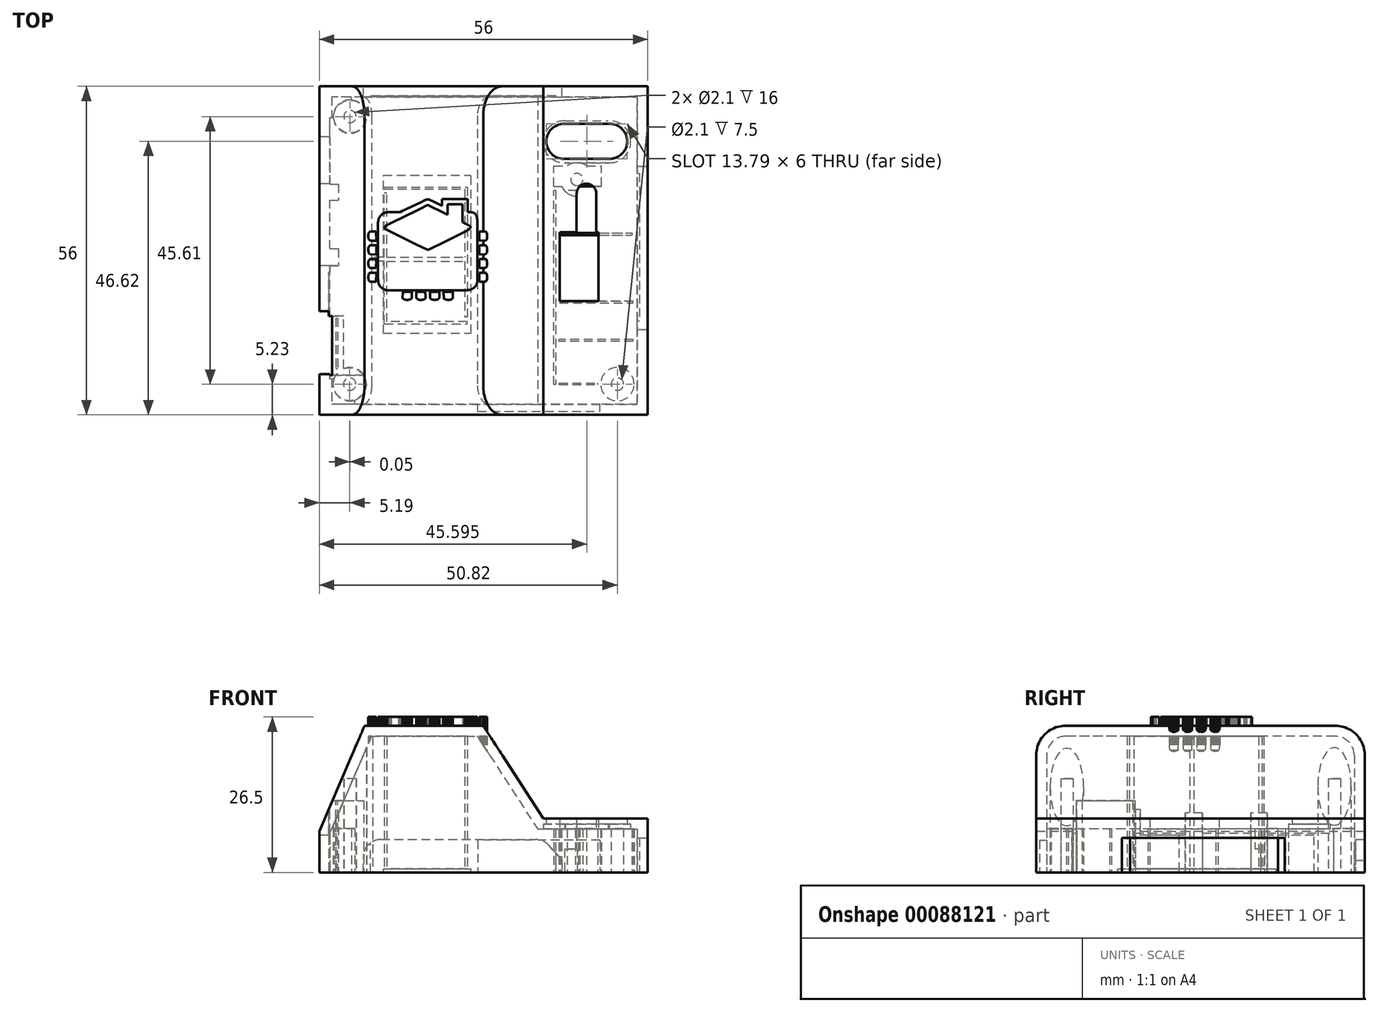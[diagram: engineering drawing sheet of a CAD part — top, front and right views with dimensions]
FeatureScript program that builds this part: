
annotation { "Feature Type Name" : "Feature", "Feature Type Description" : "" }
export const myFeature = defineFeature(function(context is Context, id is Id, definition is map)
    precondition{}
    {
        {
            var Q0;
            Q0=qCreatedBy(makeId("Top.planeOp"),FACE);
            var sketch = newSketch(context, id + "F0", { "sketchPlane" : qUnion([Q0])});
            skLineSegment(sketch, "E0.rect.bottom", {"start": v(22.84, -21.13) * mm, "end": v(-26.83, -21.13) * mm});
            skLineSegment(sketch, "E0.rect.top", {"start": v(22.84, 28.7) * mm, "end": v(-26.83, 28.7) * mm});
            skLineSegment(sketch, "E0.rect.left", {"start": v(22.84, -21.13) * mm, "end": v(22.84, 28.7) * mm});
            skPoint(sketch, "E0.rect.middle", {"position": v(-2, 3.78) * mm});
            skCircle(sketch, "E1", {"center": v(-24.81, -18.99) * mm, "radius": 1.05 * mm});
            skCircle(sketch, "E2", {"center": v(-24.76, 26.62) * mm, "radius": 1.05 * mm});
            skCircle(sketch, "E3", {"center": v(13.92, 15.91) * mm, "radius": 1.05 * mm});
            skLineSegment(sketch, "E4", {"start": v(-2, -21.13) * mm, "end": v(-2, -18.21) * mm});
            skCircle(sketch, "E5.MirrorC", {"center": v(20.82, -18.99) * mm, "radius": 1.05 * mm});
            skLineSegment(sketch, "E6.rect.bottom", {"start": v(24.75, -22.97) * mm, "end": v(-28.75, -22.97) * mm});
            skLineSegment(sketch, "E6.rect.top", {"start": v(24.75, 30.53) * mm, "end": v(-28.75, 30.53) * mm});
            skLineSegment(sketch, "E6.rect.left", {"start": v(24.75, -22.97) * mm, "end": v(24.75, 30.53) * mm});
            skLineSegment(sketch, "E6.rect.right", {"start": v(-28.75, -22.97) * mm, "end": v(-28.75, 30.53) * mm});
            skLineSegment(sketch, "E7.rect.bottom", {"start": v(26, -24.22) * mm, "end": v(-30, -24.22) * mm});
            skLineSegment(sketch, "E7.rect.top", {"start": v(26, 31.78) * mm, "end": v(-30, 31.78) * mm});
            skLineSegment(sketch, "E7.rect.left", {"start": v(26, -24.22) * mm, "end": v(26, 31.78) * mm});
            skLineSegment(sketch, "E7.rect.right", {"start": v(-30, -24.22) * mm, "end": v(-30, 31.78) * mm});
            skPoint(sketch, "E8", {"position": v(8.65, 14) * mm});
            skSolve(sketch);
        }
        {
            var Q0;
            Q0=qSketchRegion(id+"F0",true);
            var Q1;
            Q1=makeQuery(id+"F0.imprint","IMPRINT",FACE,{"disambiguationData":[TD([[makeQuery(id+"F0.imprint","IMPRINT",EDGE,{"derivedFrom":sQuery(id+"F0.wireOp",EDGE,"E1")}),-1.0]])]});
            extrude(context, id + "F1", {"entities" : qUnion([Q0, Q1]), "depth" : 25 * mm});
        }
        {
            var Q0;
            Q0=qCreatedBy(makeId("Front.planeOp"),FACE);
            var sketch = newSketch(context, id + "F2", { "sketchPlane" : qUnion([Q0])});
            skLineSegment(sketch, "E9", {"start": v(0, 0) * mm, "end": v(0, 7) * mm});
            skLineSegment(sketch, "E10", {"start": v(0, 7) * mm, "end": v(26.03, 7) * mm});
            skLineSegment(sketch, "E11", {"start": v(26.03, 9.19) * mm, "end": v(26.03, 25.51) * mm});
            skLineSegment(sketch, "E12", {"start": v(15.3, 7) * mm, "end": v(26.03, 7) * mm});
            skLineSegment(sketch, "E13", {"start": v(0, 7) * mm, "end": v(-30.02, 7) * mm});
            skLineSegment(sketch, "E14", {"start": v(-30.02, 7) * mm, "end": v(-22.06, 25.51) * mm});
            skLineSegment(sketch, "E15", {"start": v(-22.06, 25.51) * mm, "end": v(-2.39, 25.51) * mm});
            skLineSegment(sketch, "E16", {"start": v(26.03, 25.51) * mm, "end": v(-2.39, 25.51) * mm});
            skLineSegment(sketch, "E17", {"start": v(-22.06, 25.51) * mm, "end": v(-30.02, 25.51) * mm});
            skLineSegment(sketch, "E18", {"start": v(-30.02, 25.51) * mm, "end": v(-30.02, 7) * mm});
            skLineSegment(sketch, "E19", {"start": v(18.06, 10.7) * mm, "end": v(18.04, 10.7) * mm});
            skLineSegment(sketch, "E20", {"start": v(19.86, 9.19) * mm, "end": v(8.2, 9.19) * mm});
            skLineSegment(sketch, "E21", {"start": v(8.2, 9.19) * mm, "end": v(-2.39, 25.51) * mm});
            skLineSegment(sketch, "E22", {"start": v(19.86, 9.19) * mm, "end": v(26.03, 9.19) * mm});
            skSolve(sketch);
        }
        {
            var Q0;
            Q0=makeQuery(id+"F2.imprint","IMPRINT",FACE,{"disambiguationData":[TD([[makeQuery(id+"F2.imprint","IMPRINT",EDGE,{"derivedFrom":sQuery(id+"F2.wireOp",EDGE,"E14")}),1.0]])]});
            var Q1;
            {var subQ0=sQuery(id+"F2.wireOp",EDGE,"E11");Q1=makeQuery(id+"F2.imprint","IMPRINT",FACE,{"disambiguationData":[TD([[makeQuery(id+"F2.imprint","IMPRINT",EDGE,{"derivedFrom":subQ0}),1.0]])]});}
            extrude(context, id + "F3", {"entities" : qUnion([Q0, Q1]), "operationType" : NewBodyOperationType.REMOVE, "endBound" : BoundingType.UP_TO_NEXT, "oppositeDirection" : true, "depth" : 25 * mm, "hasSecondDirection" : true, "secondDirectionOppositeDirection" : false, "secondDirectionDepth" : 25 * mm});
        }
        {
            var Q0;
            Q0=makeQuery(id+"F1.opExtrude","CAP_EDGE",EDGE,{"disambiguationData":[OSD([sQuery(id+"F0.wireOp",EDGE,"E7.rect.right")])],"isStart":false});
            var Q1;
            Q1=makeQuery(id+"F3.boolean.opBoolean","COPY",EDGE,{"derivedFrom":makeQuery(id+"F3.opExtrude","TWEAK_EDGE",EDGE,{"derivedFrom":[makeQuery(id+"F1.opExtrude","CAP_FACE",FACE,{"disambiguationData":[OSD([sQuery(id+"F0.wireOp",EDGE,"E1"),sQuery(id+"F0.wireOp",EDGE,"E2"),sQuery(id+"F0.wireOp",EDGE,"E3"),sQuery(id+"F0.wireOp",EDGE,"E5.MirrorC"),sQuery(id+"F0.wireOp",EDGE,"E7.rect.bottom"),sQuery(id+"F0.wireOp",EDGE,"E7.rect.top"),sQuery(id+"F0.wireOp",EDGE,"E7.rect.left"),sQuery(id+"F0.wireOp",EDGE,"E7.rect.right")])],"isStart":false}),makeQuery(id+"F2.imprint","IMPRINT",EDGE,{"derivedFrom":sQuery(id+"F2.wireOp",EDGE,"ff17f17f-c23f-4b7b-92e3-773d52701edb")})]})});
            var Q2;
            Q2=makeQuery(id+"F3.boolean.opBoolean","COPY",EDGE,{"derivedFrom":makeQuery(id+"F3.opExtrude","TWEAK_EDGE",EDGE,{"derivedFrom":[makeQuery(id+"F1.opExtrude","CAP_FACE",FACE,{"disambiguationData":[OSD([sQuery(id+"F0.wireOp",EDGE,"E1"),sQuery(id+"F0.wireOp",EDGE,"E2"),sQuery(id+"F0.wireOp",EDGE,"E3"),sQuery(id+"F0.wireOp",EDGE,"E5.MirrorC"),sQuery(id+"F0.wireOp",EDGE,"E7.rect.bottom"),sQuery(id+"F0.wireOp",EDGE,"E7.rect.top"),sQuery(id+"F0.wireOp",EDGE,"E7.rect.left"),sQuery(id+"F0.wireOp",EDGE,"E7.rect.right")])],"isStart":false}),makeQuery(id+"F2.imprint","IMPRINT",EDGE,{"derivedFrom":sQuery(id+"F2.wireOp",EDGE,"7c30f75c-de24-4105-9ec6-0528e7197d9e")})]})});
            var Q3;
            {var subQ0=sQuery(id+"F2.wireOp",EDGE,"cpQ2IQLn-lepx-jHqE-Occg-QwCyzWVKbBFz");var subQ1=sQuery(id+"F2.wireOp",EDGE,"9136473a-ce9f-4df1-8e41-d79c079f6f02");var subQ2=makeQuery(id+"F2.imprint","INTERSECT",VERTEX,{"disambiguationData":[OD(0.0)],"derivedFrom":[subQ1,subQ0]});var subQ4=makeQuery(id+"F2.imprint","INTERSECT",VERTEX,{"disambiguationData":[OD(1.0)],"derivedFrom":[subQ1,subQ0]});Q3=makeQuery(id+"F3.boolean.opBoolean","COPY",EDGE,{"derivedFrom":makeQuery(id+"F3.opExtrude","TWEAK_EDGE",EDGE,{"derivedFrom":[makeQuery(id+"F1.opExtrude","CAP_FACE",FACE,{"disambiguationData":[OSD([sQuery(id+"F0.wireOp",EDGE,"E1"),sQuery(id+"F0.wireOp",EDGE,"E2"),sQuery(id+"F0.wireOp",EDGE,"E3"),sQuery(id+"F0.wireOp",EDGE,"E5.MirrorC"),sQuery(id+"F0.wireOp",EDGE,"E7.rect.bottom"),sQuery(id+"F0.wireOp",EDGE,"E7.rect.top"),sQuery(id+"F0.wireOp",EDGE,"E7.rect.left"),sQuery(id+"F0.wireOp",EDGE,"E7.rect.right")])],"isStart":false}),makeQuery(id+"F2.imprint","IMPRINT",EDGE,{"disambiguationData":[TD([[subQ4,1.0]])],"derivedFrom":subQ0}),makeQuery(id+"F2.imprint","IMPRINT",EDGE,{"disambiguationData":[TD([[subQ2,1.0]])],"derivedFrom":subQ0}),makeQuery(id+"F2.imprint","IMPRINT",EDGE,{"disambiguationData":[TD([[subQ2,-1.0]])],"derivedFrom":subQ0})]})});}
            var Q4;
            {var subQ0=sQuery(id+"F2.wireOp",EDGE,"cpQ2IQLn-lepx-jHqE-Occg-QwCyzWVKbBFz");var subQ1=sQuery(id+"F2.wireOp",EDGE,"9136473a-ce9f-4df1-8e41-d79c079f6f02");var subQ2=makeQuery(id+"F2.imprint","INTERSECT",VERTEX,{"disambiguationData":[OD(0.0)],"derivedFrom":[subQ1,subQ0]});var subQ3=sQuery(id+"F2.wireOp",EDGE,"7c30f75c-de24-4105-9ec6-0528e7197d9e");var subQ4=makeQuery(id+"F2.imprint","INTERSECT",VERTEX,{"derivedFrom":[subQ3,subQ0]});var subQ5=makeQuery(id+"F2.imprint","INTERSECT",VERTEX,{"disambiguationData":[OD(1.0)],"derivedFrom":[subQ1,subQ0]});Q4=makeQuery(id+"F3.boolean.opBoolean","COPY",EDGE,{"derivedFrom":makeQuery(id+"F3.opExtrude","TWEAK_EDGE",EDGE,{"disambiguationData":[OD(0.0)],"derivedFrom":[makeQuery(id+"F2.imprint","IMPRINT",EDGE,{"disambiguationData":[TD([[subQ4,1.0]])],"derivedFrom":subQ3}),makeQuery(id+"F2.imprint","IMPRINT",EDGE,{"disambiguationData":[TD([[subQ5,1.0]])],"derivedFrom":subQ0}),makeQuery(id+"F2.imprint","IMPRINT",EDGE,{"disambiguationData":[TD([[subQ2,1.0]])],"derivedFrom":subQ0}),makeQuery(id+"F2.imprint","IMPRINT",EDGE,{"disambiguationData":[TD([[subQ2,-1.0]])],"derivedFrom":subQ0})]})});}
            var Q5;
            {var subQ0=sQuery(id+"F2.wireOp",EDGE,"cpQ2IQLn-lepx-jHqE-Occg-QwCyzWVKbBFz");var subQ1=sQuery(id+"F2.wireOp",EDGE,"9136473a-ce9f-4df1-8e41-d79c079f6f02");var subQ2=makeQuery(id+"F2.imprint","INTERSECT",VERTEX,{"disambiguationData":[OD(0.0)],"derivedFrom":[subQ1,subQ0]});var subQ3=sQuery(id+"F2.wireOp",EDGE,"7c30f75c-de24-4105-9ec6-0528e7197d9e");var subQ4=makeQuery(id+"F2.imprint","INTERSECT",VERTEX,{"derivedFrom":[subQ3,subQ0]});var subQ5=makeQuery(id+"F2.imprint","INTERSECT",VERTEX,{"disambiguationData":[OD(1.0)],"derivedFrom":[subQ1,subQ0]});Q5=makeQuery(id+"F3.boolean.opBoolean","COPY",EDGE,{"derivedFrom":makeQuery(id+"F3.opExtrude","TWEAK_EDGE",EDGE,{"disambiguationData":[OD(1.0)],"derivedFrom":[makeQuery(id+"F2.imprint","IMPRINT",EDGE,{"disambiguationData":[TD([[subQ4,1.0]])],"derivedFrom":subQ3}),makeQuery(id+"F2.imprint","IMPRINT",EDGE,{"disambiguationData":[TD([[subQ5,1.0]])],"derivedFrom":subQ0}),makeQuery(id+"F2.imprint","IMPRINT",EDGE,{"disambiguationData":[TD([[subQ2,1.0]])],"derivedFrom":subQ0}),makeQuery(id+"F2.imprint","IMPRINT",EDGE,{"disambiguationData":[TD([[subQ2,-1.0]])],"derivedFrom":subQ0})]})});}
            var Q6;
            Q6=makeQuery(id+"F1.opExtrude","CAP_EDGE",EDGE,{"disambiguationData":[OSD([sQuery(id+"F0.wireOp",EDGE,"E7.rect.bottom")])],"isStart":false});
            var Q7;
            {var subQ0=sQuery(id+"F2.wireOp",EDGE,"cpQ2IQLn-lepx-jHqE-Occg-QwCyzWVKbBFz");var subQ1=sQuery(id+"F2.wireOp",EDGE,"9136473a-ce9f-4df1-8e41-d79c079f6f02");var subQ2=makeQuery(id+"F2.imprint","INTERSECT",VERTEX,{"disambiguationData":[OD(0.0)],"derivedFrom":[subQ1,subQ0]});var subQ4=makeQuery(id+"F2.imprint","INTERSECT",VERTEX,{"disambiguationData":[OD(1.0)],"derivedFrom":[subQ1,subQ0]});Q7=makeQuery(id+"F3.boolean.opBoolean","COPY",EDGE,{"derivedFrom":makeQuery(id+"F3.opExtrude","TWEAK_EDGE",EDGE,{"derivedFrom":[makeQuery(id+"F1.opExtrude","SWEPT_FACE",FACE,{"disambiguationData":[OSD([sQuery(id+"F0.wireOp",EDGE,"E7.rect.bottom")])]}),makeQuery(id+"F2.imprint","IMPRINT",EDGE,{"disambiguationData":[TD([[subQ4,1.0]])],"derivedFrom":subQ0}),makeQuery(id+"F2.imprint","IMPRINT",EDGE,{"disambiguationData":[TD([[subQ2,1.0]])],"derivedFrom":subQ0}),makeQuery(id+"F2.imprint","IMPRINT",EDGE,{"disambiguationData":[TD([[subQ2,-1.0]])],"derivedFrom":subQ0})]})});}
            var Q8;
            Q8=makeQuery(id+"F1.opExtrude","CAP_EDGE",EDGE,{"disambiguationData":[OSD([sQuery(id+"F0.wireOp",EDGE,"E7.rect.top")])],"isStart":false});
            var Q9;
            {var subQ0=sQuery(id+"F2.wireOp",EDGE,"cpQ2IQLn-lepx-jHqE-Occg-QwCyzWVKbBFz");var subQ1=sQuery(id+"F2.wireOp",EDGE,"9136473a-ce9f-4df1-8e41-d79c079f6f02");var subQ2=makeQuery(id+"F2.imprint","INTERSECT",VERTEX,{"disambiguationData":[OD(0.0)],"derivedFrom":[subQ1,subQ0]});var subQ4=makeQuery(id+"F2.imprint","INTERSECT",VERTEX,{"disambiguationData":[OD(1.0)],"derivedFrom":[subQ1,subQ0]});Q9=makeQuery(id+"F3.boolean.opBoolean","COPY",EDGE,{"derivedFrom":makeQuery(id+"F3.opExtrude","TWEAK_EDGE",EDGE,{"derivedFrom":[makeQuery(id+"F1.opExtrude","SWEPT_FACE",FACE,{"disambiguationData":[OSD([sQuery(id+"F0.wireOp",EDGE,"E7.rect.top")])]}),makeQuery(id+"F2.imprint","IMPRINT",EDGE,{"disambiguationData":[TD([[subQ4,1.0]])],"derivedFrom":subQ0}),makeQuery(id+"F2.imprint","IMPRINT",EDGE,{"disambiguationData":[TD([[subQ2,1.0]])],"derivedFrom":subQ0}),makeQuery(id+"F2.imprint","IMPRINT",EDGE,{"disambiguationData":[TD([[subQ2,-1.0]])],"derivedFrom":subQ0})]})});}
            var Q10;
            Q10=makeQuery(id+"F3.boolean.opBoolean","COPY",EDGE,{"derivedFrom":makeQuery(id+"F3.opExtrude","TWEAK_EDGE",EDGE,{"derivedFrom":[makeQuery(id+"F1.opExtrude","CAP_FACE",FACE,{"disambiguationData":[OSD([sQuery(id+"F0.wireOp",EDGE,"E1"),sQuery(id+"F0.wireOp",EDGE,"E2"),sQuery(id+"F0.wireOp",EDGE,"E3"),sQuery(id+"F0.wireOp",EDGE,"E5.MirrorC"),sQuery(id+"F0.wireOp",EDGE,"E7.rect.bottom"),sQuery(id+"F0.wireOp",EDGE,"E7.rect.top"),sQuery(id+"F0.wireOp",EDGE,"E7.rect.left"),sQuery(id+"F0.wireOp",EDGE,"E7.rect.right")])],"isStart":false}),makeQuery(id+"F2.imprint","IMPRINT",EDGE,{"derivedFrom":sQuery(id+"F2.wireOp",EDGE,"99fa5713-44e2-4710-8a3e-a5a5802f03ed")})]})});
            var Q11;
            Q11=makeQuery(id+"F3.boolean.opBoolean","COPY",EDGE,{"derivedFrom":makeQuery(id+"F3.opExtrude","TWEAK_EDGE",EDGE,{"derivedFrom":[makeQuery(id+"F1.opExtrude","CAP_FACE",FACE,{"disambiguationData":[OSD([sQuery(id+"F0.wireOp",EDGE,"E1"),sQuery(id+"F0.wireOp",EDGE,"E2"),sQuery(id+"F0.wireOp",EDGE,"E3"),sQuery(id+"F0.wireOp",EDGE,"E5.MirrorC"),sQuery(id+"F0.wireOp",EDGE,"E7.rect.bottom"),sQuery(id+"F0.wireOp",EDGE,"E7.rect.top"),sQuery(id+"F0.wireOp",EDGE,"E7.rect.left"),sQuery(id+"F0.wireOp",EDGE,"E7.rect.right")])],"isStart":false}),makeQuery(id+"F2.imprint","IMPRINT",EDGE,{"derivedFrom":sQuery(id+"F2.wireOp",EDGE,"E14")})]})});
            var Q12;
            Q12=makeQuery(id+"F3.boolean.opBoolean","COPY",EDGE,{"derivedFrom":makeQuery(id+"F3.opExtrude","TWEAK_EDGE",EDGE,{"derivedFrom":[makeQuery(id+"F1.opExtrude","CAP_FACE",FACE,{"disambiguationData":[OSD([sQuery(id+"F0.wireOp",EDGE,"E1"),sQuery(id+"F0.wireOp",EDGE,"E2"),sQuery(id+"F0.wireOp",EDGE,"E3"),sQuery(id+"F0.wireOp",EDGE,"E5.MirrorC"),sQuery(id+"F0.wireOp",EDGE,"E7.rect.bottom"),sQuery(id+"F0.wireOp",EDGE,"E7.rect.top"),sQuery(id+"F0.wireOp",EDGE,"E7.rect.left"),sQuery(id+"F0.wireOp",EDGE,"E7.rect.right")])],"isStart":false}),makeQuery(id+"F2.imprint","IMPRINT",EDGE,{"derivedFrom":sQuery(id+"F2.wireOp",EDGE,"E21")})]})});
            var Q13;
            Q13=makeQuery(id+"F3.boolean.opBoolean","COPY",EDGE,{"derivedFrom":makeQuery(id+"F3.opExtrude","TWEAK_EDGE",EDGE,{"derivedFrom":[makeQuery(id+"F2.imprint","IMPRINT",EDGE,{"derivedFrom":sQuery(id+"F2.wireOp",EDGE,"E20")}),makeQuery(id+"F2.imprint","IMPRINT",EDGE,{"derivedFrom":sQuery(id+"F2.wireOp",EDGE,"E21")})]})});
            var Q14;
            Q14=makeQuery(id+"F3.boolean.opBoolean","COPY",EDGE,{"derivedFrom":makeQuery(id+"F3.opExtrude","TWEAK_EDGE",EDGE,{"derivedFrom":[makeQuery(id+"F1.opExtrude","SWEPT_FACE",FACE,{"disambiguationData":[OSD([sQuery(id+"F0.wireOp",EDGE,"E7.rect.bottom")])]}),makeQuery(id+"F2.imprint","IMPRINT",EDGE,{"derivedFrom":sQuery(id+"F2.wireOp",EDGE,"E21")})]})});
            var Q15;
            Q15=makeQuery(id+"F3.boolean.opBoolean","COPY",EDGE,{"derivedFrom":makeQuery(id+"F3.opExtrude","TWEAK_EDGE",EDGE,{"derivedFrom":[makeQuery(id+"F1.opExtrude","SWEPT_FACE",FACE,{"disambiguationData":[OSD([sQuery(id+"F0.wireOp",EDGE,"E7.rect.top")])]}),makeQuery(id+"F2.imprint","IMPRINT",EDGE,{"derivedFrom":sQuery(id+"F2.wireOp",EDGE,"E21")})]})});
            var Q16;
            Q16=makeQuery(id+"F3.boolean.opBoolean","COPY",EDGE,{"derivedFrom":makeQuery(id+"F3.opExtrude","TWEAK_EDGE",EDGE,{"derivedFrom":[makeQuery(id+"F1.opExtrude","SWEPT_FACE",FACE,{"disambiguationData":[OSD([sQuery(id+"F0.wireOp",EDGE,"E7.rect.left")])]}),makeQuery(id+"F2.imprint","IMPRINT",EDGE,{"derivedFrom":sQuery(id+"F2.wireOp",EDGE,"E20")}),makeQuery(id+"F2.imprint","IMPRINT",EDGE,{"derivedFrom":sQuery(id+"F2.wireOp",EDGE,"E22")})]})});
            var Q17;
            Q17=makeQuery(id+"F3.boolean.opBoolean","COPY",EDGE,{"derivedFrom":makeQuery(id+"F3.opExtrude","TWEAK_EDGE",EDGE,{"derivedFrom":[makeQuery(id+"F2.imprint","IMPRINT",EDGE,{"derivedFrom":sQuery(id+"F2.wireOp",EDGE,"E20")}),makeQuery(id+"F2.imprint","IMPRINT",EDGE,{"derivedFrom":sQuery(id+"F2.wireOp",EDGE,"E21")}),makeQuery(id+"F2.imprint","IMPRINT",EDGE,{"derivedFrom":sQuery(id+"F2.wireOp",EDGE,"E22")})]})});
            fillet(context, id + "F4", {"entities" : qUnion([Q0, Q1, Q2, Q3, Q4, Q5, Q6, Q7, Q8, Q9, Q10, Q11, Q12, Q13, Q14, Q15, Q16, Q17]), "radius" : 5 * mm, "tangentPropagation" : true, "allowEdgeOverflow" : false});
        }
        {
            var Q0;
            Q0=makeQuery(id+"F1.opExtrude","SWEPT_BODY",BODY,{"disambiguationData":[OSD([sQuery(id+"F0.wireOp",EDGE,"E1"),sQuery(id+"F0.wireOp",EDGE,"E2"),sQuery(id+"F0.wireOp",EDGE,"E3"),sQuery(id+"F0.wireOp",EDGE,"E5.MirrorC"),sQuery(id+"F0.wireOp",EDGE,"E7.rect.bottom"),sQuery(id+"F0.wireOp",EDGE,"E7.rect.top"),sQuery(id+"F0.wireOp",EDGE,"E7.rect.left"),sQuery(id+"F0.wireOp",EDGE,"E7.rect.right")])]});
            transform(context, id + "F5", {"entities" : qUnion([Q0]), "transformType" : TransformType.TRANSLATION_3D, "dx" : -5 * mm, "dy" : -12 * mm, "dz" : 0 * mm, "makeCopy" : false});
        }
        {
            var Q0;
            Q0=makeQuery(id+"F1.opExtrude","CAP_FACE",FACE,{"disambiguationData":[OSD([sQuery(id+"F0.wireOp",EDGE,"E1"),sQuery(id+"F0.wireOp",EDGE,"E2"),sQuery(id+"F0.wireOp",EDGE,"E3"),sQuery(id+"F0.wireOp",EDGE,"E5.MirrorC"),sQuery(id+"F0.wireOp",EDGE,"E7.rect.bottom"),sQuery(id+"F0.wireOp",EDGE,"E7.rect.top"),sQuery(id+"F0.wireOp",EDGE,"E7.rect.left"),sQuery(id+"F0.wireOp",EDGE,"E7.rect.right")])],"isStart":true});
            shell(context, id + "F6", {"entities" : qUnion([Q0]), "thickness" : 1.8 * mm});
        }
        {
            var Q0;
            Q0=makeQuery(id+"F1.opExtrude","SWEPT_FACE",FACE,{"disambiguationData":[OSD([sQuery(id+"F0.wireOp",EDGE,"E7.rect.left")])]});
            cPlane(context, id + "F7", {"entities" : qUnion([Q0]), "cplaneType" : CPlaneType.OFFSET, "offset" : 0 * mm, "width" : 150 * mm, "height" : 150 * mm});
        }
        {
            var Q0;
            Q0=qCreatedBy(id+"F7.planeOp",FACE);
            var sketch = newSketch(context, id + "F8", { "sketchPlane" : qUnion([Q0])});
            skLineSegment(sketch, "E23.bottom", {"start": v(6.92, 0) * mm, "end": v(-20.2, 0) * mm});
            skLineSegment(sketch, "E23.top", {"start": v(6.12, 5.87) * mm, "end": v(-20.2, 5.87) * mm});
            skLineSegment(sketch, "E24", {"start": v(-20.2, 5.87) * mm, "end": v(-21.64, 5.87) * mm});
            skLineSegment(sketch, "E25", {"start": v(-21.64, 5.87) * mm, "end": v(-21.64, 0) * mm});
            skLineSegment(sketch, "E26", {"start": v(-21.64, 0) * mm, "end": v(-20.2, 0) * mm});
            skLineSegment(sketch, "E27", {"start": v(-20.2, 5.87) * mm, "end": v(-20.2, 0) * mm});
            skLineSegment(sketch, "E28", {"start": v(6.12, 5.87) * mm, "end": v(6.12, 0) * mm});
            skPoint(sketch, "E29.orphan", {"position": v(7.84, 0) * mm});
            skLineSegment(sketch, "E30", {"start": v(4.97, 0) * mm, "end": v(4.97, 5.87) * mm});
            skSolve(sketch);
        }
        {
            var Q0;
            Q0=qSketchRegion(id+"F8",true);
            extrude(context, id + "F9", {"entities" : qUnion([Q0]), "operationType" : NewBodyOperationType.REMOVE, "oppositeDirection" : true, "depth" : (1.7 - 0.3) * mm});
        }
        {
            var Q0;
            Q0=makeQuery(id+"F8.imprint","IMPRINT",FACE,{"disambiguationData":[TD([[makeQuery(id+"F8.imprint","IMPRINT",EDGE,{"derivedFrom":sQuery(id+"F8.wireOp",EDGE,"E24")}),1.0]])]});
            var Q1;
            {var subQ0=sQuery(id+"F8.wireOp",EDGE,"E23.left");Q1=makeQuery(id+"F8.imprint","IMPRINT",FACE,{"disambiguationData":[TD([[makeQuery(id+"F8.imprint","IMPRINT",EDGE,{"derivedFrom":subQ0}),1.0]])]});}
            var Q2;
            {var subQ0=sQuery(id+"F8.wireOp",EDGE,"4UiORLbo-slaH-JSft-xh6I-61qYCNnPId7j");Q2=makeQuery(id+"F8.imprint","IMPRINT",FACE,{"disambiguationData":[TD([[makeQuery(id+"F8.imprint","IMPRINT",EDGE,{"derivedFrom":subQ0}),1.0]])]});}
            var Q3;
            {var subQ0=sQuery(id+"F8.wireOp",EDGE,"E28");Q3=makeQuery(id+"F8.imprint","IMPRINT",FACE,{"disambiguationData":[TD([[makeQuery(id+"F8.imprint","IMPRINT",EDGE,{"derivedFrom":subQ0}),-1.0]])]});}
            extrude(context, id + "F10", {"entities" : qUnion([Q0, Q1, Q2, Q3]), "operationType" : NewBodyOperationType.REMOVE, "oppositeDirection" : true, "depth" : 2 * mm});
        }
        {
            var Q0;
            Q0=makeQuery(id+"F1.opExtrude","SWEPT_FACE",FACE,{"disambiguationData":[OSD([sQuery(id+"F0.wireOp",EDGE,"E7.rect.right")])]});
            cPlane(context, id + "F11", {"entities" : qUnion([Q0]), "cplaneType" : CPlaneType.OFFSET, "offset" : 0 * mm, "width" : 150 * mm, "height" : 150 * mm});
        }
        {
            var Q0;
            Q0=qCreatedBy(id+"F11.planeOp",FACE);
            var sketch = newSketch(context, id + "F12", { "sketchPlane" : qUnion([Q0])});
            skLineSegment(sketch, "E31.top", {"start": v(-11.15, 6.31) * mm, "end": v(-3.45, 6.31) * mm});
            skLineSegment(sketch, "E32", {"start": v(27.25, 11.15) * mm, "end": v(27.25, 11.15) * mm});
            skLineSegment(sketch, "E33", {"start": v(-11.15, 0) * mm, "end": v(-11.15, 6.31) * mm});
            skPoint(sketch, "E34.start.orphan", {"position": v(-15.15, 0) * mm});
            skLineSegment(sketch, "E35", {"start": v(29.28, 0) * mm, "end": v(-11.15, 0) * mm});
            skLineSegment(sketch, "E36", {"start": v(-10.29, 6.31) * mm, "end": v(-10.29, 0) * mm});
            skLineSegment(sketch, "E37", {"start": v(19.35, 12.2) * mm, "end": v(29.28, 12.2) * mm});
            skLineSegment(sketch, "E38", {"start": v(-11.15, 3.16) * mm, "end": v(-3.45, 3.16) * mm, "construction": true});
            skLineSegment(sketch, "E39", {"start": v(-3.45, 3.16) * mm, "end": v(-0.05, 3.16) * mm, "construction": true});
            skLineSegment(sketch, "E40", {"start": v(-0.05, 3.16) * mm, "end": v(7.65, 3.16) * mm, "construction": true});
            skLineSegment(sketch, "E41", {"start": v(7.65, 3.16) * mm, "end": v(11.05, 3.16) * mm, "construction": true});
            skLineSegment(sketch, "E42.trimOffspring", {"start": v(11.05, 6.31) * mm, "end": v(18.53, 6.31) * mm});
            skLineSegment(sketch, "E43", {"start": v(11.9, 6.31) * mm, "end": v(11.9, 0) * mm});
            skLineSegment(sketch, "E44", {"start": v(0, 6.31) * mm, "end": v(7.65, 6.31) * mm});
            skLineSegment(sketch, "E45", {"start": v(7.65, 0) * mm, "end": v(0, 0) * mm});
            skLineSegment(sketch, "E46", {"start": v(-3.45, 0) * mm, "end": v(-11.15, 0) * mm});
            skLineSegment(sketch, "E47", {"start": v(30.08, 0) * mm, "end": v(11.05, 0) * mm});
            skLineSegment(sketch, "E48.bottom", {"start": v(-0.32, 0) * mm, "end": v(-3.15, 0) * mm});
            skLineSegment(sketch, "E48.top", {"start": v(-0.32, 6.31) * mm, "end": v(-3.15, 6.31) * mm});
            skLineSegment(sketch, "E48.left", {"start": v(-0.32, 0) * mm, "end": v(-0.32, 6.31) * mm});
            skLineSegment(sketch, "E48.right", {"start": v(-3.15, 0) * mm, "end": v(-3.15, 6.31) * mm});
            skLineSegment(sketch, "E49.bottom", {"start": v(10.8, 0) * mm, "end": v(7.92, 0) * mm});
            skLineSegment(sketch, "E49.top", {"start": v(10.8, 6.31) * mm, "end": v(7.92, 6.31) * mm});
            skLineSegment(sketch, "E49.left", {"start": v(10.8, 0) * mm, "end": v(10.8, 6.31) * mm});
            skLineSegment(sketch, "E49.right", {"start": v(7.92, 0) * mm, "end": v(7.92, 6.31) * mm});
            skLineSegment(sketch, "E50", {"start": v(-3.45, 6.31) * mm, "end": v(11.05, 6.31) * mm});
            skLineSegment(sketch, "E51", {"start": v(29.28, 12.2) * mm, "end": v(29.28, 0) * mm});
            skPoint(sketch, "E52.end.orphan", {"position": v(30.08, 11.15) * mm});
            skPoint(sketch, "E52.start.orphan", {"position": v(30.08, 12.2) * mm});
            skLineSegment(sketch, "E53", {"start": v(18.53, 6.31) * mm, "end": v(18.53, 12.2) * mm});
            skLineSegment(sketch, "E54", {"start": v(18.53, 12.2) * mm, "end": v(19.35, 12.2) * mm});
            skPoint(sketch, "E55.start.orphan", {"position": v(19.35, 11.15) * mm});
            skPoint(sketch, "E56.end.orphan", {"position": v(19.35, 0) * mm});
            skPoint(sketch, "E56.start.orphan", {"position": v(19.35, 6.31) * mm});
            skLineSegment(sketch, "E57", {"start": v(28.38, 0) * mm, "end": v(28.38, 12.2) * mm});
            skLineSegment(sketch, "E58", {"start": v(19.35, 12.2) * mm, "end": v(19.35, 0) * mm});
            skSolve(sketch);
        }
        {
            var Q0;
            {var subQ0=sQuery(id+"F12.wireOp",EDGE,"E33");Q0=makeQuery(id+"F12.imprint","IMPRINT",FACE,{"disambiguationData":[TD([[makeQuery(id+"F12.imprint","IMPRINT",EDGE,{"derivedFrom":subQ0}),-1.0]])]});}
            var Q1;
            {var subQ1=sQuery(id+"F12.wireOp",EDGE,"E36");Q1=makeQuery(id+"F12.imprint","IMPRINT",FACE,{"disambiguationData":[TD([[makeQuery(id+"F12.imprint","IMPRINT",EDGE,{"derivedFrom":subQ1}),1.0]])]});}
            var Q2;
            {var subQ0=sQuery(id+"F12.wireOp",EDGE,"LVVauTd6-uSLQ-SWm0-nvuu-HrEgJgk2loCY");Q2=makeQuery(id+"F12.imprint","IMPRINT",FACE,{"disambiguationData":[TD([[makeQuery(id+"F12.imprint","IMPRINT",EDGE,{"derivedFrom":subQ0}),-1.0]])]});}
            var Q3;
            Q3=makeQuery(id+"F12.imprint","IMPRINT",FACE,{"disambiguationData":[TD([[makeQuery(id+"F12.imprint","IMPRINT",EDGE,{"derivedFrom":sQuery(id+"F12.wireOp",EDGE,"Bzj0w9RH-aYdH-ZF7y-Z4mK-Pif1xP8myCSu")}),1.0]])]});
            var Q4;
            {var subQ2=sQuery(id+"F12.wireOp",EDGE,"E43");Q4=makeQuery(id+"F12.imprint","IMPRINT",FACE,{"disambiguationData":[TD([[makeQuery(id+"F12.imprint","IMPRINT",EDGE,{"derivedFrom":subQ2}),1.0]])]});}
            extrude(context, id + "F13", {"entities" : qUnion([Q0, Q1, Q2, Q3, Q4]), "operationType" : NewBodyOperationType.REMOVE, "oppositeDirection" : true, "depth" : 1.6 * mm});
        }
        {
            var Q0;
            {var subQ2=sQuery(id+"F12.wireOp",EDGE,"E57");Q0=makeQuery(id+"F12.imprint","IMPRINT",FACE,{"disambiguationData":[TD([[makeQuery(id+"F12.imprint","IMPRINT",EDGE,{"derivedFrom":subQ2}),1.0]])]});}
            var Q1;
            {var subQ0=sQuery(id+"F12.wireOp",EDGE,"E33");Q1=makeQuery(id+"F12.imprint","IMPRINT",FACE,{"disambiguationData":[TD([[makeQuery(id+"F12.imprint","IMPRINT",EDGE,{"derivedFrom":subQ0}),-1.0]])]});}
            var Q2;
            {var subQ1=sQuery(id+"F12.wireOp",EDGE,"E45");Q2=makeQuery(id+"F12.imprint","IMPRINT",FACE,{"disambiguationData":[TD([[makeQuery(id+"F12.imprint","IMPRINT",EDGE,{"derivedFrom":subQ1}),-1.0]])]});}
            var Q3;
            {var subQ3=sQuery(id+"F12.wireOp",EDGE,"E36");Q3=makeQuery(id+"F12.imprint","IMPRINT",FACE,{"disambiguationData":[TD([[makeQuery(id+"F12.imprint","IMPRINT",EDGE,{"derivedFrom":subQ3}),1.0]])]});}
            var Q4;
            {var subQ3=sQuery(id+"F12.wireOp",EDGE,"E43");Q4=makeQuery(id+"F12.imprint","IMPRINT",FACE,{"disambiguationData":[TD([[makeQuery(id+"F12.imprint","IMPRINT",EDGE,{"derivedFrom":subQ3}),-1.0]])]});}
            var Q5;
            {var subQ0=sQuery(id+"F12.wireOp",EDGE,"E51");Q5=makeQuery(id+"F12.imprint","IMPRINT",FACE,{"disambiguationData":[TD([[makeQuery(id+"F12.imprint","IMPRINT",EDGE,{"derivedFrom":subQ0}),-1.0]])]});}
            extrude(context, id + "F14", {"entities" : qUnion([Q0, Q1, Q2, Q3, Q4, Q5]), "operationType" : NewBodyOperationType.REMOVE, "oppositeDirection" : true, "depth" : 8 * mm});
        }
        {
            var Q0;
            Q0=qCreatedBy(makeId("Top.planeOp"),FACE);
            var sketch = newSketch(context, id + "F15", { "sketchPlane" : qUnion([Q0])});
            skLineSegment(sketch, "E59.bottom", {"start": v(-27.19, -29.45) * mm, "end": v(-33.17, -29.45) * mm});
            skLineSegment(sketch, "E59.top", {"start": v(-27.19, -20) * mm, "end": v(-33.17, -20) * mm});
            skLineSegment(sketch, "E59.left", {"start": v(-27.19, -29.45) * mm, "end": v(-27.19, -21.32) * mm});
            skLineSegment(sketch, "E59.right", {"start": v(-33.17, -29.45) * mm, "end": v(-33.17, -21.32) * mm});
            skLineSegment(sketch, "E60", {"start": v(-33.17, -20.99) * mm, "end": v(-27.19, -20.99) * mm});
            skLineSegment(sketch, "E61", {"start": v(-33.17, -21.32) * mm, "end": v(-27.19, -21.32) * mm});
            skLineSegment(sketch, "E62.trimOffspring", {"start": v(-27.19, -20.99) * mm, "end": v(-27.19, -20) * mm});
            skLineSegment(sketch, "E63.trimOffspring", {"start": v(-33.17, -20.99) * mm, "end": v(-33.17, -20) * mm});
            skSolve(sketch);
        }
        {
            var Q0;
            Q0=qSketchRegion(id+"F15",true);
            var Q1;
            {var subQ0=sQuery(id+"F12.wireOp",EDGE,"E37");Q1=makeQuery(id+"F14.boolean.opBoolean","COPY",FACE,{"derivedFrom":makeQuery(id+"F14.opExtrude","SWEPT_FACE",FACE,{"disambiguationData":[OSD([subQ0]),TDD([makeQuery(id+"F12.imprint","IMPRINT",EDGE,{"disambiguationData":[TD([[makeQuery(id+"F12.imprint","INTERSECT",VERTEX,{"derivedFrom":[subQ0,sQuery(id+"F12.wireOp",EDGE,"E52")]}),1.0]])],"derivedFrom":subQ0})])]})});}
            extrude(context, id + "F16", {"entities" : qUnion([Q0]), "operationType" : NewBodyOperationType.REMOVE, "endBound" : BoundingType.UP_TO_SURFACE, "endBoundEntityFace" : qUnion([Q1]), "depth" : 11.3 * mm});
        }
        {
            var Q0;
            Q0=makeQuery(id+"F1.opExtrude","SWEPT_FACE",FACE,{"disambiguationData":[OSD([sQuery(id+"F0.wireOp",EDGE,"E7.rect.top")])]});
            cPlane(context, id + "F17", {"entities" : qUnion([Q0]), "cplaneType" : CPlaneType.OFFSET, "offset" : 0 * mm, "width" : 150 * mm, "height" : 150 * mm});
        }
        {
            var Q0;
            Q0=qCreatedBy(id+"F17.planeOp",FACE);
            var sketch = newSketch(context, id + "F18", { "sketchPlane" : qUnion([Q0])});
            skLineSegment(sketch, "E64.bottom", {"start": v(-6.36, 0) * mm, "end": v(27.5, 0) * mm});
            skLineSegment(sketch, "E64.left", {"start": v(-6.36, 0) * mm, "end": v(-6.36, 2.05) * mm});
            skLineSegment(sketch, "E65", {"start": v(-5.32, 3.26) * mm, "end": v(-5.32, 0) * mm});
            skLineSegment(sketch, "E66", {"start": v(27.5, 2.61) * mm, "end": v(27.5, 0) * mm});
            skLineSegment(sketch, "E67", {"start": v(26.27, 5.04) * mm, "end": v(26.27, 0) * mm});
            skPoint(sketch, "E68.visualSharp", {"position": v(-6.36, 7.05) * mm});
            skLineSegment(sketch, "E69", {"start": v(-6.36, 2.05) * mm, "end": v(-4.17, 4.58) * mm});
            skLineSegment(sketch, "E70", {"start": v(24.5, 5.61) * mm, "end": v(-1.9, 5.61) * mm});
            skPoint(sketch, "E71.visualSharp", {"position": v(-3.28, 5.61) * mm});
            skArc(sketch, "E71.filletArc", {"start": v(-1.9, 5.61) * mm, "mid": v(-3.15, 5.34) * mm, "end": v(-4.17, 4.58) * mm});
            skPoint(sketch, "E72.visualSharp", {"position": v(27.5, 5.61) * mm});
            skArc(sketch, "E72.filletArc", {"start": v(27.5, 2.61) * mm, "mid": v(26.63, 4.73) * mm, "end": v(24.5, 5.61) * mm});
            skSolve(sketch);
        }
        {
            var Q0;
            Q0=qSketchRegion(id+"F18",true);
            extrude(context, id + "F19", {"entities" : qUnion([Q0]), "operationType" : NewBodyOperationType.REMOVE, "oppositeDirection" : true, "depth" : 1.6 * mm});
        }
        {
            var Q0;
            Q0=qCreatedBy(makeId("Top.planeOp"),FACE);
            var sketch = newSketch(context, id + "F20", { "sketchPlane" : qUnion([Q0])});
            skArc(sketch, "E73", {"start": v(6.16, 2.02) * mm, "mid": v(8.9, 0.56) * mm, "end": v(11.63, 2.02) * mm});
            skLineSegment(sketch, "E74", {"start": v(11.63, 2.02) * mm, "end": v(6.16, 2.02) * mm});
            skSolve(sketch);
        }
        {
            var Q0;
            Q0=qSketchRegion(id+"F20",true);
            extrude(context, id + "F21", {"entities" : qUnion([Q0]), "operationType" : NewBodyOperationType.REMOVE, "depth" : 4 * mm});
        }
        {
            var Q0;
            {var subQ0=sQuery(id+"F18.wireOp",EDGE,"E64.left");Q0=makeQuery(id+"F18.imprint","IMPRINT",FACE,{"disambiguationData":[TD([[makeQuery(id+"F18.imprint","IMPRINT",EDGE,{"derivedFrom":subQ0}),-1.0]])]});}
            var Q1;
            {var subQ0=sQuery(id+"F18.wireOp",EDGE,"E64.right");Q1=makeQuery(id+"F18.imprint","IMPRINT",FACE,{"disambiguationData":[TD([[makeQuery(id+"F18.imprint","IMPRINT",EDGE,{"derivedFrom":subQ0}),1.0]])]});}
            extrude(context, id + "F22", {"entities" : qUnion([Q0, Q1]), "operationType" : NewBodyOperationType.REMOVE, "oppositeDirection" : true, "depth" : 2 * mm});
        }
        {
            var Q0;
            Q0=qCreatedBy(makeId("Top.planeOp"),FACE);
            var sketch = newSketch(context, id + "F23", { "sketchPlane" : qUnion([Q0])});
            skLineSegment(sketch, "E75", {"start": v(21, 19.9) * mm, "end": v(21, 10.4) * mm, "construction": true});
            skLineSegment(sketch, "E76", {"start": v(12.22, 0) * mm, "end": v(12.22, -5.06) * mm});
            skLineSegment(sketch, "E77", {"start": v(12.22, 0) * mm, "end": v(12.22, 1.5) * mm});
            skArc(sketch, "E78", {"start": v(14.47, 7.42) * mm, "mid": v(17.49, 10.4) * mm, "end": v(14.5, 13.4) * mm});
            skArc(sketch, "E79", {"start": v(6.7, 13.4) * mm, "mid": v(3.7, 10.4) * mm, "end": v(6.7, 7.4) * mm});
            skLineSegment(sketch, "E80", {"start": v(14.5, 13.4) * mm, "end": v(6.7, 13.4) * mm});
            skLineSegment(sketch, "E81", {"start": v(6.7, 7.4) * mm, "end": v(14.54, 7.42) * mm});
            skLineSegment(sketch, "E82", {"start": v(6, -5.57) * mm, "end": v(6, -16.85) * mm});
            skLineSegment(sketch, "E83", {"start": v(12.6, -16.85) * mm, "end": v(6, -16.85) * mm});
            skPoint(sketch, "E84.center.orphan", {"position": v(10.72, -16.85) * mm});
            skLineSegment(sketch, "E85", {"start": v(12.6, -5.57) * mm, "end": v(12.6, -16.85) * mm});
            skLineSegment(sketch, "E86", {"start": v(8.87, -5.06) * mm, "end": v(8.87, 1.5) * mm});
            skArc(sketch, "E87", {"start": v(12.22, 1.5) * mm, "mid": v(10.54, 3.17) * mm, "end": v(8.87, 1.5) * mm});
            skPoint(sketch, "E88.orphan", {"position": v(12.22, -16.85) * mm});
            skLineSegment(sketch, "E89", {"start": v(0, 0) * mm, "end": v(0, 19.9) * mm, "construction": true});
            skLineSegment(sketch, "E90", {"start": v(0, 19.9) * mm, "end": v(21, 19.9) * mm, "construction": true});
            skLineSegment(sketch, "E91", {"start": v(14.5, 10.4) * mm, "end": v(21, 10.4) * mm, "construction": true});
            skLineSegment(sketch, "E92", {"start": v(8.87, -5.06) * mm, "end": v(6, -5.06) * mm});
            skLineSegment(sketch, "E93", {"start": v(6, -5.06) * mm, "end": v(6, -5.57) * mm});
            skLineSegment(sketch, "E94", {"start": v(12.22, -5.06) * mm, "end": v(12.6, -5.06) * mm});
            skLineSegment(sketch, "E95", {"start": v(12.6, -5.06) * mm, "end": v(12.6, -5.57) * mm});
            skSolve(sketch);
        }
        {
            var Q0;
            Q0=qSketchRegion(id+"F23",true);
            extrude(context, id + "F24", {"entities" : qUnion([Q0]), "operationType" : NewBodyOperationType.REMOVE, "depth" : 25 * mm});
        }
        {
            var Q0;
            Q0=qCreatedBy(makeId("Top.planeOp"),FACE);
            var sketch = newSketch(context, id + "F25", { "sketchPlane" : qUnion([Q0])});
            skLineSegment(sketch, "E96", {"start": v(18.49, -17.16) * mm, "end": v(5.97, -17.16) * mm});
            skLineSegment(sketch, "E97", {"start": v(18.49, -16.86) * mm, "end": v(5.97, -16.86) * mm});
            skLineSegment(sketch, "E98", {"start": v(12.44, -31.08) * mm, "end": v(5.87, -31.08) * mm});
            skLineSegment(sketch, "E99", {"start": v(12.44, -30.78) * mm, "end": v(5.87, -30.78) * mm});
            skLineSegment(sketch, "E100.bottom", {"start": v(-33.84, 14.47) * mm, "end": v(-32.16, 14.47) * mm});
            skLineSegment(sketch, "E100.top", {"start": v(-33.84, 18.7) * mm, "end": v(-29.5, 18.7) * mm});
            skLineSegment(sketch, "E100.left", {"start": v(-33.84, 14.47) * mm, "end": v(-33.84, 18.7) * mm});
            skLineSegment(sketch, "E100.right", {"start": v(-29.5, 16.74) * mm, "end": v(-29.5, 18.7) * mm});
            skArc(sketch, "E101", {"start": v(-29.5, 16.74) * mm, "mid": v(-31.35, 16.22) * mm, "end": v(-32.16, 14.47) * mm});
            skLineSegment(sketch, "E102.bottom", {"start": v(-33.6, -31.08) * mm, "end": v(-33.6, -31.08) * mm});
            skLineSegment(sketch, "E102.top", {"start": v(-33.6, -34.81) * mm, "end": v(-31.03, -34.81) * mm});
            skLineSegment(sketch, "E102.left", {"start": v(-33.6, -31.08) * mm, "end": v(-33.6, -34.81) * mm});
            skLineSegment(sketch, "E102.right", {"start": v(-31.03, -31.08) * mm, "end": v(-31.03, -33.21) * mm});
            skLineSegment(sketch, "E103.bottom", {"start": v(-31.03, -34.81) * mm, "end": v(-28.95, -34.81) * mm});
            skLineSegment(sketch, "E103.top", {"start": v(-31.03, -33.21) * mm, "end": v(-28.95, -33.21) * mm});
            skLineSegment(sketch, "E103.right", {"start": v(-28.95, -34.81) * mm, "end": v(-28.95, -33.21) * mm});
            skPoint(sketch, "E104.end.orphan", {"position": v(-34.98, -31.08) * mm});
            skPoint(sketch, "E104.start.orphan", {"position": v(-34.98, -30.78) * mm});
            skLineSegment(sketch, "E105.bottom", {"start": v(16.87, -34.88) * mm, "end": v(19.69, -34.88) * mm});
            skLineSegment(sketch, "E105.top", {"start": v(16.87, -30.79) * mm, "end": v(19.69, -30.79) * mm});
            skLineSegment(sketch, "E105.left", {"start": v(16.87, -33.4) * mm, "end": v(16.87, -30.79) * mm});
            skLineSegment(sketch, "E105.right", {"start": v(19.69, -34.88) * mm, "end": v(19.69, -30.79) * mm});
            skLineSegment(sketch, "E106.bottom", {"start": v(16.87, -34.88) * mm, "end": v(14.73, -34.88) * mm});
            skLineSegment(sketch, "E106.top", {"start": v(16.87, -33.4) * mm, "end": v(14.73, -33.4) * mm});
            skLineSegment(sketch, "E106.right", {"start": v(14.73, -34.88) * mm, "end": v(14.73, -33.4) * mm});
            skLineSegment(sketch, "E107.top", {"start": v(-31.03, -30.09) * mm, "end": v(-33.6, -30.09) * mm});
            skLineSegment(sketch, "E107.left", {"start": v(-31.03, -31.08) * mm, "end": v(-31.03, -30.09) * mm});
            skLineSegment(sketch, "E107.right", {"start": v(-33.6, -31.08) * mm, "end": v(-33.6, -30.09) * mm});
            skLineSegment(sketch, "E108", {"start": v(5.87, -31.08) * mm, "end": v(5.87, -30.78) * mm});
            skPoint(sketch, "E109.end.orphan", {"position": v(-34.98, -17.16) * mm});
            skPoint(sketch, "E109.start.orphan", {"position": v(-34.98, -16.86) * mm});
            skLineSegment(sketch, "E110.trimOffspring", {"start": v(5.97, -17.16) * mm, "end": v(5.97, -16.86) * mm});
            skLineSegment(sketch, "E111.bottom", {"start": v(5.85, -23.4) * mm, "end": v(18.49, -23.4) * mm});
            skLineSegment(sketch, "E111.top", {"start": v(5.85, -23.7) * mm, "end": v(18.49, -23.7) * mm});
            skLineSegment(sketch, "E111.left", {"start": v(5.85, -23.4) * mm, "end": v(5.85, -23.7) * mm});
            skLineSegment(sketch, "E112", {"start": v(5.29, -31.08) * mm, "end": v(5.29, 2.03) * mm});
            skLineSegment(sketch, "E113", {"start": v(4.99, -31.08) * mm, "end": v(5.29, -31.08) * mm});
            skLineSegment(sketch, "E114", {"start": v(12.44, -30.78) * mm, "end": v(12.44, -31.08) * mm});
            skLineSegment(sketch, "E115", {"start": v(18.49, -16.86) * mm, "end": v(18.49, -17.16) * mm});
            skPoint(sketch, "E116.orphan", {"position": v(19.24, -17.16) * mm});
            skLineSegment(sketch, "E117.trimOffspring", {"start": v(18.49, -23.4) * mm, "end": v(18.49, -23.7) * mm});
            skPoint(sketch, "E118.orphan", {"position": v(19.24, -23.7) * mm});
            skLineSegment(sketch, "E119.trimOffspring", {"start": v(4.99, 2.03) * mm, "end": v(4.99, -31.08) * mm});
            skLineSegment(sketch, "E120", {"start": v(4.99, 2.03) * mm, "end": v(5.29, 2.03) * mm});
            skLineSegment(sketch, "E121.bottom", {"start": v(4.99, 2.73) * mm, "end": v(13.12, 2.73) * mm});
            skLineSegment(sketch, "E121.top", {"start": v(4.99, 6.24) * mm, "end": v(13.12, 6.24) * mm});
            skLineSegment(sketch, "E121.left", {"start": v(4.99, 2.73) * mm, "end": v(4.99, 6.24) * mm});
            skLineSegment(sketch, "E121.right", {"start": v(13.12, 2.73) * mm, "end": v(13.12, 6.24) * mm});
            skCircle(sketch, "E122", {"center": v(8.91, 3.9) * mm, "radius": 1.04 * mm});
            skPoint(sketch, "E122.first.point", {"position": v(8.9, 2.86) * mm});
            skPoint(sketch, "E122.second.point", {"position": v(8.95, 4.94) * mm});
            skPoint(sketch, "E122.third.point", {"position": v(9.95, 3.84) * mm});
            skSolve(sketch);
        }
        {
            var Q0;
            Q0=makeQuery(id+"F25.imprint","IMPRINT",FACE,{"disambiguationData":[TD([[makeQuery(id+"F25.imprint","IMPRINT",EDGE,{"derivedFrom":sQuery(id+"F25.wireOp",EDGE,"E96")}),-1.0]])]});
            var Q1;
            Q1=makeQuery(id+"F25.imprint","IMPRINT",FACE,{"disambiguationData":[TD([[makeQuery(id+"F25.imprint","IMPRINT",EDGE,{"derivedFrom":sQuery(id+"F25.wireOp",EDGE,"E98")}),-1.0]])]});
            var Q2;
            Q2=makeQuery(id+"F25.imprint","IMPRINT",FACE,{"disambiguationData":[TD([[makeQuery(id+"F25.imprint","IMPRINT",EDGE,{"derivedFrom":sQuery(id+"F25.wireOp",EDGE,"E100.bottom")}),1.0]])]});
            var Q3;
            Q3=makeQuery(id+"F25.imprint","IMPRINT",FACE,{"disambiguationData":[TD([[makeQuery(id+"F25.imprint","IMPRINT",EDGE,{"derivedFrom":sQuery(id+"F25.wireOp",EDGE,"E102.top")}),1.0]])]});
            var Q4;
            Q4=makeQuery(id+"F25.imprint","IMPRINT",FACE,{"disambiguationData":[TD([[makeQuery(id+"F25.imprint","IMPRINT",EDGE,{"derivedFrom":sQuery(id+"F25.wireOp",EDGE,"E111.bottom")}),-1.0]])]});
            var Q5;
            Q5=makeQuery(id+"F25.imprint","IMPRINT",FACE,{"disambiguationData":[TD([[makeQuery(id+"F25.imprint","IMPRINT",EDGE,{"derivedFrom":sQuery(id+"F25.wireOp",EDGE,"E112")}),1.0]])]});
            var Q6;
            Q6=makeQuery(id+"F25.imprint","IMPRINT",FACE,{"disambiguationData":[TD([[makeQuery(id+"F25.imprint","IMPRINT",EDGE,{"derivedFrom":sQuery(id+"F25.wireOp",EDGE,"E121.bottom")}),1.0]])]});
            extrude(context, id + "F26", {"entities" : qUnion([Q0, Q1, Q2, Q3, Q4, Q5, Q6]), "operationType" : NewBodyOperationType.ADD, "depth" : 7.5 * mm});
        }
        {
            var Q0;
            Q0=qCreatedBy(makeId("Top.planeOp"),FACE);
            var sketch = newSketch(context, id + "F27", { "sketchPlane" : qUnion([Q0])});
            skLineSegment(sketch, "E123", {"start": v(-14.06, 0.58) * mm, "end": v(-9.7, 0.57) * mm});
            skLineSegment(sketch, "E124", {"start": v(-8.04, -3.57) * mm, "end": v(-8.03, -3.84) * mm});
            skLineSegment(sketch, "E125", {"start": v(-8.03, -3.84) * mm, "end": v(-8.04, -13.15) * mm});
            skLineSegment(sketch, "E126", {"start": v(-8.04, -13.15) * mm, "end": v(-8.03, -13.22) * mm});
            skLineSegment(sketch, "E127", {"start": v(-8.03, -13.22) * mm, "end": v(-8.03, -13.28) * mm});
            skLineSegment(sketch, "E128", {"start": v(-8.03, -13.28) * mm, "end": v(-8.04, -13.35) * mm});
            skLineSegment(sketch, "E129", {"start": v(-8.04, -13.35) * mm, "end": v(-8.04, -13.42) * mm});
            skLineSegment(sketch, "E130", {"start": v(-8.04, -13.42) * mm, "end": v(-8.05, -13.48) * mm});
            skLineSegment(sketch, "E131", {"start": v(-8.05, -13.48) * mm, "end": v(-8.06, -13.55) * mm});
            skLineSegment(sketch, "E132", {"start": v(-8.06, -13.55) * mm, "end": v(-8.07, -13.61) * mm});
            skLineSegment(sketch, "E133", {"start": v(-8.07, -13.61) * mm, "end": v(-8.1, -13.68) * mm});
            skLineSegment(sketch, "E134", {"start": v(-8.1, -13.68) * mm, "end": v(-8.1, -13.74) * mm});
            skLineSegment(sketch, "E135", {"start": v(-8.1, -13.74) * mm, "end": v(-8.13, -13.8) * mm});
            skLineSegment(sketch, "E136", {"start": v(-8.13, -13.8) * mm, "end": v(-8.15, -13.86) * mm});
            skLineSegment(sketch, "E137", {"start": v(-8.15, -13.86) * mm, "end": v(-8.18, -13.93) * mm});
            skLineSegment(sketch, "E138", {"start": v(-8.18, -13.93) * mm, "end": v(-8.2, -13.99) * mm});
            skLineSegment(sketch, "E139", {"start": v(-8.2, -13.99) * mm, "end": v(-8.23, -14.05) * mm});
            skLineSegment(sketch, "E140", {"start": v(-8.23, -14.05) * mm, "end": v(-8.26, -14.1) * mm});
            skLineSegment(sketch, "E141", {"start": v(-8.26, -14.1) * mm, "end": v(-8.3, -14.16) * mm});
            skLineSegment(sketch, "E142", {"start": v(-8.3, -14.16) * mm, "end": v(-8.33, -14.22) * mm});
            skLineSegment(sketch, "E143", {"start": v(-8.33, -14.22) * mm, "end": v(-8.37, -14.27) * mm});
            skLineSegment(sketch, "E144", {"start": v(-8.37, -14.27) * mm, "end": v(-8.4, -14.32) * mm});
            skLineSegment(sketch, "E145", {"start": v(-8.4, -14.32) * mm, "end": v(-8.45, -14.37) * mm});
            skLineSegment(sketch, "E146", {"start": v(-8.45, -14.37) * mm, "end": v(-8.5, -14.42) * mm});
            skLineSegment(sketch, "E147", {"start": v(-8.5, -14.42) * mm, "end": v(-8.54, -14.47) * mm});
            skLineSegment(sketch, "E148", {"start": v(-8.54, -14.47) * mm, "end": v(-8.59, -14.52) * mm});
            skLineSegment(sketch, "E149", {"start": v(-8.59, -14.52) * mm, "end": v(-8.63, -14.56) * mm});
            skLineSegment(sketch, "E150", {"start": v(-8.63, -14.56) * mm, "end": v(-8.69, -14.6) * mm});
            skLineSegment(sketch, "E151", {"start": v(-8.69, -14.6) * mm, "end": v(-8.74, -14.64) * mm});
            skLineSegment(sketch, "E152", {"start": v(-8.74, -14.64) * mm, "end": v(-8.8, -14.68) * mm});
            skLineSegment(sketch, "E153", {"start": v(-8.8, -14.68) * mm, "end": v(-8.85, -14.72) * mm});
            skLineSegment(sketch, "E154", {"start": v(-8.85, -14.72) * mm, "end": v(-8.9, -14.75) * mm});
            skLineSegment(sketch, "E155", {"start": v(-8.9, -14.75) * mm, "end": v(-8.95, -14.77) * mm});
            skLineSegment(sketch, "E156", {"start": v(-8.95, -14.77) * mm, "end": v(-8.99, -14.8) * mm});
            skLineSegment(sketch, "E157", {"start": v(-8.99, -14.8) * mm, "end": v(-9.03, -14.81) * mm});
            skLineSegment(sketch, "E158", {"start": v(-9.03, -14.81) * mm, "end": v(-9.07, -14.83) * mm});
            skLineSegment(sketch, "E159", {"start": v(-9.07, -14.83) * mm, "end": v(-9.11, -14.85) * mm});
            skLineSegment(sketch, "E160", {"start": v(-9.11, -14.85) * mm, "end": v(-9.16, -14.86) * mm});
            skLineSegment(sketch, "E161", {"start": v(-9.16, -14.86) * mm, "end": v(-9.2, -14.88) * mm});
            skLineSegment(sketch, "E162", {"start": v(-9.2, -14.88) * mm, "end": v(-9.24, -14.9) * mm});
            skLineSegment(sketch, "E163", {"start": v(-9.24, -14.9) * mm, "end": v(-9.29, -14.9) * mm});
            skLineSegment(sketch, "E164", {"start": v(-9.29, -14.9) * mm, "end": v(-9.33, -14.91) * mm});
            skLineSegment(sketch, "E165", {"start": v(-9.33, -14.91) * mm, "end": v(-9.38, -14.92) * mm});
            skLineSegment(sketch, "E166", {"start": v(-9.38, -14.92) * mm, "end": v(-9.42, -14.93) * mm});
            skLineSegment(sketch, "E167", {"start": v(-9.42, -14.93) * mm, "end": v(-9.51, -14.94) * mm});
            skLineSegment(sketch, "E168", {"start": v(-9.51, -14.94) * mm, "end": v(-9.6, -14.96) * mm});
            skLineSegment(sketch, "E169", {"start": v(-9.6, -14.96) * mm, "end": v(-9.74, -14.97) * mm});
            skLineSegment(sketch, "E170", {"start": v(-9.74, -14.97) * mm, "end": v(-10.2, -14.98) * mm});
            skLineSegment(sketch, "E171", {"start": v(-10.2, -14.98) * mm, "end": v(-23.2, -14.97) * mm});
            skLineSegment(sketch, "E172", {"start": v(-23.2, -14.97) * mm, "end": v(-23.28, -14.97) * mm});
            skLineSegment(sketch, "E173", {"start": v(-23.28, -14.97) * mm, "end": v(-23.35, -14.97) * mm});
            skLineSegment(sketch, "E174", {"start": v(-23.35, -14.97) * mm, "end": v(-23.43, -14.97) * mm});
            skLineSegment(sketch, "E175", {"start": v(-23.43, -14.97) * mm, "end": v(-23.5, -14.96) * mm});
            skLineSegment(sketch, "E176", {"start": v(-23.5, -14.96) * mm, "end": v(-23.58, -14.94) * mm});
            skLineSegment(sketch, "E177", {"start": v(-23.58, -14.94) * mm, "end": v(-23.65, -14.93) * mm});
            skLineSegment(sketch, "E178", {"start": v(-23.65, -14.93) * mm, "end": v(-23.72, -14.9) * mm});
            skLineSegment(sketch, "E179", {"start": v(-23.72, -14.9) * mm, "end": v(-23.8, -14.89) * mm});
            skLineSegment(sketch, "E180", {"start": v(-23.8, -14.89) * mm, "end": v(-23.86, -14.86) * mm});
            skLineSegment(sketch, "E181", {"start": v(-23.86, -14.86) * mm, "end": v(-23.93, -14.83) * mm});
            skLineSegment(sketch, "E182", {"start": v(-23.93, -14.83) * mm, "end": v(-24, -14.8) * mm});
            skLineSegment(sketch, "E183", {"start": v(-24, -14.8) * mm, "end": v(-24.07, -14.77) * mm});
            skLineSegment(sketch, "E184", {"start": v(-24.07, -14.77) * mm, "end": v(-24.13, -14.73) * mm});
            skLineSegment(sketch, "E185", {"start": v(-24.13, -14.73) * mm, "end": v(-24.2, -14.7) * mm});
            skLineSegment(sketch, "E186", {"start": v(-24.2, -14.7) * mm, "end": v(-24.26, -14.65) * mm});
            skLineSegment(sketch, "E187", {"start": v(-24.26, -14.65) * mm, "end": v(-24.32, -14.6) * mm});
            skLineSegment(sketch, "E188", {"start": v(-24.32, -14.6) * mm, "end": v(-24.38, -14.56) * mm});
            skLineSegment(sketch, "E189", {"start": v(-24.38, -14.56) * mm, "end": v(-24.43, -14.51) * mm});
            skLineSegment(sketch, "E190", {"start": v(-24.43, -14.51) * mm, "end": v(-24.48, -14.46) * mm});
            skLineSegment(sketch, "E191", {"start": v(-24.48, -14.46) * mm, "end": v(-24.54, -14.4) * mm});
            skLineSegment(sketch, "E192", {"start": v(-24.54, -14.4) * mm, "end": v(-24.59, -14.35) * mm});
            skLineSegment(sketch, "E193", {"start": v(-24.59, -14.35) * mm, "end": v(-24.63, -14.3) * mm});
            skLineSegment(sketch, "E194", {"start": v(-24.63, -14.3) * mm, "end": v(-24.68, -14.23) * mm});
            skLineSegment(sketch, "E195", {"start": v(-24.68, -14.23) * mm, "end": v(-24.72, -14.17) * mm});
            skLineSegment(sketch, "E196", {"start": v(-24.72, -14.17) * mm, "end": v(-24.76, -14.1) * mm});
            skLineSegment(sketch, "E197", {"start": v(-24.76, -14.1) * mm, "end": v(-24.8, -14.04) * mm});
            skLineSegment(sketch, "E198", {"start": v(-24.8, -14.04) * mm, "end": v(-24.82, -13.97) * mm});
            skLineSegment(sketch, "E199", {"start": v(-24.82, -13.97) * mm, "end": v(-24.85, -13.9) * mm});
            skLineSegment(sketch, "E200", {"start": v(-24.85, -13.9) * mm, "end": v(-24.88, -13.83) * mm});
            skLineSegment(sketch, "E201", {"start": v(-24.88, -13.83) * mm, "end": v(-24.9, -13.76) * mm});
            skLineSegment(sketch, "E202", {"start": v(-24.9, -13.76) * mm, "end": v(-24.92, -13.66) * mm});
            skLineSegment(sketch, "E203", {"start": v(-24.92, -13.66) * mm, "end": v(-24.94, -13.55) * mm});
            skLineSegment(sketch, "E204", {"start": v(-24.94, -13.55) * mm, "end": v(-24.96, -13.38) * mm});
            skLineSegment(sketch, "E205", {"start": v(-24.96, -13.38) * mm, "end": v(-24.98, -12.8) * mm});
            skLineSegment(sketch, "E206", {"start": v(-24.98, -12.8) * mm, "end": v(-24.98, -3.92) * mm});
            skLineSegment(sketch, "E207", {"start": v(-24.98, -3.92) * mm, "end": v(-24.97, -3.38) * mm});
            skLineSegment(sketch, "E208", {"start": v(-24.97, -3.38) * mm, "end": v(-24.96, -3.24) * mm});
            skLineSegment(sketch, "E209", {"start": v(-24.96, -3.24) * mm, "end": v(-24.95, -3.15) * mm});
            skLineSegment(sketch, "E210", {"start": v(-24.95, -3.15) * mm, "end": v(-24.94, -3.1) * mm});
            skLineSegment(sketch, "E211", {"start": v(-24.94, -3.1) * mm, "end": v(-24.93, -3.06) * mm});
            skLineSegment(sketch, "E212", {"start": v(-24.93, -3.06) * mm, "end": v(-24.93, -3.02) * mm});
            skLineSegment(sketch, "E213", {"start": v(-24.93, -3.02) * mm, "end": v(-24.92, -2.97) * mm});
            skLineSegment(sketch, "E214", {"start": v(-24.92, -2.97) * mm, "end": v(-24.9, -2.93) * mm});
            skLineSegment(sketch, "E215", {"start": v(-24.9, -2.93) * mm, "end": v(-24.9, -2.88) * mm});
            skLineSegment(sketch, "E216", {"start": v(-24.9, -2.88) * mm, "end": v(-24.88, -2.84) * mm});
            skLineSegment(sketch, "E217", {"start": v(-24.88, -2.84) * mm, "end": v(-24.87, -2.8) * mm});
            skLineSegment(sketch, "E218", {"start": v(-24.87, -2.8) * mm, "end": v(-24.85, -2.76) * mm});
            skLineSegment(sketch, "E219", {"start": v(-24.85, -2.76) * mm, "end": v(-24.83, -2.71) * mm});
            skLineSegment(sketch, "E220", {"start": v(-24.83, -2.71) * mm, "end": v(-24.81, -2.67) * mm});
            skLineSegment(sketch, "E221", {"start": v(-24.81, -2.67) * mm, "end": v(-24.8, -2.63) * mm});
            skLineSegment(sketch, "E222", {"start": v(-24.8, -2.63) * mm, "end": v(-24.77, -2.58) * mm});
            skLineSegment(sketch, "E223", {"start": v(-24.77, -2.58) * mm, "end": v(-24.74, -2.53) * mm});
            skLineSegment(sketch, "E224", {"start": v(-24.74, -2.53) * mm, "end": v(-24.7, -2.48) * mm});
            skLineSegment(sketch, "E225", {"start": v(-24.7, -2.48) * mm, "end": v(-24.68, -2.43) * mm});
            skLineSegment(sketch, "E226", {"start": v(-24.68, -2.43) * mm, "end": v(-24.64, -2.38) * mm});
            skLineSegment(sketch, "E227", {"start": v(-24.64, -2.38) * mm, "end": v(-24.6, -2.34) * mm});
            skLineSegment(sketch, "E228", {"start": v(-24.6, -2.34) * mm, "end": v(-24.57, -2.3) * mm});
            skLineSegment(sketch, "E229", {"start": v(-24.57, -2.3) * mm, "end": v(-24.53, -2.25) * mm});
            skLineSegment(sketch, "E230", {"start": v(-24.53, -2.25) * mm, "end": v(-24.5, -2.2) * mm});
            skLineSegment(sketch, "E231", {"start": v(-24.5, -2.2) * mm, "end": v(-24.45, -2.16) * mm});
            skLineSegment(sketch, "E232", {"start": v(-24.45, -2.16) * mm, "end": v(-24.41, -2.12) * mm});
            skLineSegment(sketch, "E233", {"start": v(-24.41, -2.12) * mm, "end": v(-24.37, -2.08) * mm});
            skLineSegment(sketch, "E234", {"start": v(-24.37, -2.08) * mm, "end": v(-24.32, -2.05) * mm});
            skLineSegment(sketch, "E235", {"start": v(-24.32, -2.05) * mm, "end": v(-24.28, -2.01) * mm});
            skLineSegment(sketch, "E236", {"start": v(-24.28, -2.01) * mm, "end": v(-24.23, -1.98) * mm});
            skLineSegment(sketch, "E237", {"start": v(-24.23, -1.98) * mm, "end": v(-24.18, -1.94) * mm});
            skLineSegment(sketch, "E238", {"start": v(-24.18, -1.94) * mm, "end": v(-24.13, -1.91) * mm});
            skLineSegment(sketch, "E239", {"start": v(-24.13, -1.91) * mm, "end": v(-24.08, -1.88) * mm});
            skLineSegment(sketch, "E240", {"start": v(-24.08, -1.88) * mm, "end": v(-24.03, -1.86) * mm});
            skLineSegment(sketch, "E241", {"start": v(-24.03, -1.86) * mm, "end": v(-23.98, -1.83) * mm});
            skLineSegment(sketch, "E242", {"start": v(-23.98, -1.83) * mm, "end": v(-23.93, -1.8) * mm});
            skLineSegment(sketch, "E243", {"start": v(-23.93, -1.8) * mm, "end": v(-23.87, -1.79) * mm});
            skLineSegment(sketch, "E244", {"start": v(-23.87, -1.79) * mm, "end": v(-23.82, -1.77) * mm});
            skLineSegment(sketch, "E245", {"start": v(-23.82, -1.77) * mm, "end": v(-23.76, -1.75) * mm});
            skLineSegment(sketch, "E246", {"start": v(-23.76, -1.75) * mm, "end": v(-23.7, -1.73) * mm});
            skLineSegment(sketch, "E247", {"start": v(-23.7, -1.73) * mm, "end": v(-23.65, -1.72) * mm});
            skLineSegment(sketch, "E248", {"start": v(-23.65, -1.72) * mm, "end": v(-23.6, -1.71) * mm});
            skLineSegment(sketch, "E249", {"start": v(-23.6, -1.71) * mm, "end": v(-23.53, -1.7) * mm});
            skLineSegment(sketch, "E250", {"start": v(-23.53, -1.7) * mm, "end": v(-23.48, -1.7) * mm});
            skLineSegment(sketch, "E251", {"start": v(-23.48, -1.7) * mm, "end": v(-23.32, -1.69) * mm});
            skLineSegment(sketch, "E252", {"start": v(-23.32, -1.69) * mm, "end": v(-23.17, -1.68) * mm});
            skLineSegment(sketch, "E253", {"start": v(-23.17, -1.68) * mm, "end": v(-22.95, -1.67) * mm});
            skLineSegment(sketch, "E254", {"start": v(-22.95, -1.67) * mm, "end": v(-21.9, -1.67) * mm});
            skLineSegment(sketch, "E255", {"start": v(-21.9, -1.67) * mm, "end": v(-21.52, -1.67) * mm});
            skLineSegment(sketch, "E256", {"start": v(-21.52, -1.67) * mm, "end": v(-21.3, -1.66) * mm});
            skLineSegment(sketch, "E257", {"start": v(-21.3, -1.66) * mm, "end": v(-21.2, -1.64) * mm});
            skLineSegment(sketch, "E258", {"start": v(-21.2, -1.64) * mm, "end": v(-20.86, -1.5) * mm});
            skLineSegment(sketch, "E259", {"start": v(-20.86, -1.5) * mm, "end": v(-17.7, 0.02) * mm});
            skLineSegment(sketch, "E260", {"start": v(-17.7, 0.02) * mm, "end": v(-17.01, 0.36) * mm});
            skLineSegment(sketch, "E261", {"start": v(-15.75, 0.24) * mm, "end": v(-14.06, -0.59) * mm});
            skLineSegment(sketch, "E262", {"start": v(-14.06, -0.59) * mm, "end": v(-14.06, 0.58) * mm});
            skLineSegment(sketch, "E263", {"start": v(-13.15, -0.33) * mm, "end": v(-13.15, -2.1) * mm});
            skLineSegment(sketch, "E264", {"start": v(-13.15, -2.1) * mm, "end": v(-13.26, -2.06) * mm});
            skLineSegment(sketch, "E265", {"start": v(-13.26, -2.06) * mm, "end": v(-13.9, -1.75) * mm});
            skLineSegment(sketch, "E266", {"start": v(-16.83, -0.6) * mm, "end": v(-17.05, -0.71) * mm});
            skLineSegment(sketch, "E267", {"start": v(-17.05, -0.71) * mm, "end": v(-17.27, -0.83) * mm});
            skLineSegment(sketch, "E268", {"start": v(-17.27, -0.83) * mm, "end": v(-18.4, -1.4) * mm});
            skLineSegment(sketch, "E269", {"start": v(-18.4, -1.4) * mm, "end": v(-22.7, -3.51) * mm});
            skLineSegment(sketch, "E270", {"start": v(-22.7, -3.51) * mm, "end": v(-23.6, -3.97) * mm});
            skLineSegment(sketch, "E271", {"start": v(-23.6, -3.97) * mm, "end": v(-23.64, -4) * mm});
            skLineSegment(sketch, "E272", {"start": v(-23.64, -4) * mm, "end": v(-23.69, -4.02) * mm});
            skLineSegment(sketch, "E273", {"start": v(-23.69, -4.02) * mm, "end": v(-23.73, -4.05) * mm});
            skLineSegment(sketch, "E274", {"start": v(-23.73, -4.05) * mm, "end": v(-23.76, -4.08) * mm});
            skLineSegment(sketch, "E275", {"start": v(-23.76, -4.08) * mm, "end": v(-23.79, -4.1) * mm});
            skLineSegment(sketch, "E276", {"start": v(-23.79, -4.1) * mm, "end": v(-23.8, -4.13) * mm});
            skLineSegment(sketch, "E277", {"start": v(-23.8, -4.13) * mm, "end": v(-23.82, -4.15) * mm});
            skLineSegment(sketch, "E278", {"start": v(-23.82, -4.15) * mm, "end": v(-23.83, -4.16) * mm});
            skLineSegment(sketch, "E279", {"start": v(-23.83, -4.16) * mm, "end": v(-23.83, -4.18) * mm});
            skLineSegment(sketch, "E280", {"start": v(-23.83, -4.18) * mm, "end": v(-23.84, -4.2) * mm});
            skLineSegment(sketch, "E281", {"start": v(-23.84, -4.2) * mm, "end": v(-23.85, -4.21) * mm});
            skLineSegment(sketch, "E282", {"start": v(-23.85, -4.21) * mm, "end": v(-23.85, -4.23) * mm});
            skLineSegment(sketch, "E283", {"start": v(-23.85, -4.23) * mm, "end": v(-23.85, -4.25) * mm});
            skLineSegment(sketch, "E284", {"start": v(-23.85, -4.25) * mm, "end": v(-23.86, -4.27) * mm});
            skLineSegment(sketch, "E285", {"start": v(-23.86, -4.27) * mm, "end": v(-23.86, -4.29) * mm});
            skLineSegment(sketch, "E286", {"start": v(-23.86, -4.29) * mm, "end": v(-23.86, -4.3) * mm});
            skLineSegment(sketch, "E287", {"start": v(-23.86, -4.3) * mm, "end": v(-23.85, -4.32) * mm});
            skLineSegment(sketch, "E288", {"start": v(-23.85, -4.32) * mm, "end": v(-23.85, -4.34) * mm});
            skLineSegment(sketch, "E289", {"start": v(-23.85, -4.34) * mm, "end": v(-23.84, -4.36) * mm});
            skLineSegment(sketch, "E290", {"start": v(-23.84, -4.36) * mm, "end": v(-23.84, -4.38) * mm});
            skLineSegment(sketch, "E291", {"start": v(-23.84, -4.38) * mm, "end": v(-23.83, -4.4) * mm});
            skLineSegment(sketch, "E292", {"start": v(-23.83, -4.4) * mm, "end": v(-23.82, -4.42) * mm});
            skLineSegment(sketch, "E293", {"start": v(-23.82, -4.42) * mm, "end": v(-23.81, -4.44) * mm});
            skLineSegment(sketch, "E294", {"start": v(-23.81, -4.44) * mm, "end": v(-23.8, -4.45) * mm});
            skLineSegment(sketch, "E295", {"start": v(-23.8, -4.45) * mm, "end": v(-23.8, -4.47) * mm});
            skLineSegment(sketch, "E296", {"start": v(-23.8, -4.47) * mm, "end": v(-23.78, -4.48) * mm});
            skLineSegment(sketch, "E297", {"start": v(-23.78, -4.48) * mm, "end": v(-23.76, -4.5) * mm});
            skLineSegment(sketch, "E298", {"start": v(-23.76, -4.5) * mm, "end": v(-23.73, -4.53) * mm});
            skLineSegment(sketch, "E299", {"start": v(-23.73, -4.53) * mm, "end": v(-23.7, -4.55) * mm});
            skLineSegment(sketch, "E300", {"start": v(-23.7, -4.55) * mm, "end": v(-23.58, -4.62) * mm});
            skLineSegment(sketch, "E301", {"start": v(-23.58, -4.62) * mm, "end": v(-23.42, -4.7) * mm});
            skLineSegment(sketch, "E302", {"start": v(-23.42, -4.7) * mm, "end": v(-19.6, -6.6) * mm});
            skLineSegment(sketch, "E303", {"start": v(-19.6, -6.6) * mm, "end": v(-18.6, -7.09) * mm});
            skLineSegment(sketch, "E304", {"start": v(-18.6, -7.09) * mm, "end": v(-17.5, -7.65) * mm});
            skLineSegment(sketch, "E305", {"start": v(-17.5, -7.65) * mm, "end": v(-16.7, -8.03) * mm});
            skLineSegment(sketch, "E306", {"start": v(-16.7, -8.03) * mm, "end": v(-16.68, -8.04) * mm});
            skLineSegment(sketch, "E307", {"start": v(-16.68, -8.04) * mm, "end": v(-16.66, -8.05) * mm});
            skLineSegment(sketch, "E308", {"start": v(-16.66, -8.05) * mm, "end": v(-16.64, -8.06) * mm});
            skLineSegment(sketch, "E309", {"start": v(-16.64, -8.06) * mm, "end": v(-16.62, -8.06) * mm});
            skLineSegment(sketch, "E310", {"start": v(-16.62, -8.06) * mm, "end": v(-16.6, -8.07) * mm});
            skLineSegment(sketch, "E311", {"start": v(-16.6, -8.07) * mm, "end": v(-16.58, -8.07) * mm});
            skLineSegment(sketch, "E312", {"start": v(-16.58, -8.07) * mm, "end": v(-16.56, -8.07) * mm});
            skLineSegment(sketch, "E313", {"start": v(-16.56, -8.07) * mm, "end": v(-16.54, -8.07) * mm});
            skLineSegment(sketch, "E314", {"start": v(-16.54, -8.07) * mm, "end": v(-16.52, -8.08) * mm});
            skLineSegment(sketch, "E315", {"start": v(-16.52, -8.08) * mm, "end": v(-16.48, -8.07) * mm});
            skLineSegment(sketch, "E316", {"start": v(-16.48, -8.07) * mm, "end": v(-16.44, -8.07) * mm});
            skLineSegment(sketch, "E317", {"start": v(-16.44, -8.07) * mm, "end": v(-16.4, -8.06) * mm});
            skLineSegment(sketch, "E318", {"start": v(-16.4, -8.06) * mm, "end": v(-16.32, -8.04) * mm});
            skLineSegment(sketch, "E319", {"start": v(-16.32, -8.04) * mm, "end": v(-16.14, -7.96) * mm});
            skLineSegment(sketch, "E320", {"start": v(-16.14, -7.96) * mm, "end": v(-13.76, -6.78) * mm});
            skLineSegment(sketch, "E321", {"start": v(-13.76, -6.78) * mm, "end": v(-9.85, -4.84) * mm});
            skLineSegment(sketch, "E322", {"start": v(-9.4, -3.99) * mm, "end": v(-9.57, -3.89) * mm});
            skLineSegment(sketch, "E323", {"start": v(-9.57, -3.89) * mm, "end": v(-10.59, -3.4) * mm});
            skLineSegment(sketch, "E324", {"start": v(-10.59, -3.4) * mm, "end": v(-10.6, -0.33) * mm});
            skLineSegment(sketch, "E325", {"start": v(-10.6, -0.33) * mm, "end": v(-13.15, -0.33) * mm});
            skLineSegment(sketch, "E326", {"start": v(-26.34, -4.98) * mm, "end": v(-25.3, -4.97) * mm});
            skLineSegment(sketch, "E327", {"start": v(-25.3, -4.97) * mm, "end": v(-25.28, -6.53) * mm});
            skLineSegment(sketch, "E328", {"start": v(-25.28, -6.53) * mm, "end": v(-26.11, -6.52) * mm});
            skLineSegment(sketch, "E329", {"start": v(-26.11, -6.52) * mm, "end": v(-26.27, -6.5) * mm});
            skLineSegment(sketch, "E330", {"start": v(-26.27, -6.5) * mm, "end": v(-26.38, -6.49) * mm});
            skLineSegment(sketch, "E331", {"start": v(-26.38, -6.49) * mm, "end": v(-26.4, -6.47) * mm});
            skLineSegment(sketch, "E332", {"start": v(-26.4, -6.47) * mm, "end": v(-26.43, -6.45) * mm});
            skLineSegment(sketch, "E333", {"start": v(-26.43, -6.45) * mm, "end": v(-26.45, -6.43) * mm});
            skLineSegment(sketch, "E334", {"start": v(-26.45, -6.43) * mm, "end": v(-26.47, -6.41) * mm});
            skLineSegment(sketch, "E335", {"start": v(-26.47, -6.41) * mm, "end": v(-26.49, -6.39) * mm});
            skLineSegment(sketch, "E336", {"start": v(-26.49, -6.39) * mm, "end": v(-26.5, -6.37) * mm});
            skLineSegment(sketch, "E337", {"start": v(-26.5, -6.37) * mm, "end": v(-26.52, -6.34) * mm});
            skLineSegment(sketch, "E338", {"start": v(-26.52, -6.34) * mm, "end": v(-26.54, -6.32) * mm});
            skLineSegment(sketch, "E339", {"start": v(-26.54, -6.32) * mm, "end": v(-26.55, -6.29) * mm});
            skLineSegment(sketch, "E340", {"start": v(-26.55, -6.29) * mm, "end": v(-26.56, -6.26) * mm});
            skLineSegment(sketch, "E341", {"start": v(-26.56, -6.26) * mm, "end": v(-26.57, -6.23) * mm});
            skLineSegment(sketch, "E342", {"start": v(-26.57, -6.23) * mm, "end": v(-26.58, -6.2) * mm});
            skLineSegment(sketch, "E343", {"start": v(-26.58, -6.2) * mm, "end": v(-26.59, -6.18) * mm});
            skLineSegment(sketch, "E344", {"start": v(-26.59, -6.18) * mm, "end": v(-26.6, -6.15) * mm});
            skLineSegment(sketch, "E345", {"start": v(-26.6, -6.15) * mm, "end": v(-26.6, -6.09) * mm});
            skLineSegment(sketch, "E346", {"start": v(-26.6, -6.09) * mm, "end": v(-26.62, -6.03) * mm});
            skLineSegment(sketch, "E347", {"start": v(-26.62, -6.03) * mm, "end": v(-26.62, -5.9) * mm});
            skLineSegment(sketch, "E348", {"start": v(-26.62, -5.9) * mm, "end": v(-26.63, -5.75) * mm});
            skLineSegment(sketch, "E349", {"start": v(-26.63, -5.75) * mm, "end": v(-26.63, -5.7) * mm});
            skLineSegment(sketch, "E350", {"start": v(-26.63, -5.7) * mm, "end": v(-26.63, -5.62) * mm});
            skLineSegment(sketch, "E351", {"start": v(-26.63, -5.62) * mm, "end": v(-26.62, -5.5) * mm});
            skLineSegment(sketch, "E352", {"start": v(-26.62, -5.5) * mm, "end": v(-26.6, -5.42) * mm});
            skLineSegment(sketch, "E353", {"start": v(-26.6, -5.42) * mm, "end": v(-26.6, -5.36) * mm});
            skLineSegment(sketch, "E354", {"start": v(-26.6, -5.36) * mm, "end": v(-26.58, -5.3) * mm});
            skLineSegment(sketch, "E355", {"start": v(-26.58, -5.3) * mm, "end": v(-26.58, -5.28) * mm});
            skLineSegment(sketch, "E356", {"start": v(-26.58, -5.28) * mm, "end": v(-26.57, -5.25) * mm});
            skLineSegment(sketch, "E357", {"start": v(-26.57, -5.25) * mm, "end": v(-26.56, -5.23) * mm});
            skLineSegment(sketch, "E358", {"start": v(-26.56, -5.23) * mm, "end": v(-26.55, -5.2) * mm});
            skLineSegment(sketch, "E359", {"start": v(-26.55, -5.2) * mm, "end": v(-26.53, -5.18) * mm});
            skLineSegment(sketch, "E360", {"start": v(-26.53, -5.18) * mm, "end": v(-26.52, -5.15) * mm});
            skLineSegment(sketch, "E361", {"start": v(-26.52, -5.15) * mm, "end": v(-26.5, -5.13) * mm});
            skLineSegment(sketch, "E362", {"start": v(-26.5, -5.13) * mm, "end": v(-26.5, -5.1) * mm});
            skLineSegment(sketch, "E363", {"start": v(-26.5, -5.1) * mm, "end": v(-26.47, -5.09) * mm});
            skLineSegment(sketch, "E364", {"start": v(-26.47, -5.09) * mm, "end": v(-26.46, -5.07) * mm});
            skLineSegment(sketch, "E365", {"start": v(-26.46, -5.07) * mm, "end": v(-26.44, -5.05) * mm});
            skLineSegment(sketch, "E366", {"start": v(-26.44, -5.05) * mm, "end": v(-26.42, -5.03) * mm});
            skLineSegment(sketch, "E367", {"start": v(-26.42, -5.03) * mm, "end": v(-26.4, -5.01) * mm});
            skLineSegment(sketch, "E368", {"start": v(-26.4, -5.01) * mm, "end": v(-26.37, -5) * mm});
            skLineSegment(sketch, "E369", {"start": v(-26.37, -5) * mm, "end": v(-26.34, -4.98) * mm});
            skLineSegment(sketch, "E370", {"start": v(-7.72, -4.97) * mm, "end": v(-7.68, -4.98) * mm});
            skLineSegment(sketch, "E371", {"start": v(-7.68, -4.98) * mm, "end": v(-7.64, -4.98) * mm});
            skLineSegment(sketch, "E372", {"start": v(-7.64, -4.98) * mm, "end": v(-7.6, -4.98) * mm});
            skLineSegment(sketch, "E373", {"start": v(-7.6, -4.98) * mm, "end": v(-7.55, -4.98) * mm});
            skLineSegment(sketch, "E374", {"start": v(-7.55, -4.98) * mm, "end": v(-7.5, -4.98) * mm});
            skLineSegment(sketch, "E375", {"start": v(-7.5, -4.98) * mm, "end": v(-7.41, -4.97) * mm});
            skLineSegment(sketch, "E376", {"start": v(-7.41, -4.97) * mm, "end": v(-7.13, -4.95) * mm});
            skLineSegment(sketch, "E377", {"start": v(-7.13, -4.95) * mm, "end": v(-7.09, -4.94) * mm});
            skLineSegment(sketch, "E378", {"start": v(-7.09, -4.94) * mm, "end": v(-7.04, -4.94) * mm});
            skLineSegment(sketch, "E379", {"start": v(-7.04, -4.94) * mm, "end": v(-7, -4.94) * mm});
            skLineSegment(sketch, "E380", {"start": v(-7, -4.94) * mm, "end": v(-6.95, -4.94) * mm});
            skLineSegment(sketch, "E381", {"start": v(-6.95, -4.94) * mm, "end": v(-6.9, -4.94) * mm});
            skLineSegment(sketch, "E382", {"start": v(-6.9, -4.94) * mm, "end": v(-6.86, -4.95) * mm});
            skLineSegment(sketch, "E383", {"start": v(-6.86, -4.95) * mm, "end": v(-6.82, -4.95) * mm});
            skLineSegment(sketch, "E384", {"start": v(-6.82, -4.95) * mm, "end": v(-6.78, -4.96) * mm});
            skLineSegment(sketch, "E385", {"start": v(-6.78, -4.96) * mm, "end": v(-6.74, -4.97) * mm});
            skLineSegment(sketch, "E386", {"start": v(-6.74, -4.97) * mm, "end": v(-6.7, -4.99) * mm});
            skLineSegment(sketch, "E387", {"start": v(-6.7, -4.99) * mm, "end": v(-6.66, -5) * mm});
            skLineSegment(sketch, "E388", {"start": v(-6.66, -5) * mm, "end": v(-6.62, -5.03) * mm});
            skLineSegment(sketch, "E389", {"start": v(-6.62, -5.03) * mm, "end": v(-6.58, -5.05) * mm});
            skLineSegment(sketch, "E390", {"start": v(-6.58, -5.05) * mm, "end": v(-6.55, -5.08) * mm});
            skLineSegment(sketch, "E391", {"start": v(-6.55, -5.08) * mm, "end": v(-6.52, -5.1) * mm});
            skLineSegment(sketch, "E392", {"start": v(-6.52, -5.1) * mm, "end": v(-6.48, -5.14) * mm});
            skLineSegment(sketch, "E393", {"start": v(-6.48, -5.14) * mm, "end": v(-6.47, -5.18) * mm});
            skLineSegment(sketch, "E394", {"start": v(-6.47, -5.18) * mm, "end": v(-6.46, -5.21) * mm});
            skLineSegment(sketch, "E395", {"start": v(-6.46, -5.21) * mm, "end": v(-6.45, -5.24) * mm});
            skLineSegment(sketch, "E396", {"start": v(-6.45, -5.24) * mm, "end": v(-6.43, -5.31) * mm});
            skLineSegment(sketch, "E397", {"start": v(-6.43, -5.31) * mm, "end": v(-6.41, -5.38) * mm});
            skLineSegment(sketch, "E398", {"start": v(-6.41, -5.38) * mm, "end": v(-6.4, -5.45) * mm});
            skLineSegment(sketch, "E399", {"start": v(-6.4, -5.45) * mm, "end": v(-6.4, -5.52) * mm});
            skLineSegment(sketch, "E400", {"start": v(-6.4, -5.52) * mm, "end": v(-6.39, -5.59) * mm});
            skLineSegment(sketch, "E401", {"start": v(-6.39, -5.59) * mm, "end": v(-6.38, -5.7) * mm});
            skLineSegment(sketch, "E402", {"start": v(-6.38, -5.7) * mm, "end": v(-6.39, -5.83) * mm});
            skLineSegment(sketch, "E403", {"start": v(-6.39, -5.83) * mm, "end": v(-6.4, -6.08) * mm});
            skLineSegment(sketch, "E404", {"start": v(-6.4, -6.08) * mm, "end": v(-6.42, -6.15) * mm});
            skLineSegment(sketch, "E405", {"start": v(-6.42, -6.15) * mm, "end": v(-6.47, -6.3) * mm});
            skLineSegment(sketch, "E406", {"start": v(-6.47, -6.3) * mm, "end": v(-6.5, -6.36) * mm});
            skLineSegment(sketch, "E407", {"start": v(-6.5, -6.36) * mm, "end": v(-6.53, -6.4) * mm});
            skLineSegment(sketch, "E408", {"start": v(-6.53, -6.4) * mm, "end": v(-6.56, -6.43) * mm});
            skLineSegment(sketch, "E409", {"start": v(-6.56, -6.43) * mm, "end": v(-6.59, -6.46) * mm});
            skLineSegment(sketch, "E410", {"start": v(-6.59, -6.46) * mm, "end": v(-6.61, -6.47) * mm});
            skLineSegment(sketch, "E411", {"start": v(-6.61, -6.47) * mm, "end": v(-6.64, -6.49) * mm});
            skLineSegment(sketch, "E412", {"start": v(-6.64, -6.49) * mm, "end": v(-6.67, -6.5) * mm});
            skLineSegment(sketch, "E413", {"start": v(-6.67, -6.5) * mm, "end": v(-7.74, -6.53) * mm});
            skLineSegment(sketch, "E414", {"start": v(-7.74, -6.53) * mm, "end": v(-7.72, -4.97) * mm});
            skLineSegment(sketch, "E415", {"start": v(-26.35, -7.32) * mm, "end": v(-25.28, -7.3) * mm});
            skLineSegment(sketch, "E416", {"start": v(-25.28, -7.3) * mm, "end": v(-25.28, -8.87) * mm});
            skLineSegment(sketch, "E417", {"start": v(-25.28, -8.87) * mm, "end": v(-26.35, -8.85) * mm});
            skLineSegment(sketch, "E418", {"start": v(-26.35, -8.85) * mm, "end": v(-26.5, -8.7) * mm});
            skLineSegment(sketch, "E419", {"start": v(-26.5, -8.7) * mm, "end": v(-26.55, -8.62) * mm});
            skLineSegment(sketch, "E420", {"start": v(-26.55, -8.62) * mm, "end": v(-26.57, -8.57) * mm});
            skLineSegment(sketch, "E421", {"start": v(-26.57, -8.57) * mm, "end": v(-26.6, -8.52) * mm});
            skLineSegment(sketch, "E422", {"start": v(-26.6, -8.52) * mm, "end": v(-26.6, -8.47) * mm});
            skLineSegment(sketch, "E423", {"start": v(-26.6, -8.47) * mm, "end": v(-26.6, -8.45) * mm});
            skLineSegment(sketch, "E424", {"start": v(-26.6, -8.45) * mm, "end": v(-26.61, -8.37) * mm});
            skLineSegment(sketch, "E425", {"start": v(-26.61, -8.37) * mm, "end": v(-26.63, -8.2) * mm});
            skLineSegment(sketch, "E426", {"start": v(-26.63, -8.2) * mm, "end": v(-26.63, -8.08) * mm});
            skLineSegment(sketch, "E427", {"start": v(-26.63, -8.08) * mm, "end": v(-26.64, -8) * mm});
            skLineSegment(sketch, "E428", {"start": v(-26.64, -8) * mm, "end": v(-26.64, -7.95) * mm});
            skLineSegment(sketch, "E429", {"start": v(-26.64, -7.95) * mm, "end": v(-26.63, -7.9) * mm});
            skLineSegment(sketch, "E430", {"start": v(-26.63, -7.9) * mm, "end": v(-26.63, -7.86) * mm});
            skLineSegment(sketch, "E431", {"start": v(-26.63, -7.86) * mm, "end": v(-26.63, -7.82) * mm});
            skLineSegment(sketch, "E432", {"start": v(-26.63, -7.82) * mm, "end": v(-26.62, -7.78) * mm});
            skLineSegment(sketch, "E433", {"start": v(-26.62, -7.78) * mm, "end": v(-26.61, -7.74) * mm});
            skLineSegment(sketch, "E434", {"start": v(-26.61, -7.74) * mm, "end": v(-26.6, -7.7) * mm});
            skLineSegment(sketch, "E435", {"start": v(-26.6, -7.7) * mm, "end": v(-26.6, -7.66) * mm});
            skLineSegment(sketch, "E436", {"start": v(-26.6, -7.66) * mm, "end": v(-26.58, -7.62) * mm});
            skLineSegment(sketch, "E437", {"start": v(-26.58, -7.62) * mm, "end": v(-26.56, -7.58) * mm});
            skLineSegment(sketch, "E438", {"start": v(-26.56, -7.58) * mm, "end": v(-26.55, -7.54) * mm});
            skLineSegment(sketch, "E439", {"start": v(-26.55, -7.54) * mm, "end": v(-26.53, -7.5) * mm});
            skLineSegment(sketch, "E440", {"start": v(-26.53, -7.5) * mm, "end": v(-26.5, -7.47) * mm});
            skLineSegment(sketch, "E441", {"start": v(-26.5, -7.47) * mm, "end": v(-26.48, -7.44) * mm});
            skLineSegment(sketch, "E442", {"start": v(-26.48, -7.44) * mm, "end": v(-26.45, -7.4) * mm});
            skLineSegment(sketch, "E443", {"start": v(-26.45, -7.4) * mm, "end": v(-26.42, -7.38) * mm});
            skLineSegment(sketch, "E444", {"start": v(-26.42, -7.38) * mm, "end": v(-26.39, -7.35) * mm});
            skLineSegment(sketch, "E445", {"start": v(-26.39, -7.35) * mm, "end": v(-26.35, -7.32) * mm});
            skLineSegment(sketch, "E446", {"start": v(-7.73, -7.3) * mm, "end": v(-6.66, -7.32) * mm});
            skLineSegment(sketch, "E447", {"start": v(-6.66, -7.32) * mm, "end": v(-6.53, -7.44) * mm});
            skLineSegment(sketch, "E448", {"start": v(-6.53, -7.44) * mm, "end": v(-6.47, -7.53) * mm});
            skLineSegment(sketch, "E449", {"start": v(-6.47, -7.53) * mm, "end": v(-6.44, -7.58) * mm});
            skLineSegment(sketch, "E450", {"start": v(-6.44, -7.58) * mm, "end": v(-6.43, -7.63) * mm});
            skLineSegment(sketch, "E451", {"start": v(-6.43, -7.63) * mm, "end": v(-6.41, -7.68) * mm});
            skLineSegment(sketch, "E452", {"start": v(-6.41, -7.68) * mm, "end": v(-6.4, -7.7) * mm});
            skLineSegment(sketch, "E453", {"start": v(-6.4, -7.7) * mm, "end": v(-6.4, -7.79) * mm});
            skLineSegment(sketch, "E454", {"start": v(-6.4, -7.79) * mm, "end": v(-6.39, -7.96) * mm});
            skLineSegment(sketch, "E455", {"start": v(-6.39, -7.96) * mm, "end": v(-6.38, -8.09) * mm});
            skLineSegment(sketch, "E456", {"start": v(-6.38, -8.09) * mm, "end": v(-6.38, -8.17) * mm});
            skLineSegment(sketch, "E457", {"start": v(-6.38, -8.17) * mm, "end": v(-6.38, -8.22) * mm});
            skLineSegment(sketch, "E458", {"start": v(-6.38, -8.22) * mm, "end": v(-6.38, -8.26) * mm});
            skLineSegment(sketch, "E459", {"start": v(-6.38, -8.26) * mm, "end": v(-6.38, -8.3) * mm});
            skLineSegment(sketch, "E460", {"start": v(-6.38, -8.3) * mm, "end": v(-6.39, -8.34) * mm});
            skLineSegment(sketch, "E461", {"start": v(-6.39, -8.34) * mm, "end": v(-6.4, -8.39) * mm});
            skLineSegment(sketch, "E462", {"start": v(-6.4, -8.39) * mm, "end": v(-6.4, -8.43) * mm});
            skLineSegment(sketch, "E463", {"start": v(-6.4, -8.43) * mm, "end": v(-6.4, -8.47) * mm});
            skLineSegment(sketch, "E464", {"start": v(-6.4, -8.47) * mm, "end": v(-6.42, -8.5) * mm});
            skLineSegment(sketch, "E465", {"start": v(-6.42, -8.5) * mm, "end": v(-6.43, -8.55) * mm});
            skLineSegment(sketch, "E466", {"start": v(-6.43, -8.55) * mm, "end": v(-6.45, -8.58) * mm});
            skLineSegment(sketch, "E467", {"start": v(-6.45, -8.58) * mm, "end": v(-6.47, -8.62) * mm});
            skLineSegment(sketch, "E468", {"start": v(-6.47, -8.62) * mm, "end": v(-6.49, -8.66) * mm});
            skLineSegment(sketch, "E469", {"start": v(-6.49, -8.66) * mm, "end": v(-6.5, -8.7) * mm});
            skLineSegment(sketch, "E470", {"start": v(-6.5, -8.7) * mm, "end": v(-6.53, -8.73) * mm});
            skLineSegment(sketch, "E471", {"start": v(-6.53, -8.73) * mm, "end": v(-6.56, -8.76) * mm});
            skLineSegment(sketch, "E472", {"start": v(-6.56, -8.76) * mm, "end": v(-6.6, -8.79) * mm});
            skLineSegment(sketch, "E473", {"start": v(-6.6, -8.79) * mm, "end": v(-6.62, -8.82) * mm});
            skLineSegment(sketch, "E474", {"start": v(-6.62, -8.82) * mm, "end": v(-6.66, -8.85) * mm});
            skLineSegment(sketch, "E475", {"start": v(-6.66, -8.85) * mm, "end": v(-7.73, -8.87) * mm});
            skLineSegment(sketch, "E476", {"start": v(-7.73, -8.87) * mm, "end": v(-7.73, -7.3) * mm});
            skLineSegment(sketch, "E477", {"start": v(-26.38, -9.67) * mm, "end": v(-26.27, -9.66) * mm});
            skLineSegment(sketch, "E478", {"start": v(-26.27, -9.66) * mm, "end": v(-26.08, -9.64) * mm});
            skLineSegment(sketch, "E479", {"start": v(-26.08, -9.64) * mm, "end": v(-25.28, -9.63) * mm});
            skLineSegment(sketch, "E480", {"start": v(-25.28, -9.63) * mm, "end": v(-25.3, -11.2) * mm});
            skLineSegment(sketch, "E481", {"start": v(-25.3, -11.2) * mm, "end": v(-26.03, -11.2) * mm});
            skLineSegment(sketch, "E482", {"start": v(-26.03, -11.2) * mm, "end": v(-26.17, -11.2) * mm});
            skLineSegment(sketch, "E483", {"start": v(-26.17, -11.2) * mm, "end": v(-26.27, -11.19) * mm});
            skLineSegment(sketch, "E484", {"start": v(-26.27, -11.19) * mm, "end": v(-26.3, -11.18) * mm});
            skLineSegment(sketch, "E485", {"start": v(-26.3, -11.18) * mm, "end": v(-26.34, -11.17) * mm});
            skLineSegment(sketch, "E486", {"start": v(-26.34, -11.17) * mm, "end": v(-26.36, -11.16) * mm});
            skLineSegment(sketch, "E487", {"start": v(-26.36, -11.16) * mm, "end": v(-26.39, -11.15) * mm});
            skLineSegment(sketch, "E488", {"start": v(-26.39, -11.15) * mm, "end": v(-26.41, -11.13) * mm});
            skLineSegment(sketch, "E489", {"start": v(-26.41, -11.13) * mm, "end": v(-26.43, -11.11) * mm});
            skLineSegment(sketch, "E490", {"start": v(-26.43, -11.11) * mm, "end": v(-26.46, -11.1) * mm});
            skLineSegment(sketch, "E491", {"start": v(-26.46, -11.1) * mm, "end": v(-26.47, -11.08) * mm});
            skLineSegment(sketch, "E492", {"start": v(-26.47, -11.08) * mm, "end": v(-26.5, -11.05) * mm});
            skLineSegment(sketch, "E493", {"start": v(-26.5, -11.05) * mm, "end": v(-26.5, -11.03) * mm});
            skLineSegment(sketch, "E494", {"start": v(-26.5, -11.03) * mm, "end": v(-26.52, -11) * mm});
            skLineSegment(sketch, "E495", {"start": v(-26.52, -11) * mm, "end": v(-26.54, -10.98) * mm});
            skLineSegment(sketch, "E496", {"start": v(-26.54, -10.98) * mm, "end": v(-26.55, -10.95) * mm});
            skLineSegment(sketch, "E497", {"start": v(-26.55, -10.95) * mm, "end": v(-26.56, -10.93) * mm});
            skLineSegment(sketch, "E498", {"start": v(-26.56, -10.93) * mm, "end": v(-26.57, -10.9) * mm});
            skLineSegment(sketch, "E499", {"start": v(-26.57, -10.9) * mm, "end": v(-26.58, -10.87) * mm});
            skLineSegment(sketch, "E500", {"start": v(-26.58, -10.87) * mm, "end": v(-26.59, -10.84) * mm});
            skLineSegment(sketch, "E501", {"start": v(-26.59, -10.84) * mm, "end": v(-26.6, -10.78) * mm});
            skLineSegment(sketch, "E502", {"start": v(-26.6, -10.78) * mm, "end": v(-26.61, -10.72) * mm});
            skLineSegment(sketch, "E503", {"start": v(-26.61, -10.72) * mm, "end": v(-26.62, -10.63) * mm});
            skLineSegment(sketch, "E504", {"start": v(-26.62, -10.63) * mm, "end": v(-26.63, -10.55) * mm});
            skLineSegment(sketch, "E505", {"start": v(-26.63, -10.55) * mm, "end": v(-26.63, -10.5) * mm});
            skLineSegment(sketch, "E506", {"start": v(-26.63, -10.5) * mm, "end": v(-26.63, -10.47) * mm});
            skLineSegment(sketch, "E507", {"start": v(-26.63, -10.47) * mm, "end": v(-26.63, -10.38) * mm});
            skLineSegment(sketch, "E508", {"start": v(-26.63, -10.38) * mm, "end": v(-26.62, -10.23) * mm});
            skLineSegment(sketch, "E509", {"start": v(-26.62, -10.23) * mm, "end": v(-26.62, -10.14) * mm});
            skLineSegment(sketch, "E510", {"start": v(-26.62, -10.14) * mm, "end": v(-26.6, -10.08) * mm});
            skLineSegment(sketch, "E511", {"start": v(-26.6, -10.08) * mm, "end": v(-26.6, -10.02) * mm});
            skLineSegment(sketch, "E512", {"start": v(-26.6, -10.02) * mm, "end": v(-26.59, -9.99) * mm});
            skLineSegment(sketch, "E513", {"start": v(-26.59, -9.99) * mm, "end": v(-26.58, -9.96) * mm});
            skLineSegment(sketch, "E514", {"start": v(-26.58, -9.96) * mm, "end": v(-26.57, -9.93) * mm});
            skLineSegment(sketch, "E515", {"start": v(-26.57, -9.93) * mm, "end": v(-26.56, -9.9) * mm});
            skLineSegment(sketch, "E516", {"start": v(-26.56, -9.9) * mm, "end": v(-26.55, -9.87) * mm});
            skLineSegment(sketch, "E517", {"start": v(-26.55, -9.87) * mm, "end": v(-26.54, -9.85) * mm});
            skLineSegment(sketch, "E518", {"start": v(-26.54, -9.85) * mm, "end": v(-26.52, -9.82) * mm});
            skLineSegment(sketch, "E519", {"start": v(-26.52, -9.82) * mm, "end": v(-26.5, -9.8) * mm});
            skLineSegment(sketch, "E520", {"start": v(-26.5, -9.8) * mm, "end": v(-26.49, -9.77) * mm});
            skLineSegment(sketch, "E521", {"start": v(-26.49, -9.77) * mm, "end": v(-26.47, -9.75) * mm});
            skLineSegment(sketch, "E522", {"start": v(-26.47, -9.75) * mm, "end": v(-26.45, -9.73) * mm});
            skLineSegment(sketch, "E523", {"start": v(-26.45, -9.73) * mm, "end": v(-26.43, -9.71) * mm});
            skLineSegment(sketch, "E524", {"start": v(-26.43, -9.71) * mm, "end": v(-26.4, -9.7) * mm});
            skLineSegment(sketch, "E525", {"start": v(-26.4, -9.7) * mm, "end": v(-26.38, -9.67) * mm});
            skLineSegment(sketch, "E526", {"start": v(-7.73, -9.64) * mm, "end": v(-6.54, -9.67) * mm});
            skLineSegment(sketch, "E527", {"start": v(-6.54, -9.67) * mm, "end": v(-6.51, -9.75) * mm});
            skLineSegment(sketch, "E528", {"start": v(-6.51, -9.75) * mm, "end": v(-6.48, -9.83) * mm});
            skLineSegment(sketch, "E529", {"start": v(-6.48, -9.83) * mm, "end": v(-6.46, -9.9) * mm});
            skLineSegment(sketch, "E530", {"start": v(-6.46, -9.9) * mm, "end": v(-6.44, -9.99) * mm});
            skLineSegment(sketch, "E531", {"start": v(-6.44, -9.99) * mm, "end": v(-6.42, -10.07) * mm});
            skLineSegment(sketch, "E532", {"start": v(-6.42, -10.07) * mm, "end": v(-6.4, -10.15) * mm});
            skLineSegment(sketch, "E533", {"start": v(-6.4, -10.15) * mm, "end": v(-6.4, -10.23) * mm});
            skLineSegment(sketch, "E534", {"start": v(-6.4, -10.23) * mm, "end": v(-6.39, -10.32) * mm});
            skLineSegment(sketch, "E535", {"start": v(-6.39, -10.32) * mm, "end": v(-6.38, -10.4) * mm});
            skLineSegment(sketch, "E536", {"start": v(-6.38, -10.4) * mm, "end": v(-6.38, -10.44) * mm});
            skLineSegment(sketch, "E537", {"start": v(-6.38, -10.44) * mm, "end": v(-6.38, -10.48) * mm});
            skLineSegment(sketch, "E538", {"start": v(-6.38, -10.48) * mm, "end": v(-6.38, -10.53) * mm});
            skLineSegment(sketch, "E539", {"start": v(-6.38, -10.53) * mm, "end": v(-6.39, -10.57) * mm});
            skLineSegment(sketch, "E540", {"start": v(-6.39, -10.57) * mm, "end": v(-6.39, -10.6) * mm});
            skLineSegment(sketch, "E541", {"start": v(-6.39, -10.6) * mm, "end": v(-6.4, -10.65) * mm});
            skLineSegment(sketch, "E542", {"start": v(-6.4, -10.65) * mm, "end": v(-6.4, -10.7) * mm});
            skLineSegment(sketch, "E543", {"start": v(-6.4, -10.7) * mm, "end": v(-6.4, -10.73) * mm});
            skLineSegment(sketch, "E544", {"start": v(-6.4, -10.73) * mm, "end": v(-6.41, -10.77) * mm});
            skLineSegment(sketch, "E545", {"start": v(-6.41, -10.77) * mm, "end": v(-6.42, -10.82) * mm});
            skLineSegment(sketch, "E546", {"start": v(-6.42, -10.82) * mm, "end": v(-6.43, -10.86) * mm});
            skLineSegment(sketch, "E547", {"start": v(-6.43, -10.86) * mm, "end": v(-6.45, -10.92) * mm});
            skLineSegment(sketch, "E548", {"start": v(-6.45, -10.92) * mm, "end": v(-6.47, -10.97) * mm});
            skLineSegment(sketch, "E549", {"start": v(-6.47, -10.97) * mm, "end": v(-6.5, -11.03) * mm});
            skLineSegment(sketch, "E550", {"start": v(-6.5, -11.03) * mm, "end": v(-6.53, -11.07) * mm});
            skLineSegment(sketch, "E551", {"start": v(-6.53, -11.07) * mm, "end": v(-6.56, -11.1) * mm});
            skLineSegment(sketch, "E552", {"start": v(-6.56, -11.1) * mm, "end": v(-6.58, -11.12) * mm});
            skLineSegment(sketch, "E553", {"start": v(-6.58, -11.12) * mm, "end": v(-6.6, -11.14) * mm});
            skLineSegment(sketch, "E554", {"start": v(-6.6, -11.14) * mm, "end": v(-6.64, -11.15) * mm});
            skLineSegment(sketch, "E555", {"start": v(-6.64, -11.15) * mm, "end": v(-6.66, -11.17) * mm});
            skLineSegment(sketch, "E556", {"start": v(-6.66, -11.17) * mm, "end": v(-6.7, -11.18) * mm});
            skLineSegment(sketch, "E557", {"start": v(-6.7, -11.18) * mm, "end": v(-6.7, -11.18) * mm});
            skLineSegment(sketch, "E558", {"start": v(-6.7, -11.18) * mm, "end": v(-7.72, -11.2) * mm});
            skLineSegment(sketch, "E559", {"start": v(-7.72, -11.2) * mm, "end": v(-7.73, -9.64) * mm});
            skLineSegment(sketch, "E560", {"start": v(-26.47, -12.01) * mm, "end": v(-25.28, -11.98) * mm});
            skLineSegment(sketch, "E561", {"start": v(-25.28, -11.98) * mm, "end": v(-25.3, -13.53) * mm});
            skLineSegment(sketch, "E562", {"start": v(-25.3, -13.53) * mm, "end": v(-25.33, -13.53) * mm});
            skLineSegment(sketch, "E563", {"start": v(-25.33, -13.53) * mm, "end": v(-25.38, -13.52) * mm});
            skLineSegment(sketch, "E564", {"start": v(-25.38, -13.52) * mm, "end": v(-25.42, -13.52) * mm});
            skLineSegment(sketch, "E565", {"start": v(-25.42, -13.52) * mm, "end": v(-25.47, -13.52) * mm});
            skLineSegment(sketch, "E566", {"start": v(-25.47, -13.52) * mm, "end": v(-25.5, -13.52) * mm});
            skLineSegment(sketch, "E567", {"start": v(-25.5, -13.52) * mm, "end": v(-25.6, -13.53) * mm});
            skLineSegment(sketch, "E568", {"start": v(-25.6, -13.53) * mm, "end": v(-25.88, -13.56) * mm});
            skLineSegment(sketch, "E569", {"start": v(-25.88, -13.56) * mm, "end": v(-25.93, -13.56) * mm});
            skLineSegment(sketch, "E570", {"start": v(-25.93, -13.56) * mm, "end": v(-25.97, -13.56) * mm});
            skLineSegment(sketch, "E571", {"start": v(-25.97, -13.56) * mm, "end": v(-26.02, -13.56) * mm});
            skLineSegment(sketch, "E572", {"start": v(-26.02, -13.56) * mm, "end": v(-26.06, -13.56) * mm});
            skLineSegment(sketch, "E573", {"start": v(-26.06, -13.56) * mm, "end": v(-26.1, -13.56) * mm});
            skLineSegment(sketch, "E574", {"start": v(-26.1, -13.56) * mm, "end": v(-26.15, -13.56) * mm});
            skLineSegment(sketch, "E575", {"start": v(-26.15, -13.56) * mm, "end": v(-26.2, -13.55) * mm});
            skLineSegment(sketch, "E576", {"start": v(-26.2, -13.55) * mm, "end": v(-26.24, -13.54) * mm});
            skLineSegment(sketch, "E577", {"start": v(-26.24, -13.54) * mm, "end": v(-26.28, -13.53) * mm});
            skLineSegment(sketch, "E578", {"start": v(-26.28, -13.53) * mm, "end": v(-26.32, -13.52) * mm});
            skLineSegment(sketch, "E579", {"start": v(-26.32, -13.52) * mm, "end": v(-26.36, -13.5) * mm});
            skLineSegment(sketch, "E580", {"start": v(-26.36, -13.5) * mm, "end": v(-26.4, -13.48) * mm});
            skLineSegment(sketch, "E581", {"start": v(-26.4, -13.48) * mm, "end": v(-26.43, -13.45) * mm});
            skLineSegment(sketch, "E582", {"start": v(-26.43, -13.45) * mm, "end": v(-26.46, -13.43) * mm});
            skLineSegment(sketch, "E583", {"start": v(-26.46, -13.43) * mm, "end": v(-26.5, -13.4) * mm});
            skLineSegment(sketch, "E584", {"start": v(-26.5, -13.4) * mm, "end": v(-26.53, -13.36) * mm});
            skLineSegment(sketch, "E585", {"start": v(-26.53, -13.36) * mm, "end": v(-26.55, -13.31) * mm});
            skLineSegment(sketch, "E586", {"start": v(-26.55, -13.31) * mm, "end": v(-26.56, -13.27) * mm});
            skLineSegment(sketch, "E587", {"start": v(-26.56, -13.27) * mm, "end": v(-26.57, -13.22) * mm});
            skLineSegment(sketch, "E588", {"start": v(-26.57, -13.22) * mm, "end": v(-26.59, -13.18) * mm});
            skLineSegment(sketch, "E589", {"start": v(-26.59, -13.18) * mm, "end": v(-26.6, -13.13) * mm});
            skLineSegment(sketch, "E590", {"start": v(-26.6, -13.13) * mm, "end": v(-26.6, -13.08) * mm});
            skLineSegment(sketch, "E591", {"start": v(-26.6, -13.08) * mm, "end": v(-26.61, -13.04) * mm});
            skLineSegment(sketch, "E592", {"start": v(-26.61, -13.04) * mm, "end": v(-26.62, -12.99) * mm});
            skLineSegment(sketch, "E593", {"start": v(-26.62, -12.99) * mm, "end": v(-26.63, -12.94) * mm});
            skLineSegment(sketch, "E594", {"start": v(-26.63, -12.94) * mm, "end": v(-26.63, -12.9) * mm});
            skLineSegment(sketch, "E595", {"start": v(-26.63, -12.9) * mm, "end": v(-26.63, -12.85) * mm});
            skLineSegment(sketch, "E596", {"start": v(-26.63, -12.85) * mm, "end": v(-26.63, -12.8) * mm});
            skLineSegment(sketch, "E597", {"start": v(-26.63, -12.8) * mm, "end": v(-26.63, -12.75) * mm});
            skLineSegment(sketch, "E598", {"start": v(-26.63, -12.75) * mm, "end": v(-26.63, -12.7) * mm});
            skLineSegment(sketch, "E599", {"start": v(-26.63, -12.7) * mm, "end": v(-26.63, -12.66) * mm});
            skLineSegment(sketch, "E600", {"start": v(-26.63, -12.66) * mm, "end": v(-26.62, -12.6) * mm});
            skLineSegment(sketch, "E601", {"start": v(-26.62, -12.6) * mm, "end": v(-26.62, -12.56) * mm});
            skLineSegment(sketch, "E602", {"start": v(-26.62, -12.56) * mm, "end": v(-26.61, -12.51) * mm});
            skLineSegment(sketch, "E603", {"start": v(-26.61, -12.51) * mm, "end": v(-26.6, -12.47) * mm});
            skLineSegment(sketch, "E604", {"start": v(-26.6, -12.47) * mm, "end": v(-26.6, -12.42) * mm});
            skLineSegment(sketch, "E605", {"start": v(-26.6, -12.42) * mm, "end": v(-26.59, -12.37) * mm});
            skLineSegment(sketch, "E606", {"start": v(-26.59, -12.37) * mm, "end": v(-26.58, -12.33) * mm});
            skLineSegment(sketch, "E607", {"start": v(-26.58, -12.33) * mm, "end": v(-26.56, -12.28) * mm});
            skLineSegment(sketch, "E608", {"start": v(-26.56, -12.28) * mm, "end": v(-26.55, -12.23) * mm});
            skLineSegment(sketch, "E609", {"start": v(-26.55, -12.23) * mm, "end": v(-26.54, -12.19) * mm});
            skLineSegment(sketch, "E610", {"start": v(-26.54, -12.19) * mm, "end": v(-26.52, -12.14) * mm});
            skLineSegment(sketch, "E611", {"start": v(-26.52, -12.14) * mm, "end": v(-26.5, -12.1) * mm});
            skLineSegment(sketch, "E612", {"start": v(-26.5, -12.1) * mm, "end": v(-26.49, -12.05) * mm});
            skLineSegment(sketch, "E613", {"start": v(-26.49, -12.05) * mm, "end": v(-26.47, -12.01) * mm});
            skLineSegment(sketch, "E614", {"start": v(-7.73, -11.98) * mm, "end": v(-6.54, -12.01) * mm});
            skLineSegment(sketch, "E615", {"start": v(-6.54, -12.01) * mm, "end": v(-6.52, -12.06) * mm});
            skLineSegment(sketch, "E616", {"start": v(-6.52, -12.06) * mm, "end": v(-6.5, -12.1) * mm});
            skLineSegment(sketch, "E617", {"start": v(-6.5, -12.1) * mm, "end": v(-6.49, -12.16) * mm});
            skLineSegment(sketch, "E618", {"start": v(-6.49, -12.16) * mm, "end": v(-6.47, -12.2) * mm});
            skLineSegment(sketch, "E619", {"start": v(-6.47, -12.2) * mm, "end": v(-6.46, -12.26) * mm});
            skLineSegment(sketch, "E620", {"start": v(-6.46, -12.26) * mm, "end": v(-6.44, -12.31) * mm});
            skLineSegment(sketch, "E621", {"start": v(-6.44, -12.31) * mm, "end": v(-6.43, -12.37) * mm});
            skLineSegment(sketch, "E622", {"start": v(-6.43, -12.37) * mm, "end": v(-6.42, -12.42) * mm});
            skLineSegment(sketch, "E623", {"start": v(-6.42, -12.42) * mm, "end": v(-6.4, -12.48) * mm});
            skLineSegment(sketch, "E624", {"start": v(-6.4, -12.48) * mm, "end": v(-6.4, -12.53) * mm});
            skLineSegment(sketch, "E625", {"start": v(-6.4, -12.53) * mm, "end": v(-6.39, -12.59) * mm});
            skLineSegment(sketch, "E626", {"start": v(-6.39, -12.59) * mm, "end": v(-6.38, -12.64) * mm});
            skLineSegment(sketch, "E627", {"start": v(-6.38, -12.64) * mm, "end": v(-6.38, -12.7) * mm});
            skLineSegment(sketch, "E628", {"start": v(-6.38, -12.7) * mm, "end": v(-6.37, -12.75) * mm});
            skLineSegment(sketch, "E629", {"start": v(-6.37, -12.75) * mm, "end": v(-6.37, -12.8) * mm});
            skLineSegment(sketch, "E630", {"start": v(-6.37, -12.8) * mm, "end": v(-6.37, -12.86) * mm});
            skLineSegment(sketch, "E631", {"start": v(-6.37, -12.86) * mm, "end": v(-6.38, -12.91) * mm});
            skLineSegment(sketch, "E632", {"start": v(-6.38, -12.91) * mm, "end": v(-6.38, -12.97) * mm});
            skLineSegment(sketch, "E633", {"start": v(-6.38, -12.97) * mm, "end": v(-6.39, -13.02) * mm});
            skLineSegment(sketch, "E634", {"start": v(-6.39, -13.02) * mm, "end": v(-6.4, -13.07) * mm});
            skLineSegment(sketch, "E635", {"start": v(-6.4, -13.07) * mm, "end": v(-6.4, -13.12) * mm});
            skLineSegment(sketch, "E636", {"start": v(-6.4, -13.12) * mm, "end": v(-6.42, -13.17) * mm});
            skLineSegment(sketch, "E637", {"start": v(-6.42, -13.17) * mm, "end": v(-6.44, -13.22) * mm});
            skLineSegment(sketch, "E638", {"start": v(-6.44, -13.22) * mm, "end": v(-6.46, -13.27) * mm});
            skLineSegment(sketch, "E639", {"start": v(-6.46, -13.27) * mm, "end": v(-6.49, -13.32) * mm});
            skLineSegment(sketch, "E640", {"start": v(-6.49, -13.32) * mm, "end": v(-6.51, -13.36) * mm});
            skLineSegment(sketch, "E641", {"start": v(-6.51, -13.36) * mm, "end": v(-6.54, -13.4) * mm});
            skLineSegment(sketch, "E642", {"start": v(-6.54, -13.4) * mm, "end": v(-6.58, -13.45) * mm});
            skLineSegment(sketch, "E643", {"start": v(-6.58, -13.45) * mm, "end": v(-6.61, -13.49) * mm});
            skLineSegment(sketch, "E644", {"start": v(-6.61, -13.49) * mm, "end": v(-6.65, -13.5) * mm});
            skLineSegment(sketch, "E645", {"start": v(-6.65, -13.5) * mm, "end": v(-6.69, -13.5) * mm});
            skLineSegment(sketch, "E646", {"start": v(-6.69, -13.5) * mm, "end": v(-6.72, -13.52) * mm});
            skLineSegment(sketch, "E647", {"start": v(-6.72, -13.52) * mm, "end": v(-6.76, -13.52) * mm});
            skLineSegment(sketch, "E648", {"start": v(-6.76, -13.52) * mm, "end": v(-6.8, -13.53) * mm});
            skLineSegment(sketch, "E649", {"start": v(-6.8, -13.53) * mm, "end": v(-6.87, -13.54) * mm});
            skLineSegment(sketch, "E650", {"start": v(-6.87, -13.54) * mm, "end": v(-6.95, -13.55) * mm});
            skLineSegment(sketch, "E651", {"start": v(-6.95, -13.55) * mm, "end": v(-7.06, -13.55) * mm});
            skLineSegment(sketch, "E652", {"start": v(-7.06, -13.55) * mm, "end": v(-7.6, -13.53) * mm});
            skLineSegment(sketch, "E653", {"start": v(-7.6, -13.53) * mm, "end": v(-7.72, -13.53) * mm});
            skLineSegment(sketch, "E654", {"start": v(-7.72, -13.53) * mm, "end": v(-7.73, -11.98) * mm});
            skLineSegment(sketch, "E655", {"start": v(-20.77, -15.27) * mm, "end": v(-19.21, -15.27) * mm});
            skLineSegment(sketch, "E656", {"start": v(-19.21, -15.27) * mm, "end": v(-19.21, -16.13) * mm});
            skLineSegment(sketch, "E657", {"start": v(-19.21, -16.13) * mm, "end": v(-19.22, -16.27) * mm});
            skLineSegment(sketch, "E658", {"start": v(-19.22, -16.27) * mm, "end": v(-19.23, -16.29) * mm});
            skLineSegment(sketch, "E659", {"start": v(-19.23, -16.29) * mm, "end": v(-19.23, -16.3) * mm});
            skLineSegment(sketch, "E660", {"start": v(-19.23, -16.3) * mm, "end": v(-19.24, -16.32) * mm});
            skLineSegment(sketch, "E661", {"start": v(-19.24, -16.32) * mm, "end": v(-19.24, -16.34) * mm});
            skLineSegment(sketch, "E662", {"start": v(-19.24, -16.34) * mm, "end": v(-19.25, -16.35) * mm});
            skLineSegment(sketch, "E663", {"start": v(-19.25, -16.35) * mm, "end": v(-19.26, -16.37) * mm});
            skLineSegment(sketch, "E664", {"start": v(-19.26, -16.37) * mm, "end": v(-19.27, -16.38) * mm});
            skLineSegment(sketch, "E665", {"start": v(-19.27, -16.38) * mm, "end": v(-19.28, -16.4) * mm});
            skLineSegment(sketch, "E666", {"start": v(-19.28, -16.4) * mm, "end": v(-19.3, -16.41) * mm});
            skLineSegment(sketch, "E667", {"start": v(-19.3, -16.41) * mm, "end": v(-19.32, -16.43) * mm});
            skLineSegment(sketch, "E668", {"start": v(-19.32, -16.43) * mm, "end": v(-19.34, -16.46) * mm});
            skLineSegment(sketch, "E669", {"start": v(-19.34, -16.46) * mm, "end": v(-19.39, -16.49) * mm});
            skLineSegment(sketch, "E670", {"start": v(-19.39, -16.49) * mm, "end": v(-19.47, -16.53) * mm});
            skLineSegment(sketch, "E671", {"start": v(-19.47, -16.53) * mm, "end": v(-19.6, -16.58) * mm});
            skLineSegment(sketch, "E672", {"start": v(-19.6, -16.58) * mm, "end": v(-19.69, -16.6) * mm});
            skLineSegment(sketch, "E673", {"start": v(-19.69, -16.6) * mm, "end": v(-19.73, -16.6) * mm});
            skLineSegment(sketch, "E674", {"start": v(-19.73, -16.6) * mm, "end": v(-19.77, -16.6) * mm});
            skLineSegment(sketch, "E675", {"start": v(-19.77, -16.6) * mm, "end": v(-19.81, -16.61) * mm});
            skLineSegment(sketch, "E676", {"start": v(-19.81, -16.61) * mm, "end": v(-19.86, -16.62) * mm});
            skLineSegment(sketch, "E677", {"start": v(-19.86, -16.62) * mm, "end": v(-19.9, -16.62) * mm});
            skLineSegment(sketch, "E678", {"start": v(-19.9, -16.62) * mm, "end": v(-19.94, -16.62) * mm});
            skLineSegment(sketch, "E679", {"start": v(-19.94, -16.62) * mm, "end": v(-19.98, -16.62) * mm});
            skLineSegment(sketch, "E680", {"start": v(-19.98, -16.62) * mm, "end": v(-20.03, -16.62) * mm});
            skLineSegment(sketch, "E681", {"start": v(-20.03, -16.62) * mm, "end": v(-20.07, -16.62) * mm});
            skLineSegment(sketch, "E682", {"start": v(-20.07, -16.62) * mm, "end": v(-20.11, -16.62) * mm});
            skLineSegment(sketch, "E683", {"start": v(-20.11, -16.62) * mm, "end": v(-20.15, -16.62) * mm});
            skLineSegment(sketch, "E684", {"start": v(-20.15, -16.62) * mm, "end": v(-20.2, -16.61) * mm});
            skLineSegment(sketch, "E685", {"start": v(-20.2, -16.61) * mm, "end": v(-20.24, -16.6) * mm});
            skLineSegment(sketch, "E686", {"start": v(-20.24, -16.6) * mm, "end": v(-20.28, -16.6) * mm});
            skLineSegment(sketch, "E687", {"start": v(-20.28, -16.6) * mm, "end": v(-20.32, -16.6) * mm});
            skLineSegment(sketch, "E688", {"start": v(-20.32, -16.6) * mm, "end": v(-20.36, -16.58) * mm});
            skLineSegment(sketch, "E689", {"start": v(-20.36, -16.58) * mm, "end": v(-20.4, -16.57) * mm});
            skLineSegment(sketch, "E690", {"start": v(-20.4, -16.57) * mm, "end": v(-20.44, -16.56) * mm});
            skLineSegment(sketch, "E691", {"start": v(-20.44, -16.56) * mm, "end": v(-20.48, -16.54) * mm});
            skLineSegment(sketch, "E692", {"start": v(-20.48, -16.54) * mm, "end": v(-20.52, -16.53) * mm});
            skLineSegment(sketch, "E693", {"start": v(-20.52, -16.53) * mm, "end": v(-20.56, -16.51) * mm});
            skLineSegment(sketch, "E694", {"start": v(-20.56, -16.51) * mm, "end": v(-20.6, -16.5) * mm});
            skLineSegment(sketch, "E695", {"start": v(-20.6, -16.5) * mm, "end": v(-20.64, -16.47) * mm});
            skLineSegment(sketch, "E696", {"start": v(-20.64, -16.47) * mm, "end": v(-20.68, -16.45) * mm});
            skLineSegment(sketch, "E697", {"start": v(-20.68, -16.45) * mm, "end": v(-20.71, -16.43) * mm});
            skLineSegment(sketch, "E698", {"start": v(-20.71, -16.43) * mm, "end": v(-20.75, -16.4) * mm});
            skLineSegment(sketch, "E699", {"start": v(-20.75, -16.4) * mm, "end": v(-20.78, -16.38) * mm});
            skLineSegment(sketch, "E700", {"start": v(-20.78, -16.38) * mm, "end": v(-20.77, -15.27) * mm});
            skLineSegment(sketch, "E701", {"start": v(-18.48, -15.27) * mm, "end": v(-16.91, -15.27) * mm});
            skLineSegment(sketch, "E702", {"start": v(-16.91, -15.27) * mm, "end": v(-16.89, -16.15) * mm});
            skLineSegment(sketch, "E703", {"start": v(-16.89, -16.15) * mm, "end": v(-16.9, -16.21) * mm});
            skLineSegment(sketch, "E704", {"start": v(-16.9, -16.21) * mm, "end": v(-16.9, -16.27) * mm});
            skLineSegment(sketch, "E705", {"start": v(-16.9, -16.27) * mm, "end": v(-16.93, -16.32) * mm});
            skLineSegment(sketch, "E706", {"start": v(-16.93, -16.32) * mm, "end": v(-16.96, -16.37) * mm});
            skLineSegment(sketch, "E707", {"start": v(-16.96, -16.37) * mm, "end": v(-17, -16.42) * mm});
            skLineSegment(sketch, "E708", {"start": v(-17, -16.42) * mm, "end": v(-17.02, -16.45) * mm});
            skLineSegment(sketch, "E709", {"start": v(-17.02, -16.45) * mm, "end": v(-17.04, -16.47) * mm});
            skLineSegment(sketch, "E710", {"start": v(-17.04, -16.47) * mm, "end": v(-17.07, -16.5) * mm});
            skLineSegment(sketch, "E711", {"start": v(-17.07, -16.5) * mm, "end": v(-17.1, -16.52) * mm});
            skLineSegment(sketch, "E712", {"start": v(-17.1, -16.52) * mm, "end": v(-17.13, -16.54) * mm});
            skLineSegment(sketch, "E713", {"start": v(-17.13, -16.54) * mm, "end": v(-17.15, -16.55) * mm});
            skLineSegment(sketch, "E714", {"start": v(-17.15, -16.55) * mm, "end": v(-17.17, -16.56) * mm});
            skLineSegment(sketch, "E715", {"start": v(-17.17, -16.56) * mm, "end": v(-17.19, -16.56) * mm});
            skLineSegment(sketch, "E716", {"start": v(-17.19, -16.56) * mm, "end": v(-17.2, -16.57) * mm});
            skLineSegment(sketch, "E717", {"start": v(-17.2, -16.57) * mm, "end": v(-17.22, -16.57) * mm});
            skLineSegment(sketch, "E718", {"start": v(-17.22, -16.57) * mm, "end": v(-17.24, -16.57) * mm});
            skLineSegment(sketch, "E719", {"start": v(-17.24, -16.57) * mm, "end": v(-17.26, -16.58) * mm});
            skLineSegment(sketch, "E720", {"start": v(-17.26, -16.58) * mm, "end": v(-17.3, -16.58) * mm});
            skLineSegment(sketch, "E721", {"start": v(-17.3, -16.58) * mm, "end": v(-17.39, -16.6) * mm});
            skLineSegment(sketch, "E722", {"start": v(-17.39, -16.6) * mm, "end": v(-17.47, -16.61) * mm});
            skLineSegment(sketch, "E723", {"start": v(-17.47, -16.61) * mm, "end": v(-17.56, -16.62) * mm});
            skLineSegment(sketch, "E724", {"start": v(-17.56, -16.62) * mm, "end": v(-17.6, -16.62) * mm});
            skLineSegment(sketch, "E725", {"start": v(-17.6, -16.62) * mm, "end": v(-17.65, -16.63) * mm});
            skLineSegment(sketch, "E726", {"start": v(-17.65, -16.63) * mm, "end": v(-17.7, -16.63) * mm});
            skLineSegment(sketch, "E727", {"start": v(-17.7, -16.63) * mm, "end": v(-17.74, -16.63) * mm});
            skLineSegment(sketch, "E728", {"start": v(-17.74, -16.63) * mm, "end": v(-17.79, -16.63) * mm});
            skLineSegment(sketch, "E729", {"start": v(-17.79, -16.63) * mm, "end": v(-17.83, -16.62) * mm});
            skLineSegment(sketch, "E730", {"start": v(-17.83, -16.62) * mm, "end": v(-17.88, -16.62) * mm});
            skLineSegment(sketch, "E731", {"start": v(-17.88, -16.62) * mm, "end": v(-17.92, -16.61) * mm});
            skLineSegment(sketch, "E732", {"start": v(-17.92, -16.61) * mm, "end": v(-17.96, -16.6) * mm});
            skLineSegment(sketch, "E733", {"start": v(-17.96, -16.6) * mm, "end": v(-18, -16.6) * mm});
            skLineSegment(sketch, "E734", {"start": v(-18, -16.6) * mm, "end": v(-18.05, -16.59) * mm});
            skLineSegment(sketch, "E735", {"start": v(-18.05, -16.59) * mm, "end": v(-18.1, -16.57) * mm});
            skLineSegment(sketch, "E736", {"start": v(-18.1, -16.57) * mm, "end": v(-18.13, -16.56) * mm});
            skLineSegment(sketch, "E737", {"start": v(-18.13, -16.56) * mm, "end": v(-18.17, -16.54) * mm});
            skLineSegment(sketch, "E738", {"start": v(-18.17, -16.54) * mm, "end": v(-18.2, -16.52) * mm});
            skLineSegment(sketch, "E739", {"start": v(-18.2, -16.52) * mm, "end": v(-18.25, -16.5) * mm});
            skLineSegment(sketch, "E740", {"start": v(-18.25, -16.5) * mm, "end": v(-18.28, -16.48) * mm});
            skLineSegment(sketch, "E741", {"start": v(-18.28, -16.48) * mm, "end": v(-18.32, -16.45) * mm});
            skLineSegment(sketch, "E742", {"start": v(-18.32, -16.45) * mm, "end": v(-18.35, -16.42) * mm});
            skLineSegment(sketch, "E743", {"start": v(-18.35, -16.42) * mm, "end": v(-18.38, -16.39) * mm});
            skLineSegment(sketch, "E744", {"start": v(-18.38, -16.39) * mm, "end": v(-18.4, -16.35) * mm});
            skLineSegment(sketch, "E745", {"start": v(-18.4, -16.35) * mm, "end": v(-18.44, -16.32) * mm});
            skLineSegment(sketch, "E746", {"start": v(-18.44, -16.32) * mm, "end": v(-18.45, -16.25) * mm});
            skLineSegment(sketch, "E747", {"start": v(-18.45, -16.25) * mm, "end": v(-18.46, -16.14) * mm});
            skLineSegment(sketch, "E748", {"start": v(-18.46, -16.14) * mm, "end": v(-18.48, -15.96) * mm});
            skLineSegment(sketch, "E749", {"start": v(-18.48, -15.96) * mm, "end": v(-18.48, -15.27) * mm});
            skLineSegment(sketch, "E750", {"start": v(-16.1, -15.27) * mm, "end": v(-14.53, -15.27) * mm});
            skLineSegment(sketch, "E751", {"start": v(-14.53, -15.27) * mm, "end": v(-14.53, -15.99) * mm});
            skLineSegment(sketch, "E752", {"start": v(-14.53, -15.99) * mm, "end": v(-14.54, -16.16) * mm});
            skLineSegment(sketch, "E753", {"start": v(-14.54, -16.16) * mm, "end": v(-14.55, -16.26) * mm});
            skLineSegment(sketch, "E754", {"start": v(-14.55, -16.26) * mm, "end": v(-14.57, -16.3) * mm});
            skLineSegment(sketch, "E755", {"start": v(-14.57, -16.3) * mm, "end": v(-14.59, -16.33) * mm});
            skLineSegment(sketch, "E756", {"start": v(-14.59, -16.33) * mm, "end": v(-14.6, -16.36) * mm});
            skLineSegment(sketch, "E757", {"start": v(-14.6, -16.36) * mm, "end": v(-14.63, -16.38) * mm});
            skLineSegment(sketch, "E758", {"start": v(-14.63, -16.38) * mm, "end": v(-14.65, -16.41) * mm});
            skLineSegment(sketch, "E759", {"start": v(-14.65, -16.41) * mm, "end": v(-14.67, -16.44) * mm});
            skLineSegment(sketch, "E760", {"start": v(-14.67, -16.44) * mm, "end": v(-14.7, -16.46) * mm});
            skLineSegment(sketch, "E761", {"start": v(-14.7, -16.46) * mm, "end": v(-14.73, -16.48) * mm});
            skLineSegment(sketch, "E762", {"start": v(-14.73, -16.48) * mm, "end": v(-14.76, -16.5) * mm});
            skLineSegment(sketch, "E763", {"start": v(-14.76, -16.5) * mm, "end": v(-14.78, -16.52) * mm});
            skLineSegment(sketch, "E764", {"start": v(-14.78, -16.52) * mm, "end": v(-14.82, -16.53) * mm});
            skLineSegment(sketch, "E765", {"start": v(-14.82, -16.53) * mm, "end": v(-14.85, -16.55) * mm});
            skLineSegment(sketch, "E766", {"start": v(-14.85, -16.55) * mm, "end": v(-14.88, -16.56) * mm});
            skLineSegment(sketch, "E767", {"start": v(-14.88, -16.56) * mm, "end": v(-14.91, -16.57) * mm});
            skLineSegment(sketch, "E768", {"start": v(-14.91, -16.57) * mm, "end": v(-14.95, -16.58) * mm});
            skLineSegment(sketch, "E769", {"start": v(-14.95, -16.58) * mm, "end": v(-14.98, -16.59) * mm});
            skLineSegment(sketch, "E770", {"start": v(-14.98, -16.59) * mm, "end": v(-15.02, -16.6) * mm});
            skLineSegment(sketch, "E771", {"start": v(-15.02, -16.6) * mm, "end": v(-15.05, -16.6) * mm});
            skLineSegment(sketch, "E772", {"start": v(-15.05, -16.6) * mm, "end": v(-15.1, -16.6) * mm});
            skLineSegment(sketch, "E773", {"start": v(-15.1, -16.6) * mm, "end": v(-15.16, -16.61) * mm});
            skLineSegment(sketch, "E774", {"start": v(-15.16, -16.61) * mm, "end": v(-15.24, -16.62) * mm});
            skLineSegment(sketch, "E775", {"start": v(-15.24, -16.62) * mm, "end": v(-15.3, -16.62) * mm});
            skLineSegment(sketch, "E776", {"start": v(-15.3, -16.62) * mm, "end": v(-15.38, -16.62) * mm});
            skLineSegment(sketch, "E777", {"start": v(-15.38, -16.62) * mm, "end": v(-15.44, -16.61) * mm});
            skLineSegment(sketch, "E778", {"start": v(-15.44, -16.61) * mm, "end": v(-15.5, -16.62) * mm});
            skLineSegment(sketch, "E779", {"start": v(-15.5, -16.62) * mm, "end": v(-15.55, -16.61) * mm});
            skLineSegment(sketch, "E780", {"start": v(-15.55, -16.61) * mm, "end": v(-15.6, -16.6) * mm});
            skLineSegment(sketch, "E781", {"start": v(-15.6, -16.6) * mm, "end": v(-15.66, -16.6) * mm});
            skLineSegment(sketch, "E782", {"start": v(-15.66, -16.6) * mm, "end": v(-15.71, -16.59) * mm});
            skLineSegment(sketch, "E783", {"start": v(-15.71, -16.59) * mm, "end": v(-15.74, -16.58) * mm});
            skLineSegment(sketch, "E784", {"start": v(-15.74, -16.58) * mm, "end": v(-15.77, -16.57) * mm});
            skLineSegment(sketch, "E785", {"start": v(-15.77, -16.57) * mm, "end": v(-15.8, -16.56) * mm});
            skLineSegment(sketch, "E786", {"start": v(-15.8, -16.56) * mm, "end": v(-15.82, -16.55) * mm});
            skLineSegment(sketch, "E787", {"start": v(-15.82, -16.55) * mm, "end": v(-15.84, -16.54) * mm});
            skLineSegment(sketch, "E788", {"start": v(-15.84, -16.54) * mm, "end": v(-15.87, -16.53) * mm});
            skLineSegment(sketch, "E789", {"start": v(-15.87, -16.53) * mm, "end": v(-15.9, -16.52) * mm});
            skLineSegment(sketch, "E790", {"start": v(-15.9, -16.52) * mm, "end": v(-15.92, -16.5) * mm});
            skLineSegment(sketch, "E791", {"start": v(-15.92, -16.5) * mm, "end": v(-15.94, -16.49) * mm});
            skLineSegment(sketch, "E792", {"start": v(-15.94, -16.49) * mm, "end": v(-15.96, -16.47) * mm});
            skLineSegment(sketch, "E793", {"start": v(-15.96, -16.47) * mm, "end": v(-15.98, -16.46) * mm});
            skLineSegment(sketch, "E794", {"start": v(-15.98, -16.46) * mm, "end": v(-16, -16.44) * mm});
            skLineSegment(sketch, "E795", {"start": v(-16, -16.44) * mm, "end": v(-16.02, -16.42) * mm});
            skLineSegment(sketch, "E796", {"start": v(-16.02, -16.42) * mm, "end": v(-16.04, -16.4) * mm});
            skLineSegment(sketch, "E797", {"start": v(-16.04, -16.4) * mm, "end": v(-16.05, -16.38) * mm});
            skLineSegment(sketch, "E798", {"start": v(-16.05, -16.38) * mm, "end": v(-16.07, -16.35) * mm});
            skLineSegment(sketch, "E799", {"start": v(-16.07, -16.35) * mm, "end": v(-16.08, -16.33) * mm});
            skLineSegment(sketch, "E800", {"start": v(-16.08, -16.33) * mm, "end": v(-16.1, -16.3) * mm});
            skLineSegment(sketch, "E801", {"start": v(-16.1, -16.3) * mm, "end": v(-16.1, -16.28) * mm});
            skLineSegment(sketch, "E802", {"start": v(-16.1, -16.28) * mm, "end": v(-16.12, -16.18) * mm});
            skLineSegment(sketch, "E803", {"start": v(-16.12, -16.18) * mm, "end": v(-16.13, -16.04) * mm});
            skLineSegment(sketch, "E804", {"start": v(-16.13, -16.04) * mm, "end": v(-16.13, -15.76) * mm});
            skLineSegment(sketch, "E805", {"start": v(-16.13, -15.76) * mm, "end": v(-16.1, -15.27) * mm});
            skLineSegment(sketch, "E806", {"start": v(-13.8, -15.27) * mm, "end": v(-12.24, -15.27) * mm});
            skLineSegment(sketch, "E807", {"start": v(-12.24, -15.27) * mm, "end": v(-12.23, -16.38) * mm});
            skLineSegment(sketch, "E808", {"start": v(-12.23, -16.38) * mm, "end": v(-12.27, -16.4) * mm});
            skLineSegment(sketch, "E809", {"start": v(-12.27, -16.4) * mm, "end": v(-12.3, -16.43) * mm});
            skLineSegment(sketch, "E810", {"start": v(-12.3, -16.43) * mm, "end": v(-12.34, -16.45) * mm});
            skLineSegment(sketch, "E811", {"start": v(-12.34, -16.45) * mm, "end": v(-12.38, -16.48) * mm});
            skLineSegment(sketch, "E812", {"start": v(-12.38, -16.48) * mm, "end": v(-12.42, -16.5) * mm});
            skLineSegment(sketch, "E813", {"start": v(-12.42, -16.5) * mm, "end": v(-12.46, -16.51) * mm});
            skLineSegment(sketch, "E814", {"start": v(-12.46, -16.51) * mm, "end": v(-12.5, -16.53) * mm});
            skLineSegment(sketch, "E815", {"start": v(-12.5, -16.53) * mm, "end": v(-12.54, -16.55) * mm});
            skLineSegment(sketch, "E816", {"start": v(-12.54, -16.55) * mm, "end": v(-12.58, -16.56) * mm});
            skLineSegment(sketch, "E817", {"start": v(-12.58, -16.56) * mm, "end": v(-12.62, -16.57) * mm});
            skLineSegment(sketch, "E818", {"start": v(-12.62, -16.57) * mm, "end": v(-12.66, -16.58) * mm});
            skLineSegment(sketch, "E819", {"start": v(-12.66, -16.58) * mm, "end": v(-12.7, -16.6) * mm});
            skLineSegment(sketch, "E820", {"start": v(-12.7, -16.6) * mm, "end": v(-12.75, -16.6) * mm});
            skLineSegment(sketch, "E821", {"start": v(-12.75, -16.6) * mm, "end": v(-12.8, -16.6) * mm});
            skLineSegment(sketch, "E822", {"start": v(-12.8, -16.6) * mm, "end": v(-12.84, -16.61) * mm});
            skLineSegment(sketch, "E823", {"start": v(-12.84, -16.61) * mm, "end": v(-12.88, -16.62) * mm});
            skLineSegment(sketch, "E824", {"start": v(-12.88, -16.62) * mm, "end": v(-12.92, -16.62) * mm});
            skLineSegment(sketch, "E825", {"start": v(-12.92, -16.62) * mm, "end": v(-12.97, -16.62) * mm});
            skLineSegment(sketch, "E826", {"start": v(-12.97, -16.62) * mm, "end": v(-13.01, -16.62) * mm});
            skLineSegment(sketch, "E827", {"start": v(-13.01, -16.62) * mm, "end": v(-13.05, -16.62) * mm});
            skLineSegment(sketch, "E828", {"start": v(-13.05, -16.62) * mm, "end": v(-13.1, -16.62) * mm});
            skLineSegment(sketch, "E829", {"start": v(-13.1, -16.62) * mm, "end": v(-13.14, -16.62) * mm});
            skLineSegment(sketch, "E830", {"start": v(-13.14, -16.62) * mm, "end": v(-13.19, -16.61) * mm});
            skLineSegment(sketch, "E831", {"start": v(-13.19, -16.61) * mm, "end": v(-13.23, -16.6) * mm});
            skLineSegment(sketch, "E832", {"start": v(-13.23, -16.6) * mm, "end": v(-13.27, -16.6) * mm});
            skLineSegment(sketch, "E833", {"start": v(-13.27, -16.6) * mm, "end": v(-13.32, -16.6) * mm});
            skLineSegment(sketch, "E834", {"start": v(-13.32, -16.6) * mm, "end": v(-13.36, -16.59) * mm});
            skLineSegment(sketch, "E835", {"start": v(-13.36, -16.59) * mm, "end": v(-13.4, -16.58) * mm});
            skLineSegment(sketch, "E836", {"start": v(-13.4, -16.58) * mm, "end": v(-13.44, -16.57) * mm});
            skLineSegment(sketch, "E837", {"start": v(-13.44, -16.57) * mm, "end": v(-13.63, -16.48) * mm});
            skLineSegment(sketch, "E838", {"start": v(-13.63, -16.48) * mm, "end": v(-13.67, -16.46) * mm});
            skLineSegment(sketch, "E839", {"start": v(-13.67, -16.46) * mm, "end": v(-13.7, -16.44) * mm});
            skLineSegment(sketch, "E840", {"start": v(-13.7, -16.44) * mm, "end": v(-13.72, -16.42) * mm});
            skLineSegment(sketch, "E841", {"start": v(-13.72, -16.42) * mm, "end": v(-13.74, -16.4) * mm});
            skLineSegment(sketch, "E842", {"start": v(-13.74, -16.4) * mm, "end": v(-13.74, -16.39) * mm});
            skLineSegment(sketch, "E843", {"start": v(-13.74, -16.39) * mm, "end": v(-13.75, -16.37) * mm});
            skLineSegment(sketch, "E844", {"start": v(-13.75, -16.37) * mm, "end": v(-13.76, -16.36) * mm});
            skLineSegment(sketch, "E845", {"start": v(-13.76, -16.36) * mm, "end": v(-13.76, -16.34) * mm});
            skLineSegment(sketch, "E846", {"start": v(-13.76, -16.34) * mm, "end": v(-13.77, -16.33) * mm});
            skLineSegment(sketch, "E847", {"start": v(-13.77, -16.33) * mm, "end": v(-13.77, -16.31) * mm});
            skLineSegment(sketch, "E848", {"start": v(-13.77, -16.31) * mm, "end": v(-13.78, -16.3) * mm});
            skLineSegment(sketch, "E849", {"start": v(-13.78, -16.3) * mm, "end": v(-13.8, -15.27) * mm});
            skFitSpline(sketch, "E850", {"points": [v(-16.09, 0.4) * mm, v(-16.48, 0.53) * mm, v(-16.87, 0.42) * mm], "startDerivative": vector(-0.77, 0.4) * mm, "endDerivative": vector(-0.8, -0.36) * mm});
            skFitSpline(sketch, "E851", {"points": [v(-9.68, -1.66) * mm, v(-8.41, -1.95) * mm, v(-8.04, -3.41) * mm], "startDerivative": vector(3.1, -0.07) * mm, "endDerivative": vector(0.22, -3.4) * mm});
            skLineSegment(sketch, "E852", {"start": v(-8.04, -3.41) * mm, "end": v(-8.04, -3.57) * mm});
            skLineSegment(sketch, "E853", {"start": v(-16.09, 0.4) * mm, "end": v(-15.75, 0.24) * mm});
            skLineSegment(sketch, "E854", {"start": v(-17.01, 0.36) * mm, "end": v(-16.87, 0.42) * mm});
            skLineSegment(sketch, "E855", {"start": v(-9.68, -1.66) * mm, "end": v(-9.7, 0.57) * mm});
            skLineSegment(sketch, "E856", {"start": v(-13.9, -1.75) * mm, "end": v(-16.26, -0.55) * mm});
            skFitSpline(sketch, "E857", {"points": [v(-16.26, -0.55) * mm, v(-16.5, -0.47) * mm, v(-16.83, -0.6) * mm], "startDerivative": vector(-0.52, 0.27) * mm, "endDerivative": vector(-0.63, -0.37) * mm});
            skFitSpline(sketch, "E858", {"points": [v(-9.4, -3.99) * mm, v(-9.18, -4.2) * mm, v(-9.85, -4.84) * mm], "startDerivative": vector(0.88, -0.52) * mm, "endDerivative": vector(-1.57, -1.12) * mm});
            skSolve(sketch);
        }
        {
            var Q0;
            Q0=qSketchRegion(id+"F27",true);
            extrude(context, id + "F28", {"entities" : qUnion([Q0]), "operationType" : NewBodyOperationType.ADD, "depth" : 26.5 * mm});
        }
        {
            var Q0;
            Q0=qSketchRegion(id+"F27",true);
            var Q1;
            {var subQ0=sQuery(id+"F0.wireOp",EDGE,"E7.rect.top");var subQ1=sQuery(id+"F0.wireOp",EDGE,"E7.rect.right");var subQ2=sQuery(id+"F0.wireOp",EDGE,"E7.rect.left");var subQ3=sQuery(id+"F0.wireOp",EDGE,"E7.rect.bottom");var subQ4=sQuery(id+"F0.wireOp",EDGE,"E5.MirrorC");var subQ5=sQuery(id+"F0.wireOp",EDGE,"E3");var subQ6=sQuery(id+"F0.wireOp",EDGE,"E2");var subQ7=sQuery(id+"F0.wireOp",EDGE,"E1");Q1=makeQuery(id+"F28.boolean.opBoolean","SPLIT",FACE,{"disambiguationData":[TD([makeQuery(id+"F28.opExtrude","SWEPT_FACE",FACE,{"disambiguationData":[OSD([sQuery(id+"F27.wireOp",EDGE,"E123")])]})])],"derivedFrom":makeQuery(id+"F6.opShell","OFFSET_FACE",FACE,{"disambiguationData":[OSD([subQ7,subQ6,subQ5,subQ4,subQ3,subQ0,subQ2,subQ1]),TDD([makeQuery(id+"F1.opExtrude","CAP_FACE",FACE,{"disambiguationData":[OSD([subQ7,subQ6,subQ5,subQ4,subQ3,subQ0,subQ2,subQ1])],"isStart":false})])]})});}
            extrude(context, id + "F29", {"entities" : qUnion([Q0]), "operationType" : NewBodyOperationType.REMOVE, "endBound" : BoundingType.UP_TO_SURFACE, "endBoundEntityFace" : qUnion([Q1]), "depth" : 23 * mm});
        }
        {
            var Q0;
            {var subQ0=sQuery(id+"F18.wireOp",EDGE,"E66");Q0=makeQuery(id+"F18.imprint","IMPRINT",FACE,{"disambiguationData":[TD([[makeQuery(id+"F18.imprint","IMPRINT",EDGE,{"derivedFrom":subQ0}),-1.0]])]});}
            extrude(context, id + "F30", {"entities" : qUnion([Q0]), "operationType" : NewBodyOperationType.REMOVE, "oppositeDirection" : true, "depth" : 2 * mm});
        }
        {
            var Q0;
            Q0=qCreatedBy(makeId("Top.planeOp"),FACE);
            var sketch = newSketch(context, id + "F31", { "sketchPlane" : qUnion([Q0])});
            skLineSegment(sketch, "E859.bottom", {"start": v(7.48, -5.58) * mm, "end": v(13.97, -5.58) * mm});
            skLineSegment(sketch, "E859.top", {"start": v(7.48, -5.2) * mm, "end": v(13.97, -5.2) * mm});
            skLineSegment(sketch, "E860.bottom", {"start": v(6.04, -5.58) * mm, "end": v(16.8, -5.58) * mm});
            skLineSegment(sketch, "E860.top", {"start": v(6.04, -5.2) * mm, "end": v(16.8, -5.2) * mm});
            skLineSegment(sketch, "E860.left", {"start": v(6.04, -5.58) * mm, "end": v(6.04, -5.2) * mm});
            skLineSegment(sketch, "E861", {"start": v(16.8, -5.2) * mm, "end": v(18.32, -5.2) * mm});
            skLineSegment(sketch, "E862", {"start": v(18.32, -5.2) * mm, "end": v(18.32, -5.58) * mm});
            skLineSegment(sketch, "E863", {"start": v(18.32, -5.58) * mm, "end": v(16.8, -5.58) * mm});
            skSolve(sketch);
        }
        {
            var Q0;
            Q0=qSketchRegion(id+"F31",true);
            var Q1;
            {var subQ1=sQuery(id+"F2.wireOp",EDGE,"E22");var subQ3=sQuery(id+"F2.wireOp",EDGE,"E20");Q1=makeQuery(id+"F24.boolean.opBoolean","SPLIT",FACE,{"disambiguationData":[TD([makeQuery(id+"F6.opShell","OFFSET_FACE",FACE,{"disambiguationData":[OSD([sQuery(id+"F0.wireOp",EDGE,"E3")])]})])],"derivedFrom":makeQuery(id+"F6.opShell","OFFSET_FACE",FACE,{"disambiguationData":[OSD([subQ3,subQ1])]})});}
            extrude(context, id + "F32", {"entities" : qUnion([Q0]), "operationType" : NewBodyOperationType.ADD, "endBound" : BoundingType.UP_TO_SURFACE, "endBoundEntityFace" : qUnion([Q1]), "depth" : 25 * mm});
        }
        {
            var Q0;
            {var subQ0=sQuery(id+"F0.wireOp",EDGE,"E7.rect.top");var subQ1=sQuery(id+"F0.wireOp",EDGE,"E7.rect.right");var subQ2=sQuery(id+"F0.wireOp",EDGE,"E7.rect.left");var subQ3=sQuery(id+"F0.wireOp",EDGE,"E7.rect.bottom");var subQ4=sQuery(id+"F0.wireOp",EDGE,"E5.MirrorC");var subQ5=sQuery(id+"F0.wireOp",EDGE,"E3");var subQ6=sQuery(id+"F0.wireOp",EDGE,"E2");var subQ7=sQuery(id+"F0.wireOp",EDGE,"E1");Q0=makeQuery(id+"F28.boolean.opBoolean","SPLIT",FACE,{"disambiguationData":[TD([makeQuery(id+"F4.opFillet","BLEND_FACE",FACE,{"disambiguationData":[OSD([subQ0])]})])],"derivedFrom":makeQuery(id+"F1.opExtrude","CAP_FACE",FACE,{"disambiguationData":[OSD([subQ7,subQ6,subQ5,subQ4,subQ3,subQ0,subQ2,subQ1])],"isStart":false})});}
            cPlane(context, id + "F33", {"entities" : qUnion([Q0]), "cplaneType" : CPlaneType.OFFSET, "offset" : 9 * mm, "oppositeDirection" : true, "width" : 150 * mm, "height" : 150 * mm});
        }
        {
            var Q0;
            Q0=qCreatedBy(id+"F33.planeOp",FACE);
            var sketch = newSketch(context, id + "F34", { "sketchPlane" : qUnion([Q0])});
            skCircle(sketch, "E864", {"center": v(-29.86, -30.9) * mm, "radius": 1.22 * mm});
            skCircle(sketch, "E865", {"center": v(-29.84, 14.65) * mm, "radius": 1.25 * mm});
            skSolve(sketch);
        }
        {
            var Q0;
            Q0=qSketchRegion(id+"F34",true);
            var Q1;
            Q1=makeQuery(id+"F3.boolean.opBoolean","COPY",FACE,{"derivedFrom":makeQuery(id+"F3.opExtrude","SWEPT_FACE",FACE,{"disambiguationData":[OSD([sQuery(id+"F2.wireOp",EDGE,"E14")])]})});
            extrude(context, id + "F35", {"entities" : qUnion([Q0]), "operationType" : NewBodyOperationType.ADD, "endBound" : BoundingType.UP_TO_SURFACE, "endBoundEntityFace" : qUnion([Q1]), "depth" : 25 * mm});
        }
        {
            var Q0;
            {var subQ0=sQuery(id+"F0.wireOp",EDGE,"E7.rect.right");var subQ1=sQuery(id+"F0.wireOp",EDGE,"E7.rect.left");var subQ2=sQuery(id+"F0.wireOp",EDGE,"E7.rect.top");var subQ3=sQuery(id+"F0.wireOp",EDGE,"E7.rect.bottom");var subQ4=sQuery(id+"F0.wireOp",EDGE,"E5.MirrorC");var subQ5=sQuery(id+"F0.wireOp",EDGE,"E3");var subQ6=sQuery(id+"F0.wireOp",EDGE,"E2");var subQ7=sQuery(id+"F0.wireOp",EDGE,"E1");Q0=makeQuery(id+"F28.boolean.opBoolean","SPLIT",FACE,{"disambiguationData":[TD([makeQuery(id+"F4.opFillet","BLEND_FACE",FACE,{"disambiguationData":[OSD([subQ3])]})])],"derivedFrom":makeQuery(id+"F1.opExtrude","CAP_FACE",FACE,{"disambiguationData":[OSD([subQ7,subQ6,subQ5,subQ4,subQ3,subQ2,subQ1,subQ0])],"isStart":false})});}
            cPlane(context, id + "F36", {"entities" : qUnion([Q0]), "cplaneType" : CPlaneType.OFFSET, "offset" : 17.5 * mm, "oppositeDirection" : true, "width" : 150 * mm, "height" : 150 * mm});
        }
        {
            var Q0;
            Q0=qCreatedBy(id+"F36.planeOp",FACE);
            var sketch = newSketch(context, id + "F37", { "sketchPlane" : qUnion([Q0])});
            skCircle(sketch, "E866", {"center": v(8.9, 3.98) * mm, "radius": 1.26 * mm});
            skCircle(sketch, "E867", {"center": v(15.8, -30.92) * mm, "radius": 1.17 * mm});
            skSolve(sketch);
        }
        {
            var Q0;
            Q0=qSketchRegion(id+"F37",true);
            var Q1;
            {var subQ0=sQuery(id+"F2.wireOp",EDGE,"E22");var subQ1=sQuery(id+"F2.wireOp",EDGE,"E20");Q1=makeQuery(id+"F24.boolean.opBoolean","SPLIT",FACE,{"disambiguationData":[TD([makeQuery(id+"F1.opExtrude","SWEPT_FACE",FACE,{"disambiguationData":[OSD([sQuery(id+"F0.wireOp",EDGE,"E3")])]})])],"derivedFrom":makeQuery(id+"F3.boolean.opBoolean","COPY",FACE,{"derivedFrom":makeQuery(id+"F3.opExtrude","SWEPT_FACE",FACE,{"disambiguationData":[OSD([subQ1,subQ0])]})})});}
            extrude(context, id + "F38", {"entities" : qUnion([Q0]), "operationType" : NewBodyOperationType.ADD, "endBound" : BoundingType.UP_TO_SURFACE, "endBoundEntityFace" : qUnion([Q1]), "depth" : 25 * mm});
        }
        {
            var Q0;
            Q0=makeQuery(id+"F1.opExtrude","SWEPT_FACE",FACE,{"disambiguationData":[OSD([sQuery(id+"F0.wireOp",EDGE,"E7.rect.bottom")])]});
            cPlane(context, id + "F39", {"entities" : qUnion([Q0]), "cplaneType" : CPlaneType.OFFSET, "offset" : 1.8 * mm, "oppositeDirection" : true, "width" : 150 * mm, "height" : 150 * mm});
        }
        {
            var Q0;
            Q0=qCreatedBy(id+"F39.planeOp",FACE);
            var sketch = newSketch(context, id + "F40", { "sketchPlane" : qUnion([Q0])});
            skLineSegment(sketch, "E868.top", {"start": v(-5.27, 0) * mm, "end": v(12.86, 0) * mm});
            skLineSegment(sketch, "E869.right", {"start": v(12.86, 5.48) * mm, "end": v(12.86, 0) * mm});
            skLineSegment(sketch, "E870.bottom", {"start": v(12.86, 0) * mm, "end": v(-5.27, 0) * mm});
            skLineSegment(sketch, "E870.top", {"start": v(12.86, 5.48) * mm, "end": v(-5.27, 5.48) * mm});
            skLineSegment(sketch, "E870.left", {"start": v(12.86, 0) * mm, "end": v(12.86, 5.48) * mm});
            skPoint(sketch, "E871.orphan", {"position": v(14.06, 0) * mm});
            skLineSegment(sketch, "E872", {"start": v(-5.27, 5.48) * mm, "end": v(-8, 5.48) * mm});
            skLineSegment(sketch, "E873", {"start": v(-8, 5.48) * mm, "end": v(-8, 0) * mm});
            skLineSegment(sketch, "E874", {"start": v(-8, 0) * mm, "end": v(-5.27, 0) * mm});
            skSolve(sketch);
        }
        {
            var Q0;
            Q0=qSketchRegion(id+"F40",true);
            extrude(context, id + "F41", {"entities" : qUnion([Q0]), "operationType" : NewBodyOperationType.REMOVE, "depth" : 1.2 * mm});
        }
        {
            var Q0;
            Q0=qCreatedBy(makeId("Top.planeOp"),FACE);
            var sketch = newSketch(context, id + "F42", { "sketchPlane" : qUnion([Q0])});
            skLineSegment(sketch, "E875.bottom", {"start": v(-10.2, -20.34) * mm, "end": v(-23.5, -20.34) * mm});
            skLineSegment(sketch, "E875.top", {"start": v(-9.76, -20.7) * mm, "end": v(-23.91, -20.7) * mm});
            skLineSegment(sketch, "E875.left", {"start": v(-9.76, -20.34) * mm, "end": v(-9.76, -20.7) * mm});
            skLineSegment(sketch, "E876", {"start": v(-9.76, -19.58) * mm, "end": v(-9.76, 2.28) * mm});
            skLineSegment(sketch, "E877.bottom", {"start": v(-10.2, 2.28) * mm, "end": v(-23.5, 2.28) * mm});
            skLineSegment(sketch, "E877.top", {"start": v(-9.76, 2.58) * mm, "end": v(-23.91, 2.58) * mm});
            skLineSegment(sketch, "E877.left", {"start": v(-9.76, 2.28) * mm, "end": v(-9.76, 2.58) * mm});
            skLineSegment(sketch, "E877.right", {"start": v(-23.91, 2.28) * mm, "end": v(-23.91, 2.58) * mm});
            skLineSegment(sketch, "E878.bottom", {"start": v(-10.2, -10.06) * mm, "end": v(-23.5, -10.06) * mm});
            skLineSegment(sketch, "E878.top", {"start": v(-10.2, -9.35) * mm, "end": v(-23.5, -9.35) * mm});
            skLineSegment(sketch, "E878.left", {"start": v(-9.76, -10.06) * mm, "end": v(-9.76, -9.35) * mm});
            skLineSegment(sketch, "E878.right", {"start": v(-25.9, -10.06) * mm, "end": v(-25.9, -9.35) * mm});
            skLineSegment(sketch, "E879", {"start": v(-10.2, -19.58) * mm, "end": v(-10.2, -10.06) * mm});
            skLineSegment(sketch, "E880.bottom", {"start": v(-23.91, 2.58) * mm, "end": v(-23.5, 2.58) * mm});
            skLineSegment(sketch, "E880.top", {"start": v(-23.91, -20.7) * mm, "end": v(-23.5, -20.7) * mm});
            skLineSegment(sketch, "E880.left", {"start": v(-23.91, 2.58) * mm, "end": v(-23.91, 2.28) * mm});
            skLineSegment(sketch, "E880.right", {"start": v(-23.5, 1.67) * mm, "end": v(-23.5, -9.35) * mm});
            skLineSegment(sketch, "E881.trimOffspring", {"start": v(-10.2, -9.35) * mm, "end": v(-10.2, 2.28) * mm});
            skLineSegment(sketch, "E882.trimOffspring", {"start": v(-23.91, -10.06) * mm, "end": v(-25.9, -10.06) * mm});
            skLineSegment(sketch, "E883.trimOffspring", {"start": v(-23.91, -10.06) * mm, "end": v(-23.91, -20.7) * mm});
            skLineSegment(sketch, "E884.trimOffspring", {"start": v(-23.5, -10.06) * mm, "end": v(-23.5, -20.34) * mm});
            skLineSegment(sketch, "E885.trimOffspring", {"start": v(-23.91, -9.35) * mm, "end": v(-25.9, -9.35) * mm});
            skLineSegment(sketch, "E886", {"start": v(-10.2, -19.58) * mm, "end": v(-9.76, -19.58) * mm});
            skLineSegment(sketch, "E887", {"start": v(-10.2, -20.34) * mm, "end": v(-9.76, -20.34) * mm});
            skLineSegment(sketch, "E888", {"start": v(-23.5, 2.28) * mm, "end": v(-23.91, 2.28) * mm});
            skLineSegment(sketch, "E889", {"start": v(-23.5, 1.67) * mm, "end": v(-23.91, 1.67) * mm});
            skLineSegment(sketch, "E890.trimOffspring", {"start": v(-23.91, 1.67) * mm, "end": v(-23.91, -9.35) * mm});
            skSolve(sketch);
        }
        {
            var Q0;
            Q0=qSketchRegion(id+"F42",true);
            var Q1;
            {var subQ0=sQuery(id+"F27.wireOp",EDGE,"E849");var subQ1=sQuery(id+"F27.wireOp",EDGE,"E848");var subQ2=sQuery(id+"F27.wireOp",EDGE,"E847");var subQ3=sQuery(id+"F27.wireOp",EDGE,"E846");var subQ4=sQuery(id+"F27.wireOp",EDGE,"E845");var subQ5=sQuery(id+"F27.wireOp",EDGE,"E844");var subQ6=sQuery(id+"F27.wireOp",EDGE,"E843");var subQ7=sQuery(id+"F27.wireOp",EDGE,"E842");var subQ8=sQuery(id+"F27.wireOp",EDGE,"E841");var subQ9=sQuery(id+"F27.wireOp",EDGE,"E840");var subQ10=sQuery(id+"F27.wireOp",EDGE,"E839");var subQ11=sQuery(id+"F27.wireOp",EDGE,"E838");var subQ12=sQuery(id+"F27.wireOp",EDGE,"E837");var subQ13=sQuery(id+"F27.wireOp",EDGE,"E836");var subQ14=sQuery(id+"F27.wireOp",EDGE,"E835");var subQ15=sQuery(id+"F27.wireOp",EDGE,"E834");var subQ16=sQuery(id+"F27.wireOp",EDGE,"E833");var subQ17=sQuery(id+"F27.wireOp",EDGE,"E832");var subQ18=sQuery(id+"F27.wireOp",EDGE,"E831");var subQ19=sQuery(id+"F27.wireOp",EDGE,"E830");var subQ20=sQuery(id+"F27.wireOp",EDGE,"E829");var subQ21=sQuery(id+"F27.wireOp",EDGE,"E828");var subQ22=sQuery(id+"F27.wireOp",EDGE,"E827");var subQ23=sQuery(id+"F27.wireOp",EDGE,"E826");var subQ24=sQuery(id+"F27.wireOp",EDGE,"E825");var subQ25=sQuery(id+"F27.wireOp",EDGE,"E824");var subQ26=sQuery(id+"F27.wireOp",EDGE,"E823");var subQ27=sQuery(id+"F27.wireOp",EDGE,"E822");var subQ28=sQuery(id+"F27.wireOp",EDGE,"E821");var subQ29=sQuery(id+"F27.wireOp",EDGE,"E820");var subQ30=sQuery(id+"F27.wireOp",EDGE,"E819");var subQ31=sQuery(id+"F27.wireOp",EDGE,"E818");var subQ32=sQuery(id+"F27.wireOp",EDGE,"E817");var subQ33=sQuery(id+"F27.wireOp",EDGE,"E816");var subQ34=sQuery(id+"F27.wireOp",EDGE,"E815");var subQ35=sQuery(id+"F27.wireOp",EDGE,"E814");var subQ36=sQuery(id+"F27.wireOp",EDGE,"E813");var subQ37=sQuery(id+"F27.wireOp",EDGE,"E812");var subQ38=sQuery(id+"F27.wireOp",EDGE,"E811");var subQ39=sQuery(id+"F27.wireOp",EDGE,"E810");var subQ40=sQuery(id+"F27.wireOp",EDGE,"E809");var subQ41=sQuery(id+"F27.wireOp",EDGE,"E808");var subQ42=sQuery(id+"F27.wireOp",EDGE,"E807");var subQ43=sQuery(id+"F27.wireOp",EDGE,"E806");var subQ44=sQuery(id+"F27.wireOp",EDGE,"E805");var subQ45=sQuery(id+"F27.wireOp",EDGE,"E804");var subQ46=sQuery(id+"F27.wireOp",EDGE,"E803");var subQ47=sQuery(id+"F27.wireOp",EDGE,"E802");var subQ48=sQuery(id+"F27.wireOp",EDGE,"E801");var subQ49=sQuery(id+"F27.wireOp",EDGE,"E800");var subQ50=sQuery(id+"F27.wireOp",EDGE,"E799");var subQ51=sQuery(id+"F27.wireOp",EDGE,"E798");var subQ52=sQuery(id+"F27.wireOp",EDGE,"E797");var subQ53=sQuery(id+"F27.wireOp",EDGE,"E796");var subQ54=sQuery(id+"F27.wireOp",EDGE,"E795");var subQ55=sQuery(id+"F27.wireOp",EDGE,"E794");var subQ56=sQuery(id+"F27.wireOp",EDGE,"E793");var subQ57=sQuery(id+"F27.wireOp",EDGE,"E792");var subQ58=sQuery(id+"F27.wireOp",EDGE,"E791");var subQ59=sQuery(id+"F27.wireOp",EDGE,"E790");var subQ60=sQuery(id+"F27.wireOp",EDGE,"E789");var subQ61=sQuery(id+"F27.wireOp",EDGE,"E788");var subQ62=sQuery(id+"F27.wireOp",EDGE,"E787");var subQ63=sQuery(id+"F27.wireOp",EDGE,"E786");var subQ64=sQuery(id+"F27.wireOp",EDGE,"E785");var subQ65=sQuery(id+"F27.wireOp",EDGE,"E784");var subQ66=sQuery(id+"F27.wireOp",EDGE,"E783");var subQ67=sQuery(id+"F27.wireOp",EDGE,"E782");var subQ68=sQuery(id+"F27.wireOp",EDGE,"E781");var subQ69=sQuery(id+"F27.wireOp",EDGE,"E780");var subQ70=sQuery(id+"F27.wireOp",EDGE,"E779");var subQ71=sQuery(id+"F27.wireOp",EDGE,"E778");var subQ72=sQuery(id+"F27.wireOp",EDGE,"E777");var subQ73=sQuery(id+"F27.wireOp",EDGE,"E776");var subQ74=sQuery(id+"F27.wireOp",EDGE,"E775");var subQ75=sQuery(id+"F27.wireOp",EDGE,"E774");var subQ76=sQuery(id+"F27.wireOp",EDGE,"E773");var subQ77=sQuery(id+"F27.wireOp",EDGE,"E772");var subQ78=sQuery(id+"F27.wireOp",EDGE,"E771");var subQ79=sQuery(id+"F27.wireOp",EDGE,"E770");var subQ80=sQuery(id+"F27.wireOp",EDGE,"E769");var subQ81=sQuery(id+"F27.wireOp",EDGE,"E768");var subQ82=sQuery(id+"F27.wireOp",EDGE,"E767");var subQ83=sQuery(id+"F27.wireOp",EDGE,"E766");var subQ84=sQuery(id+"F27.wireOp",EDGE,"E765");var subQ85=sQuery(id+"F27.wireOp",EDGE,"E764");var subQ86=sQuery(id+"F27.wireOp",EDGE,"E763");var subQ87=sQuery(id+"F27.wireOp",EDGE,"E762");var subQ88=sQuery(id+"F27.wireOp",EDGE,"E761");var subQ89=sQuery(id+"F27.wireOp",EDGE,"E760");var subQ90=sQuery(id+"F27.wireOp",EDGE,"E759");var subQ91=sQuery(id+"F27.wireOp",EDGE,"E758");var subQ92=sQuery(id+"F27.wireOp",EDGE,"E757");var subQ93=sQuery(id+"F27.wireOp",EDGE,"E756");var subQ94=sQuery(id+"F27.wireOp",EDGE,"E755");var subQ95=sQuery(id+"F27.wireOp",EDGE,"E754");var subQ96=sQuery(id+"F27.wireOp",EDGE,"E753");var subQ97=sQuery(id+"F27.wireOp",EDGE,"E752");var subQ98=sQuery(id+"F27.wireOp",EDGE,"E751");var subQ99=sQuery(id+"F27.wireOp",EDGE,"E750");var subQ100=sQuery(id+"F27.wireOp",EDGE,"E749");var subQ101=sQuery(id+"F27.wireOp",EDGE,"E748");var subQ102=sQuery(id+"F27.wireOp",EDGE,"E747");var subQ103=sQuery(id+"F27.wireOp",EDGE,"E746");var subQ104=sQuery(id+"F27.wireOp",EDGE,"E745");var subQ105=sQuery(id+"F27.wireOp",EDGE,"E744");var subQ106=sQuery(id+"F27.wireOp",EDGE,"E743");var subQ107=sQuery(id+"F27.wireOp",EDGE,"E742");var subQ108=sQuery(id+"F27.wireOp",EDGE,"E741");var subQ109=sQuery(id+"F27.wireOp",EDGE,"E740");var subQ110=sQuery(id+"F27.wireOp",EDGE,"E739");var subQ111=sQuery(id+"F27.wireOp",EDGE,"E738");var subQ112=sQuery(id+"F27.wireOp",EDGE,"E737");var subQ113=sQuery(id+"F27.wireOp",EDGE,"E736");var subQ114=sQuery(id+"F27.wireOp",EDGE,"E735");var subQ115=sQuery(id+"F27.wireOp",EDGE,"E734");var subQ116=sQuery(id+"F27.wireOp",EDGE,"E733");var subQ117=sQuery(id+"F27.wireOp",EDGE,"E732");var subQ118=sQuery(id+"F27.wireOp",EDGE,"E731");var subQ119=sQuery(id+"F27.wireOp",EDGE,"E730");var subQ120=sQuery(id+"F27.wireOp",EDGE,"E729");var subQ121=sQuery(id+"F27.wireOp",EDGE,"E728");var subQ122=sQuery(id+"F27.wireOp",EDGE,"E727");var subQ123=sQuery(id+"F27.wireOp",EDGE,"E726");var subQ124=sQuery(id+"F27.wireOp",EDGE,"E725");var subQ125=sQuery(id+"F27.wireOp",EDGE,"E724");var subQ126=sQuery(id+"F27.wireOp",EDGE,"E723");var subQ127=sQuery(id+"F27.wireOp",EDGE,"E722");var subQ128=sQuery(id+"F27.wireOp",EDGE,"E721");var subQ129=sQuery(id+"F27.wireOp",EDGE,"E720");var subQ130=sQuery(id+"F27.wireOp",EDGE,"E719");var subQ131=sQuery(id+"F27.wireOp",EDGE,"E718");var subQ132=sQuery(id+"F27.wireOp",EDGE,"E717");var subQ133=sQuery(id+"F27.wireOp",EDGE,"E716");var subQ134=sQuery(id+"F27.wireOp",EDGE,"E715");var subQ135=sQuery(id+"F27.wireOp",EDGE,"E714");var subQ136=sQuery(id+"F27.wireOp",EDGE,"E713");var subQ137=sQuery(id+"F27.wireOp",EDGE,"E712");var subQ138=sQuery(id+"F27.wireOp",EDGE,"E711");var subQ139=sQuery(id+"F27.wireOp",EDGE,"E710");var subQ140=sQuery(id+"F27.wireOp",EDGE,"E709");var subQ141=sQuery(id+"F27.wireOp",EDGE,"E708");var subQ142=sQuery(id+"F27.wireOp",EDGE,"E707");var subQ143=sQuery(id+"F27.wireOp",EDGE,"E706");var subQ144=sQuery(id+"F27.wireOp",EDGE,"E705");var subQ145=sQuery(id+"F27.wireOp",EDGE,"E704");var subQ146=sQuery(id+"F27.wireOp",EDGE,"E703");var subQ147=sQuery(id+"F27.wireOp",EDGE,"E702");var subQ148=sQuery(id+"F27.wireOp",EDGE,"E701");var subQ149=sQuery(id+"F27.wireOp",EDGE,"E700");var subQ150=sQuery(id+"F27.wireOp",EDGE,"E699");var subQ151=sQuery(id+"F27.wireOp",EDGE,"E698");var subQ152=sQuery(id+"F27.wireOp",EDGE,"E697");var subQ153=sQuery(id+"F27.wireOp",EDGE,"E696");var subQ154=sQuery(id+"F27.wireOp",EDGE,"E695");var subQ155=sQuery(id+"F27.wireOp",EDGE,"E694");var subQ156=sQuery(id+"F27.wireOp",EDGE,"E693");var subQ157=sQuery(id+"F27.wireOp",EDGE,"E692");var subQ158=sQuery(id+"F27.wireOp",EDGE,"E691");var subQ159=sQuery(id+"F27.wireOp",EDGE,"E690");var subQ160=sQuery(id+"F27.wireOp",EDGE,"E689");var subQ161=sQuery(id+"F27.wireOp",EDGE,"E688");var subQ162=sQuery(id+"F27.wireOp",EDGE,"E687");var subQ163=sQuery(id+"F27.wireOp",EDGE,"E686");var subQ164=sQuery(id+"F27.wireOp",EDGE,"E685");var subQ165=sQuery(id+"F27.wireOp",EDGE,"E684");var subQ166=sQuery(id+"F27.wireOp",EDGE,"E683");var subQ167=sQuery(id+"F27.wireOp",EDGE,"E682");var subQ168=sQuery(id+"F27.wireOp",EDGE,"E681");var subQ169=sQuery(id+"F27.wireOp",EDGE,"E680");var subQ170=sQuery(id+"F27.wireOp",EDGE,"E679");var subQ171=sQuery(id+"F27.wireOp",EDGE,"E678");var subQ172=sQuery(id+"F27.wireOp",EDGE,"E677");var subQ173=sQuery(id+"F27.wireOp",EDGE,"E676");var subQ174=sQuery(id+"F27.wireOp",EDGE,"E675");var subQ175=sQuery(id+"F27.wireOp",EDGE,"E674");var subQ176=sQuery(id+"F27.wireOp",EDGE,"E673");var subQ177=sQuery(id+"F27.wireOp",EDGE,"E672");var subQ178=sQuery(id+"F27.wireOp",EDGE,"E671");var subQ179=sQuery(id+"F27.wireOp",EDGE,"E670");var subQ180=sQuery(id+"F27.wireOp",EDGE,"E669");var subQ181=sQuery(id+"F27.wireOp",EDGE,"E668");var subQ182=sQuery(id+"F27.wireOp",EDGE,"E667");var subQ183=sQuery(id+"F27.wireOp",EDGE,"E666");var subQ184=sQuery(id+"F27.wireOp",EDGE,"E665");var subQ185=sQuery(id+"F27.wireOp",EDGE,"E664");var subQ186=sQuery(id+"F27.wireOp",EDGE,"E663");var subQ187=sQuery(id+"F27.wireOp",EDGE,"E662");var subQ188=sQuery(id+"F27.wireOp",EDGE,"E661");var subQ189=sQuery(id+"F27.wireOp",EDGE,"E660");var subQ190=sQuery(id+"F27.wireOp",EDGE,"E659");var subQ191=sQuery(id+"F27.wireOp",EDGE,"E658");var subQ192=sQuery(id+"F27.wireOp",EDGE,"E657");var subQ193=sQuery(id+"F27.wireOp",EDGE,"E656");var subQ194=sQuery(id+"F27.wireOp",EDGE,"E655");var subQ195=sQuery(id+"F27.wireOp",EDGE,"E858");var subQ196=sQuery(id+"F27.wireOp",EDGE,"E857");var subQ197=sQuery(id+"F27.wireOp",EDGE,"E856");var subQ198=sQuery(id+"F27.wireOp",EDGE,"E854");var subQ199=sQuery(id+"F27.wireOp",EDGE,"E853");var subQ200=sQuery(id+"F27.wireOp",EDGE,"E850");var subQ201=sQuery(id+"F27.wireOp",EDGE,"E325");var subQ202=sQuery(id+"F27.wireOp",EDGE,"E324");var subQ203=sQuery(id+"F27.wireOp",EDGE,"E323");var subQ204=sQuery(id+"F27.wireOp",EDGE,"E321");var subQ205=sQuery(id+"F27.wireOp",EDGE,"E320");var subQ206=sQuery(id+"F27.wireOp",EDGE,"E319");var subQ207=sQuery(id+"F27.wireOp",EDGE,"E318");var subQ208=sQuery(id+"F27.wireOp",EDGE,"E317");var subQ209=sQuery(id+"F27.wireOp",EDGE,"E316");var subQ210=sQuery(id+"F27.wireOp",EDGE,"E315");var subQ211=sQuery(id+"F27.wireOp",EDGE,"E314");var subQ212=sQuery(id+"F27.wireOp",EDGE,"E313");var subQ213=sQuery(id+"F27.wireOp",EDGE,"E312");var subQ214=sQuery(id+"F27.wireOp",EDGE,"E311");var subQ215=sQuery(id+"F27.wireOp",EDGE,"E310");var subQ216=sQuery(id+"F27.wireOp",EDGE,"E309");var subQ217=sQuery(id+"F27.wireOp",EDGE,"E308");var subQ218=sQuery(id+"F27.wireOp",EDGE,"E307");var subQ219=sQuery(id+"F27.wireOp",EDGE,"E306");var subQ220=sQuery(id+"F27.wireOp",EDGE,"E305");var subQ221=sQuery(id+"F27.wireOp",EDGE,"E304");var subQ222=sQuery(id+"F27.wireOp",EDGE,"E303");var subQ223=sQuery(id+"F27.wireOp",EDGE,"E302");var subQ224=sQuery(id+"F27.wireOp",EDGE,"E301");var subQ225=sQuery(id+"F27.wireOp",EDGE,"E300");var subQ226=sQuery(id+"F27.wireOp",EDGE,"E299");var subQ227=sQuery(id+"F27.wireOp",EDGE,"E298");var subQ228=sQuery(id+"F27.wireOp",EDGE,"E297");var subQ229=sQuery(id+"F27.wireOp",EDGE,"E296");var subQ230=sQuery(id+"F27.wireOp",EDGE,"E295");var subQ231=sQuery(id+"F27.wireOp",EDGE,"E294");var subQ232=sQuery(id+"F27.wireOp",EDGE,"E293");var subQ233=sQuery(id+"F27.wireOp",EDGE,"E292");var subQ234=sQuery(id+"F27.wireOp",EDGE,"E291");var subQ235=sQuery(id+"F27.wireOp",EDGE,"E290");var subQ236=sQuery(id+"F27.wireOp",EDGE,"E289");var subQ237=sQuery(id+"F27.wireOp",EDGE,"E288");var subQ238=sQuery(id+"F27.wireOp",EDGE,"E287");var subQ239=sQuery(id+"F27.wireOp",EDGE,"E286");var subQ240=sQuery(id+"F27.wireOp",EDGE,"E285");var subQ241=sQuery(id+"F27.wireOp",EDGE,"E284");var subQ242=sQuery(id+"F27.wireOp",EDGE,"E283");var subQ243=sQuery(id+"F27.wireOp",EDGE,"E282");var subQ244=sQuery(id+"F27.wireOp",EDGE,"E281");var subQ245=sQuery(id+"F27.wireOp",EDGE,"E280");var subQ246=sQuery(id+"F27.wireOp",EDGE,"E279");var subQ247=sQuery(id+"F27.wireOp",EDGE,"E278");var subQ248=sQuery(id+"F27.wireOp",EDGE,"E277");var subQ249=sQuery(id+"F27.wireOp",EDGE,"E276");var subQ250=sQuery(id+"F27.wireOp",EDGE,"E275");var subQ251=sQuery(id+"F27.wireOp",EDGE,"E274");var subQ252=sQuery(id+"F27.wireOp",EDGE,"E273");var subQ253=sQuery(id+"F27.wireOp",EDGE,"E272");var subQ254=sQuery(id+"F27.wireOp",EDGE,"E271");var subQ255=sQuery(id+"F27.wireOp",EDGE,"E270");var subQ256=sQuery(id+"F27.wireOp",EDGE,"E269");var subQ257=sQuery(id+"F27.wireOp",EDGE,"E268");var subQ258=sQuery(id+"F27.wireOp",EDGE,"E267");var subQ259=sQuery(id+"F27.wireOp",EDGE,"E266");var subQ260=sQuery(id+"F27.wireOp",EDGE,"E265");var subQ261=sQuery(id+"F27.wireOp",EDGE,"E264");var subQ262=sQuery(id+"F27.wireOp",EDGE,"E263");var subQ263=sQuery(id+"F27.wireOp",EDGE,"E262");var subQ264=sQuery(id+"F27.wireOp",EDGE,"E261");var subQ265=sQuery(id+"F27.wireOp",EDGE,"E260");var subQ266=sQuery(id+"F27.wireOp",EDGE,"E259");var subQ267=sQuery(id+"F27.wireOp",EDGE,"E258");var subQ268=sQuery(id+"F27.wireOp",EDGE,"E257");var subQ269=sQuery(id+"F27.wireOp",EDGE,"E256");var subQ270=sQuery(id+"F27.wireOp",EDGE,"E255");var subQ271=sQuery(id+"F27.wireOp",EDGE,"E254");var subQ272=sQuery(id+"F27.wireOp",EDGE,"E253");var subQ273=sQuery(id+"F27.wireOp",EDGE,"E252");var subQ274=sQuery(id+"F27.wireOp",EDGE,"E251");var subQ275=sQuery(id+"F27.wireOp",EDGE,"E250");var subQ276=sQuery(id+"F27.wireOp",EDGE,"E249");var subQ277=sQuery(id+"F27.wireOp",EDGE,"E248");var subQ278=sQuery(id+"F27.wireOp",EDGE,"E247");var subQ279=sQuery(id+"F27.wireOp",EDGE,"E246");var subQ280=sQuery(id+"F27.wireOp",EDGE,"E245");var subQ281=sQuery(id+"F27.wireOp",EDGE,"E244");var subQ282=sQuery(id+"F27.wireOp",EDGE,"E243");var subQ283=sQuery(id+"F27.wireOp",EDGE,"E242");var subQ284=sQuery(id+"F27.wireOp",EDGE,"E241");var subQ285=sQuery(id+"F27.wireOp",EDGE,"E182");var subQ286=sQuery(id+"F27.wireOp",EDGE,"E181");var subQ287=sQuery(id+"F27.wireOp",EDGE,"E180");var subQ288=sQuery(id+"F27.wireOp",EDGE,"E179");var subQ289=sQuery(id+"F27.wireOp",EDGE,"E178");var subQ290=sQuery(id+"F27.wireOp",EDGE,"E177");var subQ291=sQuery(id+"F27.wireOp",EDGE,"E176");var subQ292=sQuery(id+"F27.wireOp",EDGE,"E175");var subQ293=sQuery(id+"F27.wireOp",EDGE,"E174");var subQ294=sQuery(id+"F27.wireOp",EDGE,"E173");var subQ295=sQuery(id+"F27.wireOp",EDGE,"E172");var subQ296=sQuery(id+"F27.wireOp",EDGE,"E171");var subQ297=sQuery(id+"F27.wireOp",EDGE,"E170");var subQ298=sQuery(id+"F27.wireOp",EDGE,"E123");var subQ299=sQuery(id+"F0.wireOp",EDGE,"E7.rect.bottom");var subQ302=sQuery(id+"F0.wireOp",EDGE,"E7.rect.right");var subQ303=sQuery(id+"F0.wireOp",EDGE,"E7.rect.left");var subQ304=sQuery(id+"F0.wireOp",EDGE,"E7.rect.top");var subQ305=sQuery(id+"F0.wireOp",EDGE,"E5.MirrorC");var subQ306=sQuery(id+"F0.wireOp",EDGE,"E3");var subQ307=sQuery(id+"F0.wireOp",EDGE,"E2");var subQ308=sQuery(id+"F0.wireOp",EDGE,"E1");var subQ309=makeQuery(id+"F1.opExtrude","CAP_FACE",FACE,{"disambiguationData":[OSD([subQ308,subQ307,subQ306,subQ305,subQ299,subQ304,subQ303,subQ302])],"isStart":false});var subQ312=makeQuery(id+"F6.opShell","OFFSET_FACE",FACE,{"disambiguationData":[OSD([subQ308,subQ307,subQ306,subQ305,subQ299,subQ304,subQ303,subQ302]),TDD([subQ309])]});Q1=makeQuery(id+"F29.boolean.opBoolean","MERGE",FACE,{"derivedFrom":[makeQuery(id+"F28.boolean.opBoolean","SPLIT",FACE,{"disambiguationData":[TD([makeQuery(id+"F28.opExtrude","SWEPT_FACE",FACE,{"disambiguationData":[OSD([subQ298])]})])],"derivedFrom":subQ312}),makeQuery(id+"F28.boolean.opBoolean","SPLIT",FACE,{"disambiguationData":[TD([makeQuery(id+"F28.opExtrude","SWEPT_FACE",FACE,{"disambiguationData":[OSD([subQ262])]})])],"derivedFrom":subQ312}),makeQuery(id+"F28.boolean.opBoolean","SPLIT",FACE,{"disambiguationData":[TD([makeQuery(id+"F28.opExtrude","SWEPT_FACE",FACE,{"disambiguationData":[OSD([subQ297])]})])],"derivedFrom":subQ312}),makeQuery(id+"F29.opExtrude","CAP_FACE",FACE,{"disambiguationData":[OSD([subQ298,sQuery(id+"F27.wireOp",EDGE,"E124"),sQuery(id+"F27.wireOp",EDGE,"E125"),sQuery(id+"F27.wireOp",EDGE,"E126"),sQuery(id+"F27.wireOp",EDGE,"E127"),sQuery(id+"F27.wireOp",EDGE,"E128"),sQuery(id+"F27.wireOp",EDGE,"E129"),sQuery(id+"F27.wireOp",EDGE,"E130"),sQuery(id+"F27.wireOp",EDGE,"E131"),sQuery(id+"F27.wireOp",EDGE,"E132"),sQuery(id+"F27.wireOp",EDGE,"E133"),sQuery(id+"F27.wireOp",EDGE,"E134"),sQuery(id+"F27.wireOp",EDGE,"E135"),sQuery(id+"F27.wireOp",EDGE,"E136"),sQuery(id+"F27.wireOp",EDGE,"E137"),sQuery(id+"F27.wireOp",EDGE,"E138"),sQuery(id+"F27.wireOp",EDGE,"E139"),sQuery(id+"F27.wireOp",EDGE,"E140"),sQuery(id+"F27.wireOp",EDGE,"E141"),sQuery(id+"F27.wireOp",EDGE,"E142"),sQuery(id+"F27.wireOp",EDGE,"E143"),sQuery(id+"F27.wireOp",EDGE,"E144"),sQuery(id+"F27.wireOp",EDGE,"E145"),sQuery(id+"F27.wireOp",EDGE,"E146"),sQuery(id+"F27.wireOp",EDGE,"E147"),sQuery(id+"F27.wireOp",EDGE,"E148"),sQuery(id+"F27.wireOp",EDGE,"E149"),sQuery(id+"F27.wireOp",EDGE,"E150"),sQuery(id+"F27.wireOp",EDGE,"E151"),sQuery(id+"F27.wireOp",EDGE,"E152"),sQuery(id+"F27.wireOp",EDGE,"E153"),sQuery(id+"F27.wireOp",EDGE,"E154"),sQuery(id+"F27.wireOp",EDGE,"E155"),sQuery(id+"F27.wireOp",EDGE,"E156"),sQuery(id+"F27.wireOp",EDGE,"E157"),sQuery(id+"F27.wireOp",EDGE,"E158"),sQuery(id+"F27.wireOp",EDGE,"E159"),sQuery(id+"F27.wireOp",EDGE,"E160"),sQuery(id+"F27.wireOp",EDGE,"E161"),sQuery(id+"F27.wireOp",EDGE,"E162"),sQuery(id+"F27.wireOp",EDGE,"E163"),sQuery(id+"F27.wireOp",EDGE,"E164"),sQuery(id+"F27.wireOp",EDGE,"E165"),sQuery(id+"F27.wireOp",EDGE,"E166"),sQuery(id+"F27.wireOp",EDGE,"E167"),sQuery(id+"F27.wireOp",EDGE,"E168"),sQuery(id+"F27.wireOp",EDGE,"E169"),subQ297,subQ296,subQ295,subQ294,subQ293,subQ292,subQ291,subQ290,subQ289,subQ288,subQ287,subQ286,subQ285,sQuery(id+"F27.wireOp",EDGE,"E183"),sQuery(id+"F27.wireOp",EDGE,"E184"),sQuery(id+"F27.wireOp",EDGE,"E185"),sQuery(id+"F27.wireOp",EDGE,"E186"),sQuery(id+"F27.wireOp",EDGE,"E187"),sQuery(id+"F27.wireOp",EDGE,"E188"),sQuery(id+"F27.wireOp",EDGE,"E189"),sQuery(id+"F27.wireOp",EDGE,"E190"),sQuery(id+"F27.wireOp",EDGE,"E191"),sQuery(id+"F27.wireOp",EDGE,"E192"),sQuery(id+"F27.wireOp",EDGE,"E193"),sQuery(id+"F27.wireOp",EDGE,"E194"),sQuery(id+"F27.wireOp",EDGE,"E195"),sQuery(id+"F27.wireOp",EDGE,"E196"),sQuery(id+"F27.wireOp",EDGE,"E197"),sQuery(id+"F27.wireOp",EDGE,"E198"),sQuery(id+"F27.wireOp",EDGE,"E199"),sQuery(id+"F27.wireOp",EDGE,"E200"),sQuery(id+"F27.wireOp",EDGE,"E201"),sQuery(id+"F27.wireOp",EDGE,"E202"),sQuery(id+"F27.wireOp",EDGE,"E203"),sQuery(id+"F27.wireOp",EDGE,"E204"),sQuery(id+"F27.wireOp",EDGE,"E205"),sQuery(id+"F27.wireOp",EDGE,"E206"),sQuery(id+"F27.wireOp",EDGE,"E207"),sQuery(id+"F27.wireOp",EDGE,"E208"),sQuery(id+"F27.wireOp",EDGE,"E209"),sQuery(id+"F27.wireOp",EDGE,"E210"),sQuery(id+"F27.wireOp",EDGE,"E211"),sQuery(id+"F27.wireOp",EDGE,"E212"),sQuery(id+"F27.wireOp",EDGE,"E213"),sQuery(id+"F27.wireOp",EDGE,"E214"),sQuery(id+"F27.wireOp",EDGE,"E215"),sQuery(id+"F27.wireOp",EDGE,"E216"),sQuery(id+"F27.wireOp",EDGE,"E217"),sQuery(id+"F27.wireOp",EDGE,"E218"),sQuery(id+"F27.wireOp",EDGE,"E219"),sQuery(id+"F27.wireOp",EDGE,"E220"),sQuery(id+"F27.wireOp",EDGE,"E221"),sQuery(id+"F27.wireOp",EDGE,"E222"),sQuery(id+"F27.wireOp",EDGE,"E223"),sQuery(id+"F27.wireOp",EDGE,"E224"),sQuery(id+"F27.wireOp",EDGE,"E225"),sQuery(id+"F27.wireOp",EDGE,"E226"),sQuery(id+"F27.wireOp",EDGE,"E227"),sQuery(id+"F27.wireOp",EDGE,"E228"),sQuery(id+"F27.wireOp",EDGE,"E229"),sQuery(id+"F27.wireOp",EDGE,"E230"),sQuery(id+"F27.wireOp",EDGE,"E231"),sQuery(id+"F27.wireOp",EDGE,"E232"),sQuery(id+"F27.wireOp",EDGE,"E233"),sQuery(id+"F27.wireOp",EDGE,"E234"),sQuery(id+"F27.wireOp",EDGE,"E235"),sQuery(id+"F27.wireOp",EDGE,"E236"),sQuery(id+"F27.wireOp",EDGE,"E237"),sQuery(id+"F27.wireOp",EDGE,"E238"),sQuery(id+"F27.wireOp",EDGE,"E239"),sQuery(id+"F27.wireOp",EDGE,"E240"),subQ284,subQ283,subQ282,subQ281,subQ280,subQ279,subQ278,subQ277,subQ276,subQ275,subQ274,subQ273,subQ272,subQ271,subQ270,subQ269,subQ268,subQ267,subQ266,subQ265,subQ264,subQ263,subQ262,subQ261,subQ260,subQ259,subQ258,subQ257,subQ256,subQ255,subQ254,subQ253,subQ252,subQ251,subQ250,subQ249,subQ248,subQ247,subQ246,subQ245,subQ244,subQ243,subQ242,subQ241,subQ240,subQ239,subQ238,subQ237,subQ236,subQ235,subQ234,subQ233,subQ232,subQ231,subQ230,subQ229,subQ228,subQ227,subQ226,subQ225,subQ224,subQ223,subQ222,subQ221,subQ220,subQ219,subQ218,subQ217,subQ216,subQ215,subQ214,subQ213,subQ212,subQ211,subQ210,subQ209,subQ208,subQ207,subQ206,subQ205,subQ204,sQuery(id+"F27.wireOp",EDGE,"E322"),subQ203,subQ202,subQ201,subQ200,sQuery(id+"F27.wireOp",EDGE,"E851"),sQuery(id+"F27.wireOp",EDGE,"E852"),subQ199,subQ198,sQuery(id+"F27.wireOp",EDGE,"E855"),subQ197,subQ196,subQ195])],"isStart":false}),makeQuery(id+"F29.opExtrude","CAP_FACE",FACE,{"disambiguationData":[OSD([subQ194,subQ193,subQ192,subQ191,subQ190,subQ189,subQ188,subQ187,subQ186,subQ185,subQ184,subQ183,subQ182,subQ181,subQ180,subQ179,subQ178,subQ177,subQ176,subQ175,subQ174,subQ173,subQ172,subQ171,subQ170,subQ169,subQ168,subQ167,subQ166,subQ165,subQ164,subQ163,subQ162,subQ161,subQ160,subQ159,subQ158,subQ157,subQ156,subQ155,subQ154,subQ153,subQ152,subQ151,subQ150,subQ149])],"isStart":false}),makeQuery(id+"F29.opExtrude","CAP_FACE",FACE,{"disambiguationData":[OSD([subQ148,subQ147,subQ146,subQ145,subQ144,subQ143,subQ142,subQ141,subQ140,subQ139,subQ138,subQ137,subQ136,subQ135,subQ134,subQ133,subQ132,subQ131,subQ130,subQ129,subQ128,subQ127,subQ126,subQ125,subQ124,subQ123,subQ122,subQ121,subQ120,subQ119,subQ118,subQ117,subQ116,subQ115,subQ114,subQ113,subQ112,subQ111,subQ110,subQ109,subQ108,subQ107,subQ106,subQ105,subQ104,subQ103,subQ102,subQ101,subQ100])],"isStart":false}),makeQuery(id+"F29.opExtrude","CAP_FACE",FACE,{"disambiguationData":[OSD([subQ99,subQ98,subQ97,subQ96,subQ95,subQ94,subQ93,subQ92,subQ91,subQ90,subQ89,subQ88,subQ87,subQ86,subQ85,subQ84,subQ83,subQ82,subQ81,subQ80,subQ79,subQ78,subQ77,subQ76,subQ75,subQ74,subQ73,subQ72,subQ71,subQ70,subQ69,subQ68,subQ67,subQ66,subQ65,subQ64,subQ63,subQ62,subQ61,subQ60,subQ59,subQ58,subQ57,subQ56,subQ55,subQ54,subQ53,subQ52,subQ51,subQ50,subQ49,subQ48,subQ47,subQ46,subQ45,subQ44])],"isStart":false}),makeQuery(id+"F29.opExtrude","CAP_FACE",FACE,{"disambiguationData":[OSD([subQ43,subQ42,subQ41,subQ40,subQ39,subQ38,subQ37,subQ36,subQ35,subQ34,subQ33,subQ32,subQ31,subQ30,subQ29,subQ28,subQ27,subQ26,subQ25,subQ24,subQ23,subQ22,subQ21,subQ20,subQ19,subQ18,subQ17,subQ16,subQ15,subQ14,subQ13,subQ12,subQ11,subQ10,subQ9,subQ8,subQ7,subQ6,subQ5,subQ4,subQ3,subQ2,subQ1,subQ0])],"isStart":false})]});}
            extrude(context, id + "F43", {"entities" : qUnion([Q0]), "operationType" : NewBodyOperationType.ADD, "endBound" : BoundingType.UP_TO_SURFACE, "endBoundEntityFace" : qUnion([Q1]), "depth" : 25 * mm});
        }
        {
            var Q0;
            {var subQ0=sQuery(id+"F0.wireOp",EDGE,"E7.rect.right");var subQ2=sQuery(id+"F0.wireOp",EDGE,"E7.rect.bottom");var subQ3=makeQuery(id+"F1.opExtrude","SWEPT_FACE",FACE,{"disambiguationData":[OSD([subQ2])]});var subQ8=sQuery(id+"F0.wireOp",EDGE,"E7.rect.left");var subQ17=sQuery(id+"F0.wireOp",EDGE,"E7.rect.top");var subQ19=sQuery(id+"F0.wireOp",EDGE,"E5.MirrorC");var subQ20=sQuery(id+"F0.wireOp",EDGE,"E3");var subQ21=sQuery(id+"F0.wireOp",EDGE,"E2");var subQ22=sQuery(id+"F0.wireOp",EDGE,"E1");var subQ23=makeQuery(id+"F1.opExtrude","CAP_FACE",FACE,{"disambiguationData":[OSD([subQ22,subQ21,subQ20,subQ19,subQ2,subQ17,subQ8,subQ0])],"isStart":true});Q0=makeQuery(id+"F26.boolean.opBoolean","MERGE",FACE,{"derivedFrom":[makeQuery(id+"F6.opShell","OFFSET_FACE",FACE,{"disambiguationData":[OSD([subQ22,subQ21,subQ20,subQ19,subQ2,subQ17,subQ8,subQ0]),TDD([subQ23]),OD(2.0)]}),makeQuery(id+"F14.boolean.opBoolean","SPLIT",FACE,{"disambiguationData":[TD([makeQuery(id+"F1.opExtrude","SWEPT_FACE",FACE,{"disambiguationData":[OSD([subQ22])]})])],"derivedFrom":makeQuery(id+"F6.opShell","OFFSET_FACE",FACE,{"disambiguationData":[OSD([subQ22,subQ21,subQ20,subQ19,subQ2,subQ17,subQ8,subQ0]),TDD([subQ23]),OD(0.0)]})}),makeQuery(id+"F14.boolean.opBoolean","SPLIT",FACE,{"disambiguationData":[TD([subQ3])],"derivedFrom":makeQuery(id+"F10.boolean.opBoolean","SPLIT",FACE,{"disambiguationData":[TD([subQ3])],"derivedFrom":makeQuery(id+"F6.opShell","OFFSET_FACE",FACE,{"disambiguationData":[OSD([subQ22,subQ21,subQ20,subQ19,subQ2,subQ17,subQ8,subQ0]),TDD([subQ23]),OD(3.0)]})})}),makeQuery(id+"F26.opExtrude","CAP_FACE",FACE,{"disambiguationData":[OSD([sQuery(id+"F25.wireOp",EDGE,"E102.top"),sQuery(id+"F25.wireOp",EDGE,"E102.left"),sQuery(id+"F25.wireOp",EDGE,"E102.right"),sQuery(id+"F25.wireOp",EDGE,"E103.bottom"),sQuery(id+"F25.wireOp",EDGE,"E103.top"),sQuery(id+"F25.wireOp",EDGE,"E103.right"),sQuery(id+"F25.wireOp",EDGE,"E102.bottom"),sQuery(id+"F25.wireOp",EDGE,"E107.top"),sQuery(id+"F25.wireOp",EDGE,"E107.left"),sQuery(id+"F25.wireOp",EDGE,"E107.right")])],"isStart":true}),makeQuery(id+"F26.opExtrude","CAP_FACE",FACE,{"disambiguationData":[OSD([sQuery(id+"F25.wireOp",EDGE,"E105.bottom"),sQuery(id+"F25.wireOp",EDGE,"E105.top"),sQuery(id+"F25.wireOp",EDGE,"E105.left"),sQuery(id+"F25.wireOp",EDGE,"E105.right"),sQuery(id+"F25.wireOp",EDGE,"E106.bottom"),sQuery(id+"F25.wireOp",EDGE,"E106.top"),sQuery(id+"F25.wireOp",EDGE,"E106.right")])],"isStart":true})]});}
            cPlane(context, id + "F44", {"entities" : qUnion([Q0]), "cplaneType" : CPlaneType.OFFSET, "offset" : 0.6 * mm, "oppositeDirection" : true, "width" : 150 * mm, "height" : 150 * mm});
        }
        {
            var Q0;
            Q0=qCreatedBy(id+"F44.planeOp",FACE);
            var sketch = newSketch(context, id + "F45", { "sketchPlane" : qUnion([Q0])});
            skLineSegment(sketch, "E891.bottom", {"start": v(-24.07, 22.32) * mm, "end": v(-9.14, 22.32) * mm});
            skLineSegment(sketch, "E891.top", {"start": v(-24.07, -4.65) * mm, "end": v(-9.14, -4.65) * mm});
            skLineSegment(sketch, "E891.left", {"start": v(-24.07, 22.32) * mm, "end": v(-24.07, -4.65) * mm});
            skLineSegment(sketch, "E891.right", {"start": v(-9.14, 22.32) * mm, "end": v(-9.14, -4.65) * mm});
            skSolve(sketch);
        }
        {
            var Q0;
            Q0=qSketchRegion(id+"F45",true);
            extrude(context, id + "F46", {"entities" : qUnion([Q0]), "operationType" : NewBodyOperationType.ADD, "depth" : 0.6 * mm});
        }
        {
            var Q0;
            Q0=qCreatedBy(makeId("Top.planeOp"),FACE);
            var sketch = newSketch(context, id + "F47", { "sketchPlane" : qUnion([Q0])});
            skLineSegment(sketch, "E892.bottom", {"start": v(-32.16, -19.74) * mm, "end": v(-31.86, -19.74) * mm});
            skLineSegment(sketch, "E892.top", {"start": v(-32.16, -29.43) * mm, "end": v(-31.86, -29.43) * mm});
            skLineSegment(sketch, "E892.left", {"start": v(-32.16, -19.74) * mm, "end": v(-32.16, -29.43) * mm});
            skLineSegment(sketch, "E892.right", {"start": v(-31.86, -19.74) * mm, "end": v(-31.86, -29.43) * mm});
            skLineSegment(sketch, "E893.bottom", {"start": v(-34.1, 3.13) * mm, "end": v(-31.72, 3.13) * mm});
            skLineSegment(sketch, "E893.top", {"start": v(-34.1, 0.35) * mm, "end": v(-31.72, 0.35) * mm});
            skLineSegment(sketch, "E893.left", {"start": v(-34.1, 3.13) * mm, "end": v(-34.1, 0.35) * mm});
            skLineSegment(sketch, "E893.right", {"start": v(-31.72, 3.13) * mm, "end": v(-31.72, 0.35) * mm});
            skLineSegment(sketch, "E894.bottom", {"start": v(-34.13, -7.9) * mm, "end": v(-31.72, -7.9) * mm});
            skLineSegment(sketch, "E894.top", {"start": v(-34.13, -10.8) * mm, "end": v(-31.72, -10.8) * mm});
            skLineSegment(sketch, "E894.left", {"start": v(-34.13, -7.9) * mm, "end": v(-34.13, -10.8) * mm});
            skLineSegment(sketch, "E894.right", {"start": v(-31.72, -7.9) * mm, "end": v(-31.72, -10.8) * mm});
            skSolve(sketch);
        }
        {
            var Q0;
            Q0=qSketchRegion(id+"F47",true);
            var Q1;
            Q1=makeQuery(id+"F35.boolean.opBoolean","MERGE",FACE,{"derivedFrom":[makeQuery(id+"F3.boolean.opBoolean","COPY",FACE,{"derivedFrom":makeQuery(id+"F3.opExtrude","SWEPT_FACE",FACE,{"disambiguationData":[OSD([sQuery(id+"F2.wireOp",EDGE,"E14")])]})}),makeQuery(id+"F35.opExtrude","CAP_FACE",FACE,{"disambiguationData":[OSD([sQuery(id+"F34.wireOp",EDGE,"E864")])],"isStart":false}),makeQuery(id+"F35.opExtrude","CAP_FACE",FACE,{"disambiguationData":[OSD([sQuery(id+"F34.wireOp",EDGE,"E865")])],"isStart":false})]});
            extrude(context, id + "F48", {"entities" : qUnion([Q0]), "operationType" : NewBodyOperationType.ADD, "endBound" : BoundingType.UP_TO_SURFACE, "endBoundEntityFace" : qUnion([Q1]), "depth" : 25 * mm});
        }
        {
            var Q0;
            Q0=makeQuery(id+"F35.boolean.opBoolean","MERGE",FACE,{"derivedFrom":[makeQuery(id+"F3.boolean.opBoolean","COPY",FACE,{"derivedFrom":makeQuery(id+"F3.opExtrude","SWEPT_FACE",FACE,{"disambiguationData":[OSD([sQuery(id+"F2.wireOp",EDGE,"E14")])]})}),makeQuery(id+"F35.opExtrude","CAP_FACE",FACE,{"disambiguationData":[OSD([sQuery(id+"F34.wireOp",EDGE,"E864")])],"isStart":false}),makeQuery(id+"F35.opExtrude","CAP_FACE",FACE,{"disambiguationData":[OSD([sQuery(id+"F34.wireOp",EDGE,"E865")])],"isStart":false})]});
            var sketch = newSketch(context, id + "F49", { "sketchPlane" : qUnion([Q0])});
            skText(sketch, "E895", { "text": "12v", "fontName": "OpenSans-Bold.ttf"});
            skText(sketch, "E896", { "text": "L3 L2 L1", "fontName": "OpenSans-Bold.ttf"});
            const initialGuessF49  = {"E895": [0.019, 0, 1, 0, 0.0042], "E896": [-0.00949, -0.00516, 1, 0, 0.00516]};
            skSetInitialGuess(sketch, initialGuessF49);
            skSolve(sketch);
        }
        {
            var Q0;
            {var subQ1=sQuery(id+"F0.wireOp",EDGE,"E7.rect.top");var subQ2=sQuery(id+"F0.wireOp",EDGE,"E7.rect.right");var subQ9=makeQuery(id+"F1.opExtrude","SWEPT_FACE",FACE,{"disambiguationData":[OSD([subQ1])]});Q0=makeQuery(id+"F19.boolean.opBoolean","SPLIT",FACE,{"disambiguationData":[TD([makeQuery(id+"F1.opExtrude","SWEPT_FACE",FACE,{"disambiguationData":[OSD([subQ2])]})])],"derivedFrom":subQ9});}
            var sketch = newSketch(context, id + "F50", { "sketchPlane" : qUnion([Q0])});
            skText(sketch, "E897", { "text": "S2", "fontName": "OpenSans-Bold.ttf"});
            skText(sketch, "E898", { "text": "S3", "fontName": "OpenSans-Bold.ttf"});
            skText(sketch, "E899", { "text": "S1", "fontName": "OpenSans-Bold.ttf"});
            const initialGuessF50  = {"E897": [0.0049, 0.00582, 1, 0, 0.00474], "E898": [-0.01363, 0, 1, 0, 0.0043], "E899": [0.02768, 0.00016, 1, 0, 0.0043]};
            skSetInitialGuess(sketch, initialGuessF50);
            skSolve(sketch);
        }
        {
            var Q0;
            {var subQ0=sQuery(id+"F2.wireOp",EDGE,"E22");var subQ1=sQuery(id+"F2.wireOp",EDGE,"E20");Q0=makeQuery(id+"F38.boolean.opBoolean","MERGE",FACE,{"derivedFrom":[makeQuery(id+"F24.boolean.opBoolean","SPLIT",FACE,{"disambiguationData":[TD([makeQuery(id+"F1.opExtrude","SWEPT_FACE",FACE,{"disambiguationData":[OSD([sQuery(id+"F0.wireOp",EDGE,"E3")])]})])],"derivedFrom":makeQuery(id+"F3.boolean.opBoolean","COPY",FACE,{"derivedFrom":makeQuery(id+"F3.opExtrude","SWEPT_FACE",FACE,{"disambiguationData":[OSD([subQ1,subQ0])]})})}),makeQuery(id+"F38.opExtrude","CAP_FACE",FACE,{"disambiguationData":[OSD([sQuery(id+"F37.wireOp",EDGE,"E866")])],"isStart":false}),makeQuery(id+"F38.opExtrude","CAP_FACE",FACE,{"disambiguationData":[OSD([sQuery(id+"F37.wireOp",EDGE,"E867")])],"isStart":false})]});}
            var sketch = newSketch(context, id + "F51", { "sketchPlane" : qUnion([Q0])});
            skText(sketch, "E900", { "text": "S6", "fontName": "OpenSans-Bold.ttf"});
            const initialGuessF51  = {"E900": [0.00608, -0.02103, 1, 0, 0.00418]};
            skSetInitialGuess(sketch, initialGuessF51);
            skSolve(sketch);
        }
        {
            var Q0;
            {var subQ1=sQuery(id+"F0.wireOp",EDGE,"E7.rect.left");var subQ3=sQuery(id+"F0.wireOp",EDGE,"E7.rect.bottom");Q0=makeQuery(id+"F9.boolean.opBoolean","SPLIT",FACE,{"disambiguationData":[TD([makeQuery(id+"F1.opExtrude","SWEPT_FACE",FACE,{"disambiguationData":[OSD([subQ3])]})])],"derivedFrom":makeQuery(id+"F1.opExtrude","SWEPT_FACE",FACE,{"disambiguationData":[OSD([subQ1])]})});}
            var sketch = newSketch(context, id + "F52", { "sketchPlane" : qUnion([Q0])});
            skText(sketch, "E901", { "text": "S5", "fontName": "OpenSans-Bold.ttf"});
            skText(sketch, "E902", { "text": "S4", "fontName": "OpenSans-Bold.ttf"});
            const initialGuessF52  = {"E901": [-0.02893, 0, 1, 0, 0.00488], "E902": [0.00624, 0, 1, 0, 0.0048]};
            skSetInitialGuess(sketch, initialGuessF52);
            skSolve(sketch);
        }
        {
            var Q0;
            {var subQ0=sQuery(id+"F12.wireOp",EDGE,"E51");Q0=makeQuery(id+"F12.imprint","IMPRINT",FACE,{"disambiguationData":[TD([[makeQuery(id+"F12.imprint","IMPRINT",EDGE,{"derivedFrom":subQ0}),-1.0]])]});}
            extrude(context, id + "F53", {"entities" : qUnion([Q0]), "operationType" : NewBodyOperationType.REMOVE, "oppositeDirection" : true, "depth" : 8 * mm});
        }
        {
            var Q0;
            Q0=makeQuery(id+"F0.imprint","IMPRINT",FACE,{"disambiguationData":[TD([[makeQuery(id+"F0.imprint","IMPRINT",EDGE,{"derivedFrom":sQuery(id+"F0.wireOp",EDGE,"E1")}),-1.0]])]});
            var sketch = newSketch(context, id + "F54", { "sketchPlane" : qUnion([Q0])});
            skPoint(sketch, "E903.first.point", {"position": v(6.62, 7.4) * mm});
            skPoint(sketch, "E903.second.point", {"position": v(6.67, 13.38) * mm});
            skPoint(sketch, "E903.third.point", {"position": v(3.73, 10.32) * mm});
            skPoint(sketch, "E904.first.point", {"position": v(17.45, 10.32) * mm});
            skPoint(sketch, "E904.second.point", {"position": v(14.7, 13.34) * mm});
            skPoint(sketch, "E904.third.point", {"position": v(14.7, 7.45) * mm});
            skPoint(sketch, "E905.MirrorP", {"position": v(17.5, 10.32) * mm});
            skPoint(sketch, "E906.MirrorP", {"position": v(14.62, 7.4) * mm});
            skPoint(sketch, "E907.MirrorP", {"position": v(14.57, 13.38) * mm});
            skLineSegment(sketch, "E908", {"start": v(14.46, 6.75) * mm, "end": v(6.63, 6.75) * mm});
            skLineSegment(sketch, "E909", {"start": v(14.66, 13.88) * mm, "end": v(6.96, 13.88) * mm});
            skArc(sketch, "E910.trimOffspring", {"start": v(6.96, 13.88) * mm, "mid": v(3.17, 10.38) * mm, "end": v(6.84, 6.75) * mm});
            skArc(sketch, "E911.trimOffspring", {"start": v(14.27, 13.88) * mm, "mid": v(18.08, 10.42) * mm, "end": v(14.46, 6.75) * mm});
            skPoint(sketch, "E912.orphan", {"position": v(14.5, 10.4) * mm});
            skPoint(sketch, "E913.start.orphan", {"position": v(10.62, 10.36) * mm});
            skCircle(sketch, "E914", {"center": v(6.74, 10.32) * mm, "radius": 2.01 * mm});
            skCircle(sketch, "E915", {"center": v(14.51, 10.32) * mm, "radius": 2.16 * mm});
            skLineSegment(sketch, "E916.trimOffspring", {"start": v(6.52, 13.88) * mm, "end": v(6.5, 13.88) * mm});
            skSolve(sketch);
        }
        {
            var Q0;
            Q0=qSketchRegion(id+"F54",true);
            extrude(context, id + "F55", {"entities" : qUnion([Q0]), "operationType" : NewBodyOperationType.REMOVE, "depth" : 8.2 * mm});
        }
    });
